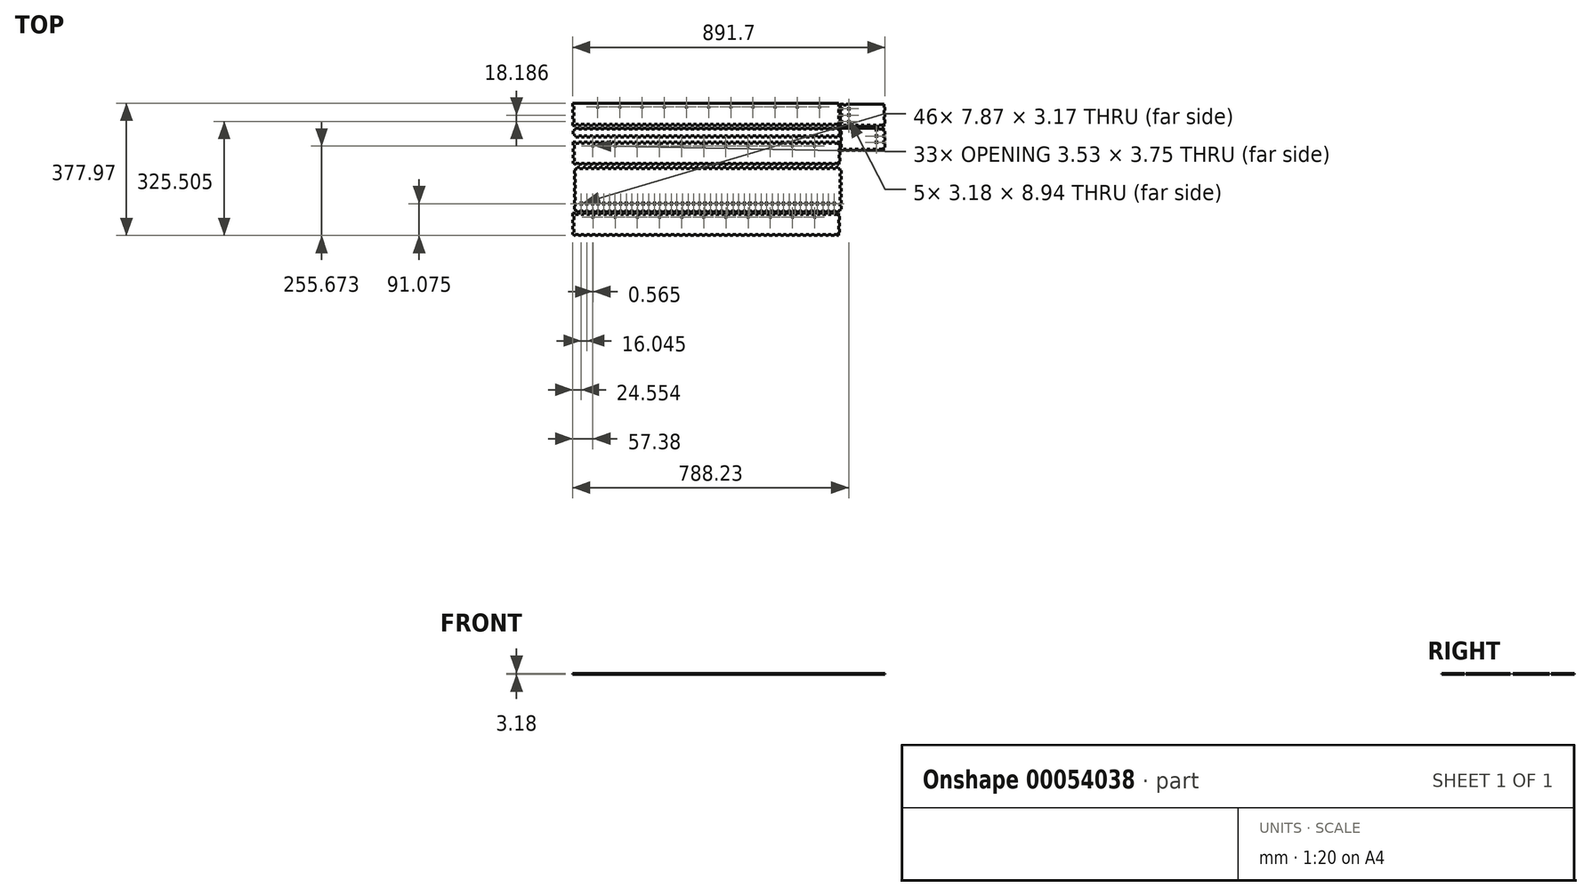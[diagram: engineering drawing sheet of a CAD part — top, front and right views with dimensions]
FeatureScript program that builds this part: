
annotation { "Feature Type Name" : "Feature", "Feature Type Description" : "" }
export const myFeature = defineFeature(function(context is Context, id is Id, definition is map)
    precondition{}
    {
        {
            var Q0;
            Q0=qCreatedBy(makeId("Top.planeOp"),FACE);
            var sketch = newSketch(context, id + "F0", { "sketchPlane" : qUnion([Q0])});
            skLineSegment(sketch, "E0", {"start": v(314.26, 109.75) * mm, "end": v(314.26, 115.01) * mm});
            skLineSegment(sketch, "E1", {"start": v(317.43, 109.75) * mm, "end": v(314.26, 109.75) * mm});
            skLineSegment(sketch, "E2", {"start": v(317.43, 101.12) * mm, "end": v(317.43, 109.75) * mm});
            skLineSegment(sketch, "E3", {"start": v(317.43, 101.12) * mm, "end": v(314.26, 101.12) * mm});
            skLineSegment(sketch, "E4", {"start": v(314.26, 95.9) * mm, "end": v(314.26, 101.12) * mm});
            skLineSegment(sketch, "E5", {"start": v(-441.55, 109.75) * mm, "end": v(-441.55, 115.16) * mm});
            skLineSegment(sketch, "E6", {"start": v(-441.55, 109.75) * mm, "end": v(-444.72, 109.75) * mm});
            skLineSegment(sketch, "E7", {"start": v(-444.72, 101.12) * mm, "end": v(-444.72, 109.75) * mm});
            skLineSegment(sketch, "E8", {"start": v(-441.55, 101.12) * mm, "end": v(-444.72, 101.12) * mm});
            skLineSegment(sketch, "E9", {"start": v(-441.55, 95.9) * mm, "end": v(-441.55, 101.12) * mm});
            skLineSegment(sketch, "E10", {"start": v(309.49, 114.97) * mm, "end": v(314.26, 114.97) * mm});
            skLineSegment(sketch, "E11", {"start": v(309.49, 118.14) * mm, "end": v(309.49, 114.97) * mm});
            skLineSegment(sketch, "E12", {"start": v(301.3, 118.14) * mm, "end": v(309.49, 118.14) * mm});
            skLineSegment(sketch, "E13", {"start": v(301.3, 118.14) * mm, "end": v(301.3, 114.97) * mm});
            skLineSegment(sketch, "E14", {"start": v(293.44, 114.97) * mm, "end": v(301.3, 114.97) * mm});
            skLineSegment(sketch, "E15", {"start": v(293.44, 118.14) * mm, "end": v(293.44, 114.97) * mm});
            skLineSegment(sketch, "E16", {"start": v(285.26, 118.14) * mm, "end": v(293.44, 118.14) * mm});
            skLineSegment(sketch, "E17", {"start": v(285.26, 118.14) * mm, "end": v(285.26, 114.97) * mm});
            skLineSegment(sketch, "E18", {"start": v(277.4, 114.97) * mm, "end": v(285.26, 114.97) * mm});
            skLineSegment(sketch, "E19", {"start": v(277.4, 118.14) * mm, "end": v(277.4, 114.97) * mm});
            skLineSegment(sketch, "E20", {"start": v(269.22, 118.14) * mm, "end": v(277.4, 118.14) * mm});
            skLineSegment(sketch, "E21", {"start": v(269.22, 118.14) * mm, "end": v(269.22, 114.97) * mm});
            skLineSegment(sketch, "E22", {"start": v(261.35, 114.97) * mm, "end": v(269.22, 114.97) * mm});
            skLineSegment(sketch, "E23", {"start": v(261.35, 118.14) * mm, "end": v(261.35, 114.97) * mm});
            skLineSegment(sketch, "E24", {"start": v(253.17, 118.14) * mm, "end": v(261.35, 118.14) * mm});
            skLineSegment(sketch, "E25", {"start": v(253.17, 118.14) * mm, "end": v(253.17, 114.97) * mm});
            skLineSegment(sketch, "E26", {"start": v(245.3, 114.97) * mm, "end": v(253.17, 114.97) * mm});
            skLineSegment(sketch, "E27", {"start": v(245.3, 118.14) * mm, "end": v(245.3, 114.97) * mm});
            skLineSegment(sketch, "E28", {"start": v(237.13, 118.14) * mm, "end": v(245.3, 118.14) * mm});
            skLineSegment(sketch, "E29", {"start": v(237.13, 118.14) * mm, "end": v(237.13, 114.97) * mm});
            skLineSegment(sketch, "E30", {"start": v(229.26, 114.97) * mm, "end": v(237.13, 114.97) * mm});
            skLineSegment(sketch, "E31", {"start": v(229.26, 118.14) * mm, "end": v(229.26, 114.97) * mm});
            skLineSegment(sketch, "E32", {"start": v(221.08, 118.14) * mm, "end": v(229.26, 118.14) * mm});
            skLineSegment(sketch, "E33", {"start": v(221.08, 118.14) * mm, "end": v(221.08, 114.97) * mm});
            skLineSegment(sketch, "E34", {"start": v(213.21, 114.97) * mm, "end": v(221.08, 114.97) * mm});
            skLineSegment(sketch, "E35", {"start": v(213.21, 118.14) * mm, "end": v(213.21, 114.97) * mm});
            skLineSegment(sketch, "E36", {"start": v(205.04, 118.14) * mm, "end": v(213.21, 118.14) * mm});
            skLineSegment(sketch, "E37", {"start": v(205.04, 118.14) * mm, "end": v(205.04, 114.97) * mm});
            skLineSegment(sketch, "E38", {"start": v(197.17, 114.97) * mm, "end": v(205.04, 114.97) * mm});
            skLineSegment(sketch, "E39", {"start": v(197.17, 118.14) * mm, "end": v(197.17, 114.97) * mm});
            skLineSegment(sketch, "E40", {"start": v(189, 118.14) * mm, "end": v(197.17, 118.14) * mm});
            skLineSegment(sketch, "E41", {"start": v(189, 118.14) * mm, "end": v(189, 114.97) * mm});
            skLineSegment(sketch, "E42", {"start": v(181.12, 114.97) * mm, "end": v(189, 114.97) * mm});
            skLineSegment(sketch, "E43", {"start": v(181.12, 118.14) * mm, "end": v(181.12, 114.97) * mm});
            skLineSegment(sketch, "E44", {"start": v(172.95, 118.14) * mm, "end": v(181.12, 118.14) * mm});
            skLineSegment(sketch, "E45", {"start": v(172.95, 118.14) * mm, "end": v(172.95, 114.97) * mm});
            skLineSegment(sketch, "E46", {"start": v(165.08, 114.97) * mm, "end": v(172.95, 114.97) * mm});
            skLineSegment(sketch, "E47", {"start": v(165.08, 118.14) * mm, "end": v(165.08, 114.97) * mm});
            skLineSegment(sketch, "E48", {"start": v(156.9, 118.14) * mm, "end": v(165.08, 118.14) * mm});
            skLineSegment(sketch, "E49", {"start": v(156.9, 118.14) * mm, "end": v(156.9, 114.97) * mm});
            skLineSegment(sketch, "E50", {"start": v(149.03, 114.97) * mm, "end": v(156.9, 114.97) * mm});
            skLineSegment(sketch, "E51", {"start": v(149.03, 118.14) * mm, "end": v(149.03, 114.97) * mm});
            skLineSegment(sketch, "E52", {"start": v(140.86, 118.14) * mm, "end": v(149.03, 118.14) * mm});
            skLineSegment(sketch, "E53", {"start": v(140.86, 118.14) * mm, "end": v(140.86, 114.97) * mm});
            skLineSegment(sketch, "E54", {"start": v(132.99, 114.97) * mm, "end": v(140.86, 114.97) * mm});
            skLineSegment(sketch, "E55", {"start": v(132.99, 118.14) * mm, "end": v(132.99, 114.97) * mm});
            skLineSegment(sketch, "E56", {"start": v(124.81, 118.14) * mm, "end": v(132.99, 118.14) * mm});
            skLineSegment(sketch, "E57", {"start": v(124.81, 118.14) * mm, "end": v(124.81, 114.97) * mm});
            skLineSegment(sketch, "E58", {"start": v(116.94, 114.97) * mm, "end": v(124.81, 114.97) * mm});
            skLineSegment(sketch, "E59", {"start": v(116.94, 118.14) * mm, "end": v(116.94, 114.97) * mm});
            skLineSegment(sketch, "E60", {"start": v(108.77, 118.14) * mm, "end": v(116.94, 118.14) * mm});
            skLineSegment(sketch, "E61", {"start": v(108.77, 118.14) * mm, "end": v(108.77, 114.97) * mm});
            skLineSegment(sketch, "E62", {"start": v(100.9, 114.97) * mm, "end": v(108.77, 114.97) * mm});
            skLineSegment(sketch, "E63", {"start": v(100.9, 118.14) * mm, "end": v(100.9, 114.97) * mm});
            skLineSegment(sketch, "E64", {"start": v(92.72, 118.14) * mm, "end": v(100.9, 118.14) * mm});
            skLineSegment(sketch, "E65", {"start": v(92.72, 118.14) * mm, "end": v(92.72, 114.97) * mm});
            skLineSegment(sketch, "E66", {"start": v(84.85, 114.97) * mm, "end": v(92.72, 114.97) * mm});
            skLineSegment(sketch, "E67", {"start": v(84.85, 118.14) * mm, "end": v(84.85, 114.97) * mm});
            skLineSegment(sketch, "E68", {"start": v(76.68, 118.14) * mm, "end": v(84.85, 118.14) * mm});
            skLineSegment(sketch, "E69", {"start": v(76.68, 118.14) * mm, "end": v(76.68, 114.97) * mm});
            skLineSegment(sketch, "E70", {"start": v(68.8, 114.97) * mm, "end": v(76.68, 114.97) * mm});
            skLineSegment(sketch, "E71", {"start": v(68.8, 118.14) * mm, "end": v(68.8, 114.97) * mm});
            skLineSegment(sketch, "E72", {"start": v(60.63, 118.14) * mm, "end": v(68.8, 118.14) * mm});
            skLineSegment(sketch, "E73", {"start": v(60.63, 118.14) * mm, "end": v(60.63, 114.97) * mm});
            skLineSegment(sketch, "E74", {"start": v(52.76, 114.97) * mm, "end": v(60.63, 114.97) * mm});
            skLineSegment(sketch, "E75", {"start": v(52.76, 118.14) * mm, "end": v(52.76, 114.97) * mm});
            skLineSegment(sketch, "E76", {"start": v(44.58, 118.14) * mm, "end": v(52.76, 118.14) * mm});
            skLineSegment(sketch, "E77", {"start": v(44.58, 118.14) * mm, "end": v(44.58, 114.97) * mm});
            skLineSegment(sketch, "E78", {"start": v(36.71, 114.97) * mm, "end": v(44.58, 114.97) * mm});
            skLineSegment(sketch, "E79", {"start": v(36.71, 118.14) * mm, "end": v(36.71, 114.97) * mm});
            skLineSegment(sketch, "E80", {"start": v(28.54, 118.14) * mm, "end": v(36.71, 118.14) * mm});
            skLineSegment(sketch, "E81", {"start": v(28.54, 118.14) * mm, "end": v(28.54, 114.97) * mm});
            skLineSegment(sketch, "E82", {"start": v(20.67, 114.97) * mm, "end": v(28.54, 114.97) * mm});
            skLineSegment(sketch, "E83", {"start": v(20.67, 118.14) * mm, "end": v(20.67, 114.97) * mm});
            skLineSegment(sketch, "E84", {"start": v(12.5, 118.14) * mm, "end": v(20.67, 118.14) * mm});
            skLineSegment(sketch, "E85", {"start": v(12.5, 118.14) * mm, "end": v(12.5, 114.97) * mm});
            skLineSegment(sketch, "E86", {"start": v(4.62, 114.97) * mm, "end": v(12.5, 114.97) * mm});
            skLineSegment(sketch, "E87", {"start": v(4.62, 118.14) * mm, "end": v(4.62, 114.97) * mm});
            skLineSegment(sketch, "E88", {"start": v(-3.55, 118.14) * mm, "end": v(4.62, 118.14) * mm});
            skLineSegment(sketch, "E89", {"start": v(-3.55, 118.14) * mm, "end": v(-3.55, 114.97) * mm});
            skLineSegment(sketch, "E90", {"start": v(-11.42, 114.97) * mm, "end": v(-3.55, 114.97) * mm});
            skLineSegment(sketch, "E91", {"start": v(-11.42, 118.14) * mm, "end": v(-11.42, 114.97) * mm});
            skLineSegment(sketch, "E92", {"start": v(-19.6, 118.14) * mm, "end": v(-11.42, 118.14) * mm});
            skLineSegment(sketch, "E93", {"start": v(-19.6, 118.14) * mm, "end": v(-19.6, 114.97) * mm});
            skLineSegment(sketch, "E94", {"start": v(-27.47, 114.97) * mm, "end": v(-19.6, 114.97) * mm});
            skLineSegment(sketch, "E95", {"start": v(-27.47, 118.14) * mm, "end": v(-27.47, 114.97) * mm});
            skLineSegment(sketch, "E96", {"start": v(-35.64, 118.14) * mm, "end": v(-27.47, 118.14) * mm});
            skLineSegment(sketch, "E97", {"start": v(-35.64, 118.14) * mm, "end": v(-35.64, 114.97) * mm});
            skLineSegment(sketch, "E98", {"start": v(-43.51, 114.97) * mm, "end": v(-35.64, 114.97) * mm});
            skLineSegment(sketch, "E99", {"start": v(-43.51, 118.14) * mm, "end": v(-43.51, 114.97) * mm});
            skLineSegment(sketch, "E100", {"start": v(-51.69, 118.14) * mm, "end": v(-43.51, 118.14) * mm});
            skLineSegment(sketch, "E101", {"start": v(-51.69, 118.14) * mm, "end": v(-51.69, 114.97) * mm});
            skLineSegment(sketch, "E102", {"start": v(-59.56, 114.97) * mm, "end": v(-51.69, 114.97) * mm});
            skLineSegment(sketch, "E103", {"start": v(-59.56, 118.14) * mm, "end": v(-59.56, 114.97) * mm});
            skLineSegment(sketch, "E104", {"start": v(-67.73, 118.14) * mm, "end": v(-59.56, 118.14) * mm});
            skLineSegment(sketch, "E105", {"start": v(-67.73, 118.14) * mm, "end": v(-67.73, 114.97) * mm});
            skLineSegment(sketch, "E106", {"start": v(-75.6, 114.97) * mm, "end": v(-67.73, 114.97) * mm});
            skLineSegment(sketch, "E107", {"start": v(-75.6, 118.14) * mm, "end": v(-75.6, 114.97) * mm});
            skLineSegment(sketch, "E108", {"start": v(-83.78, 118.14) * mm, "end": v(-75.6, 118.14) * mm});
            skLineSegment(sketch, "E109", {"start": v(-83.78, 118.14) * mm, "end": v(-83.78, 114.97) * mm});
            skLineSegment(sketch, "E110", {"start": v(-91.65, 114.97) * mm, "end": v(-83.78, 114.97) * mm});
            skLineSegment(sketch, "E111", {"start": v(-91.65, 118.14) * mm, "end": v(-91.65, 114.97) * mm});
            skLineSegment(sketch, "E112", {"start": v(-99.82, 118.14) * mm, "end": v(-91.65, 118.14) * mm});
            skLineSegment(sketch, "E113", {"start": v(-99.82, 118.14) * mm, "end": v(-99.82, 114.97) * mm});
            skLineSegment(sketch, "E114", {"start": v(-107.7, 114.97) * mm, "end": v(-99.82, 114.97) * mm});
            skLineSegment(sketch, "E115", {"start": v(-107.7, 118.14) * mm, "end": v(-107.7, 114.97) * mm});
            skLineSegment(sketch, "E116", {"start": v(-115.87, 118.14) * mm, "end": v(-107.7, 118.14) * mm});
            skLineSegment(sketch, "E117", {"start": v(-115.87, 118.14) * mm, "end": v(-115.87, 114.97) * mm});
            skLineSegment(sketch, "E118", {"start": v(-123.74, 114.97) * mm, "end": v(-115.87, 114.97) * mm});
            skLineSegment(sketch, "E119", {"start": v(-123.74, 118.14) * mm, "end": v(-123.74, 114.97) * mm});
            skLineSegment(sketch, "E120", {"start": v(-131.91, 118.14) * mm, "end": v(-123.74, 118.14) * mm});
            skLineSegment(sketch, "E121", {"start": v(-131.91, 118.14) * mm, "end": v(-131.91, 114.97) * mm});
            skLineSegment(sketch, "E122", {"start": v(-139.78, 114.97) * mm, "end": v(-131.91, 114.97) * mm});
            skLineSegment(sketch, "E123", {"start": v(-139.78, 118.14) * mm, "end": v(-139.78, 114.97) * mm});
            skLineSegment(sketch, "E124", {"start": v(-147.96, 118.14) * mm, "end": v(-139.78, 118.14) * mm});
            skLineSegment(sketch, "E125", {"start": v(-147.96, 118.14) * mm, "end": v(-147.96, 114.97) * mm});
            skLineSegment(sketch, "E126", {"start": v(-155.83, 114.97) * mm, "end": v(-147.96, 114.97) * mm});
            skLineSegment(sketch, "E127", {"start": v(-155.83, 118.14) * mm, "end": v(-155.83, 114.97) * mm});
            skLineSegment(sketch, "E128", {"start": v(-164, 118.14) * mm, "end": v(-155.83, 118.14) * mm});
            skLineSegment(sketch, "E129", {"start": v(-164, 118.14) * mm, "end": v(-164, 114.97) * mm});
            skLineSegment(sketch, "E130", {"start": v(-171.87, 114.97) * mm, "end": v(-164, 114.97) * mm});
            skLineSegment(sketch, "E131", {"start": v(-171.87, 118.14) * mm, "end": v(-171.87, 114.97) * mm});
            skLineSegment(sketch, "E132", {"start": v(-180.05, 118.14) * mm, "end": v(-171.87, 118.14) * mm});
            skLineSegment(sketch, "E133", {"start": v(-180.05, 118.14) * mm, "end": v(-180.05, 114.97) * mm});
            skLineSegment(sketch, "E134", {"start": v(-187.92, 114.97) * mm, "end": v(-180.05, 114.97) * mm});
            skLineSegment(sketch, "E135", {"start": v(-187.92, 118.14) * mm, "end": v(-187.92, 114.97) * mm});
            skLineSegment(sketch, "E136", {"start": v(-196.1, 118.14) * mm, "end": v(-187.92, 118.14) * mm});
            skLineSegment(sketch, "E137", {"start": v(-196.1, 118.14) * mm, "end": v(-196.1, 114.97) * mm});
            skLineSegment(sketch, "E138", {"start": v(-203.96, 114.97) * mm, "end": v(-196.1, 114.97) * mm});
            skLineSegment(sketch, "E139", {"start": v(-203.96, 118.14) * mm, "end": v(-203.96, 114.97) * mm});
            skLineSegment(sketch, "E140", {"start": v(-212.14, 118.14) * mm, "end": v(-203.96, 118.14) * mm});
            skLineSegment(sketch, "E141", {"start": v(-212.14, 118.14) * mm, "end": v(-212.14, 114.97) * mm});
            skLineSegment(sketch, "E142", {"start": v(-220.01, 114.97) * mm, "end": v(-212.14, 114.97) * mm});
            skLineSegment(sketch, "E143", {"start": v(-220.01, 118.14) * mm, "end": v(-220.01, 114.97) * mm});
            skLineSegment(sketch, "E144", {"start": v(-228.19, 118.14) * mm, "end": v(-220.01, 118.14) * mm});
            skLineSegment(sketch, "E145", {"start": v(-228.19, 118.14) * mm, "end": v(-228.19, 114.97) * mm});
            skLineSegment(sketch, "E146", {"start": v(-236.06, 114.97) * mm, "end": v(-228.19, 114.97) * mm});
            skLineSegment(sketch, "E147", {"start": v(-236.06, 118.14) * mm, "end": v(-236.06, 114.97) * mm});
            skLineSegment(sketch, "E148", {"start": v(-244.23, 118.14) * mm, "end": v(-236.06, 118.14) * mm});
            skLineSegment(sketch, "E149", {"start": v(-244.23, 118.14) * mm, "end": v(-244.23, 114.97) * mm});
            skLineSegment(sketch, "E150", {"start": v(-252.1, 114.97) * mm, "end": v(-244.23, 114.97) * mm});
            skLineSegment(sketch, "E151", {"start": v(-252.1, 118.14) * mm, "end": v(-252.1, 114.97) * mm});
            skLineSegment(sketch, "E152", {"start": v(-260.28, 118.14) * mm, "end": v(-252.1, 118.14) * mm});
            skLineSegment(sketch, "E153", {"start": v(-260.28, 118.14) * mm, "end": v(-260.28, 114.97) * mm});
            skLineSegment(sketch, "E154", {"start": v(-268.15, 114.97) * mm, "end": v(-260.28, 114.97) * mm});
            skLineSegment(sketch, "E155", {"start": v(-268.15, 118.14) * mm, "end": v(-268.15, 114.97) * mm});
            skLineSegment(sketch, "E156", {"start": v(-276.32, 118.14) * mm, "end": v(-268.15, 118.14) * mm});
            skLineSegment(sketch, "E157", {"start": v(-276.32, 118.14) * mm, "end": v(-276.32, 114.97) * mm});
            skLineSegment(sketch, "E158", {"start": v(-284.2, 114.97) * mm, "end": v(-276.32, 114.97) * mm});
            skLineSegment(sketch, "E159", {"start": v(-284.2, 118.14) * mm, "end": v(-284.2, 114.97) * mm});
            skLineSegment(sketch, "E160", {"start": v(-292.37, 118.14) * mm, "end": v(-284.2, 118.14) * mm});
            skLineSegment(sketch, "E161", {"start": v(-292.37, 118.14) * mm, "end": v(-292.37, 114.97) * mm});
            skLineSegment(sketch, "E162", {"start": v(-300.24, 114.97) * mm, "end": v(-292.37, 114.97) * mm});
            skLineSegment(sketch, "E163", {"start": v(-300.24, 118.14) * mm, "end": v(-300.24, 114.97) * mm});
            skLineSegment(sketch, "E164", {"start": v(-308.41, 118.14) * mm, "end": v(-300.24, 118.14) * mm});
            skLineSegment(sketch, "E165", {"start": v(-308.41, 118.14) * mm, "end": v(-308.41, 114.97) * mm});
            skLineSegment(sketch, "E166", {"start": v(-316.28, 114.97) * mm, "end": v(-308.41, 114.97) * mm});
            skLineSegment(sketch, "E167", {"start": v(-316.28, 118.14) * mm, "end": v(-316.28, 114.97) * mm});
            skLineSegment(sketch, "E168", {"start": v(-324.46, 118.14) * mm, "end": v(-316.28, 118.14) * mm});
            skLineSegment(sketch, "E169", {"start": v(-324.46, 118.14) * mm, "end": v(-324.46, 114.97) * mm});
            skLineSegment(sketch, "E170", {"start": v(-332.33, 114.97) * mm, "end": v(-324.46, 114.97) * mm});
            skLineSegment(sketch, "E171", {"start": v(-332.33, 118.14) * mm, "end": v(-332.33, 114.97) * mm});
            skLineSegment(sketch, "E172", {"start": v(-340.5, 118.14) * mm, "end": v(-332.33, 118.14) * mm});
            skLineSegment(sketch, "E173", {"start": v(-340.5, 118.14) * mm, "end": v(-340.5, 114.97) * mm});
            skLineSegment(sketch, "E174", {"start": v(-348.37, 114.97) * mm, "end": v(-340.5, 114.97) * mm});
            skLineSegment(sketch, "E175", {"start": v(-348.37, 118.14) * mm, "end": v(-348.37, 114.97) * mm});
            skLineSegment(sketch, "E176", {"start": v(-356.55, 118.14) * mm, "end": v(-348.37, 118.14) * mm});
            skLineSegment(sketch, "E177", {"start": v(-356.55, 118.14) * mm, "end": v(-356.55, 114.97) * mm});
            skLineSegment(sketch, "E178", {"start": v(-364.42, 114.97) * mm, "end": v(-356.55, 114.97) * mm});
            skLineSegment(sketch, "E179", {"start": v(-364.42, 118.14) * mm, "end": v(-364.42, 114.97) * mm});
            skLineSegment(sketch, "E180", {"start": v(-372.6, 118.14) * mm, "end": v(-364.42, 118.14) * mm});
            skLineSegment(sketch, "E181", {"start": v(-372.6, 118.14) * mm, "end": v(-372.6, 114.97) * mm});
            skLineSegment(sketch, "E182", {"start": v(-380.46, 114.97) * mm, "end": v(-372.6, 114.97) * mm});
            skLineSegment(sketch, "E183", {"start": v(-380.46, 118.14) * mm, "end": v(-380.46, 114.97) * mm});
            skLineSegment(sketch, "E184", {"start": v(-388.64, 118.14) * mm, "end": v(-380.46, 118.14) * mm});
            skLineSegment(sketch, "E185", {"start": v(-388.64, 118.14) * mm, "end": v(-388.64, 114.97) * mm});
            skLineSegment(sketch, "E186", {"start": v(-396.5, 114.97) * mm, "end": v(-388.64, 114.97) * mm});
            skLineSegment(sketch, "E187", {"start": v(-396.5, 118.14) * mm, "end": v(-396.5, 114.97) * mm});
            skLineSegment(sketch, "E188", {"start": v(-404.68, 118.14) * mm, "end": v(-396.5, 118.14) * mm});
            skLineSegment(sketch, "E189", {"start": v(-404.68, 118.14) * mm, "end": v(-404.68, 114.97) * mm});
            skLineSegment(sketch, "E190", {"start": v(-412.55, 114.97) * mm, "end": v(-404.68, 114.97) * mm});
            skLineSegment(sketch, "E191", {"start": v(-412.55, 118.14) * mm, "end": v(-412.55, 114.97) * mm});
            skLineSegment(sketch, "E192", {"start": v(-420.73, 118.14) * mm, "end": v(-412.55, 118.14) * mm});
            skLineSegment(sketch, "E193", {"start": v(-420.73, 118.14) * mm, "end": v(-420.73, 114.97) * mm});
            skLineSegment(sketch, "E194", {"start": v(-428.6, 114.97) * mm, "end": v(-420.73, 114.97) * mm});
            skLineSegment(sketch, "E195", {"start": v(-428.6, 118.14) * mm, "end": v(-428.6, 114.97) * mm});
            skLineSegment(sketch, "E196", {"start": v(-436.77, 118.14) * mm, "end": v(-428.6, 118.14) * mm});
            skLineSegment(sketch, "E197", {"start": v(-436.77, 118.14) * mm, "end": v(-436.77, 114.97) * mm});
            skLineSegment(sketch, "E198", {"start": v(-441.55, 114.97) * mm, "end": v(-436.77, 114.97) * mm});
            skLineSegment(sketch, "E199", {"start": v(309.49, 95.9) * mm, "end": v(314.26, 95.9) * mm});
            skLineSegment(sketch, "E200", {"start": v(309.49, 95.9) * mm, "end": v(309.49, 92.72) * mm});
            skLineSegment(sketch, "E201", {"start": v(301.3, 92.72) * mm, "end": v(309.49, 92.72) * mm});
            skLineSegment(sketch, "E202", {"start": v(301.3, 95.9) * mm, "end": v(301.3, 92.72) * mm});
            skLineSegment(sketch, "E203", {"start": v(293.44, 95.9) * mm, "end": v(301.3, 95.9) * mm});
            skLineSegment(sketch, "E204", {"start": v(293.44, 95.9) * mm, "end": v(293.44, 92.72) * mm});
            skLineSegment(sketch, "E205", {"start": v(285.26, 92.72) * mm, "end": v(293.44, 92.72) * mm});
            skLineSegment(sketch, "E206", {"start": v(285.26, 95.9) * mm, "end": v(285.26, 92.72) * mm});
            skLineSegment(sketch, "E207", {"start": v(277.4, 95.9) * mm, "end": v(285.26, 95.9) * mm});
            skLineSegment(sketch, "E208", {"start": v(277.4, 95.9) * mm, "end": v(277.4, 92.72) * mm});
            skLineSegment(sketch, "E209", {"start": v(269.22, 92.72) * mm, "end": v(277.4, 92.72) * mm});
            skLineSegment(sketch, "E210", {"start": v(269.22, 95.9) * mm, "end": v(269.22, 92.72) * mm});
            skLineSegment(sketch, "E211", {"start": v(261.35, 95.9) * mm, "end": v(269.22, 95.9) * mm});
            skLineSegment(sketch, "E212", {"start": v(261.35, 95.9) * mm, "end": v(261.35, 92.72) * mm});
            skLineSegment(sketch, "E213", {"start": v(253.17, 92.72) * mm, "end": v(261.35, 92.72) * mm});
            skLineSegment(sketch, "E214", {"start": v(253.17, 95.9) * mm, "end": v(253.17, 92.72) * mm});
            skLineSegment(sketch, "E215", {"start": v(245.3, 95.9) * mm, "end": v(253.17, 95.9) * mm});
            skLineSegment(sketch, "E216", {"start": v(245.3, 95.9) * mm, "end": v(245.3, 92.72) * mm});
            skLineSegment(sketch, "E217", {"start": v(237.13, 92.72) * mm, "end": v(245.3, 92.72) * mm});
            skLineSegment(sketch, "E218", {"start": v(237.13, 95.9) * mm, "end": v(237.13, 92.72) * mm});
            skLineSegment(sketch, "E219", {"start": v(229.26, 95.9) * mm, "end": v(237.13, 95.9) * mm});
            skLineSegment(sketch, "E220", {"start": v(229.26, 95.9) * mm, "end": v(229.26, 92.72) * mm});
            skLineSegment(sketch, "E221", {"start": v(221.08, 92.72) * mm, "end": v(229.26, 92.72) * mm});
            skLineSegment(sketch, "E222", {"start": v(221.08, 95.9) * mm, "end": v(221.08, 92.72) * mm});
            skLineSegment(sketch, "E223", {"start": v(213.21, 95.9) * mm, "end": v(221.08, 95.9) * mm});
            skLineSegment(sketch, "E224", {"start": v(213.21, 95.9) * mm, "end": v(213.21, 92.72) * mm});
            skLineSegment(sketch, "E225", {"start": v(205.04, 92.72) * mm, "end": v(213.21, 92.72) * mm});
            skLineSegment(sketch, "E226", {"start": v(205.04, 95.9) * mm, "end": v(205.04, 92.72) * mm});
            skLineSegment(sketch, "E227", {"start": v(197.17, 95.9) * mm, "end": v(205.04, 95.9) * mm});
            skLineSegment(sketch, "E228", {"start": v(197.17, 95.9) * mm, "end": v(197.17, 92.72) * mm});
            skLineSegment(sketch, "E229", {"start": v(189, 92.72) * mm, "end": v(197.17, 92.72) * mm});
            skLineSegment(sketch, "E230", {"start": v(189, 95.9) * mm, "end": v(189, 92.72) * mm});
            skLineSegment(sketch, "E231", {"start": v(181.12, 95.9) * mm, "end": v(189, 95.9) * mm});
            skLineSegment(sketch, "E232", {"start": v(181.12, 95.9) * mm, "end": v(181.12, 92.72) * mm});
            skLineSegment(sketch, "E233", {"start": v(172.95, 92.72) * mm, "end": v(181.12, 92.72) * mm});
            skLineSegment(sketch, "E234", {"start": v(172.95, 95.9) * mm, "end": v(172.95, 92.72) * mm});
            skLineSegment(sketch, "E235", {"start": v(165.08, 95.9) * mm, "end": v(172.95, 95.9) * mm});
            skLineSegment(sketch, "E236", {"start": v(165.08, 95.9) * mm, "end": v(165.08, 92.72) * mm});
            skLineSegment(sketch, "E237", {"start": v(156.9, 92.72) * mm, "end": v(165.08, 92.72) * mm});
            skLineSegment(sketch, "E238", {"start": v(156.9, 95.9) * mm, "end": v(156.9, 92.72) * mm});
            skLineSegment(sketch, "E239", {"start": v(149.03, 95.9) * mm, "end": v(156.9, 95.9) * mm});
            skLineSegment(sketch, "E240", {"start": v(149.03, 95.9) * mm, "end": v(149.03, 92.72) * mm});
            skLineSegment(sketch, "E241", {"start": v(140.86, 92.72) * mm, "end": v(149.03, 92.72) * mm});
            skLineSegment(sketch, "E242", {"start": v(140.86, 95.9) * mm, "end": v(140.86, 92.72) * mm});
            skLineSegment(sketch, "E243", {"start": v(132.99, 95.9) * mm, "end": v(140.86, 95.9) * mm});
            skLineSegment(sketch, "E244", {"start": v(132.99, 95.9) * mm, "end": v(132.99, 92.72) * mm});
            skLineSegment(sketch, "E245", {"start": v(124.81, 92.72) * mm, "end": v(132.99, 92.72) * mm});
            skLineSegment(sketch, "E246", {"start": v(124.81, 95.9) * mm, "end": v(124.81, 92.72) * mm});
            skLineSegment(sketch, "E247", {"start": v(116.94, 95.9) * mm, "end": v(124.81, 95.9) * mm});
            skLineSegment(sketch, "E248", {"start": v(116.94, 95.9) * mm, "end": v(116.94, 92.72) * mm});
            skLineSegment(sketch, "E249", {"start": v(108.77, 92.72) * mm, "end": v(116.94, 92.72) * mm});
            skLineSegment(sketch, "E250", {"start": v(108.77, 95.9) * mm, "end": v(108.77, 92.72) * mm});
            skLineSegment(sketch, "E251", {"start": v(100.9, 95.9) * mm, "end": v(108.77, 95.9) * mm});
            skLineSegment(sketch, "E252", {"start": v(100.9, 95.9) * mm, "end": v(100.9, 92.72) * mm});
            skLineSegment(sketch, "E253", {"start": v(92.72, 92.72) * mm, "end": v(100.9, 92.72) * mm});
            skLineSegment(sketch, "E254", {"start": v(92.72, 95.9) * mm, "end": v(92.72, 92.72) * mm});
            skLineSegment(sketch, "E255", {"start": v(84.85, 95.9) * mm, "end": v(92.72, 95.9) * mm});
            skLineSegment(sketch, "E256", {"start": v(84.85, 95.9) * mm, "end": v(84.85, 92.72) * mm});
            skLineSegment(sketch, "E257", {"start": v(76.68, 92.72) * mm, "end": v(84.85, 92.72) * mm});
            skLineSegment(sketch, "E258", {"start": v(76.68, 95.9) * mm, "end": v(76.68, 92.72) * mm});
            skLineSegment(sketch, "E259", {"start": v(68.8, 95.9) * mm, "end": v(76.68, 95.9) * mm});
            skLineSegment(sketch, "E260", {"start": v(68.8, 95.9) * mm, "end": v(68.8, 92.72) * mm});
            skLineSegment(sketch, "E261", {"start": v(60.63, 92.72) * mm, "end": v(68.8, 92.72) * mm});
            skLineSegment(sketch, "E262", {"start": v(60.63, 95.9) * mm, "end": v(60.63, 92.72) * mm});
            skLineSegment(sketch, "E263", {"start": v(52.76, 95.9) * mm, "end": v(60.63, 95.9) * mm});
            skLineSegment(sketch, "E264", {"start": v(52.76, 95.9) * mm, "end": v(52.76, 92.72) * mm});
            skLineSegment(sketch, "E265", {"start": v(44.58, 92.72) * mm, "end": v(52.76, 92.72) * mm});
            skLineSegment(sketch, "E266", {"start": v(44.58, 95.9) * mm, "end": v(44.58, 92.72) * mm});
            skLineSegment(sketch, "E267", {"start": v(36.71, 95.9) * mm, "end": v(44.58, 95.9) * mm});
            skLineSegment(sketch, "E268", {"start": v(36.71, 95.9) * mm, "end": v(36.71, 92.72) * mm});
            skLineSegment(sketch, "E269", {"start": v(28.54, 92.72) * mm, "end": v(36.71, 92.72) * mm});
            skLineSegment(sketch, "E270", {"start": v(28.54, 95.9) * mm, "end": v(28.54, 92.72) * mm});
            skLineSegment(sketch, "E271", {"start": v(20.67, 95.9) * mm, "end": v(28.54, 95.9) * mm});
            skLineSegment(sketch, "E272", {"start": v(20.67, 95.9) * mm, "end": v(20.67, 92.72) * mm});
            skLineSegment(sketch, "E273", {"start": v(12.5, 92.72) * mm, "end": v(20.67, 92.72) * mm});
            skLineSegment(sketch, "E274", {"start": v(12.5, 95.9) * mm, "end": v(12.5, 92.72) * mm});
            skLineSegment(sketch, "E275", {"start": v(4.62, 95.9) * mm, "end": v(12.5, 95.9) * mm});
            skLineSegment(sketch, "E276", {"start": v(4.62, 95.9) * mm, "end": v(4.62, 92.72) * mm});
            skLineSegment(sketch, "E277", {"start": v(-3.55, 92.72) * mm, "end": v(4.62, 92.72) * mm});
            skLineSegment(sketch, "E278", {"start": v(-3.55, 95.9) * mm, "end": v(-3.55, 92.72) * mm});
            skLineSegment(sketch, "E279", {"start": v(-11.42, 95.9) * mm, "end": v(-3.55, 95.9) * mm});
            skLineSegment(sketch, "E280", {"start": v(-11.42, 95.9) * mm, "end": v(-11.42, 92.72) * mm});
            skLineSegment(sketch, "E281", {"start": v(-19.6, 92.72) * mm, "end": v(-11.42, 92.72) * mm});
            skLineSegment(sketch, "E282", {"start": v(-19.6, 95.9) * mm, "end": v(-19.6, 92.72) * mm});
            skLineSegment(sketch, "E283", {"start": v(-27.47, 95.9) * mm, "end": v(-19.6, 95.9) * mm});
            skLineSegment(sketch, "E284", {"start": v(-27.47, 95.9) * mm, "end": v(-27.47, 92.72) * mm});
            skLineSegment(sketch, "E285", {"start": v(-35.64, 92.72) * mm, "end": v(-27.47, 92.72) * mm});
            skLineSegment(sketch, "E286", {"start": v(-35.64, 95.9) * mm, "end": v(-35.64, 92.72) * mm});
            skLineSegment(sketch, "E287", {"start": v(-43.51, 95.9) * mm, "end": v(-35.64, 95.9) * mm});
            skLineSegment(sketch, "E288", {"start": v(-43.51, 95.9) * mm, "end": v(-43.51, 92.72) * mm});
            skLineSegment(sketch, "E289", {"start": v(-51.69, 92.72) * mm, "end": v(-43.51, 92.72) * mm});
            skLineSegment(sketch, "E290", {"start": v(-51.69, 95.9) * mm, "end": v(-51.69, 92.72) * mm});
            skLineSegment(sketch, "E291", {"start": v(-59.56, 95.9) * mm, "end": v(-51.69, 95.9) * mm});
            skLineSegment(sketch, "E292", {"start": v(-59.56, 95.9) * mm, "end": v(-59.56, 92.72) * mm});
            skLineSegment(sketch, "E293", {"start": v(-67.73, 92.72) * mm, "end": v(-59.56, 92.72) * mm});
            skLineSegment(sketch, "E294", {"start": v(-67.73, 95.9) * mm, "end": v(-67.73, 92.72) * mm});
            skLineSegment(sketch, "E295", {"start": v(-75.6, 95.9) * mm, "end": v(-67.73, 95.9) * mm});
            skLineSegment(sketch, "E296", {"start": v(-75.6, 95.9) * mm, "end": v(-75.6, 92.72) * mm});
            skLineSegment(sketch, "E297", {"start": v(-83.78, 92.72) * mm, "end": v(-75.6, 92.72) * mm});
            skLineSegment(sketch, "E298", {"start": v(-83.78, 95.9) * mm, "end": v(-83.78, 92.72) * mm});
            skLineSegment(sketch, "E299", {"start": v(-91.65, 95.9) * mm, "end": v(-83.78, 95.9) * mm});
            skLineSegment(sketch, "E300", {"start": v(-91.65, 95.9) * mm, "end": v(-91.65, 92.72) * mm});
            skLineSegment(sketch, "E301", {"start": v(-99.82, 92.72) * mm, "end": v(-91.65, 92.72) * mm});
            skLineSegment(sketch, "E302", {"start": v(-99.82, 95.9) * mm, "end": v(-99.82, 92.72) * mm});
            skLineSegment(sketch, "E303", {"start": v(-107.7, 95.9) * mm, "end": v(-99.82, 95.9) * mm});
            skLineSegment(sketch, "E304", {"start": v(-107.7, 95.9) * mm, "end": v(-107.7, 92.72) * mm});
            skLineSegment(sketch, "E305", {"start": v(-115.87, 92.72) * mm, "end": v(-107.7, 92.72) * mm});
            skLineSegment(sketch, "E306", {"start": v(-115.87, 95.9) * mm, "end": v(-115.87, 92.72) * mm});
            skLineSegment(sketch, "E307", {"start": v(-123.74, 95.9) * mm, "end": v(-115.87, 95.9) * mm});
            skLineSegment(sketch, "E308", {"start": v(-123.74, 95.9) * mm, "end": v(-123.74, 92.72) * mm});
            skLineSegment(sketch, "E309", {"start": v(-131.91, 92.72) * mm, "end": v(-123.74, 92.72) * mm});
            skLineSegment(sketch, "E310", {"start": v(-131.91, 95.9) * mm, "end": v(-131.91, 92.72) * mm});
            skLineSegment(sketch, "E311", {"start": v(-139.78, 95.9) * mm, "end": v(-131.91, 95.9) * mm});
            skLineSegment(sketch, "E312", {"start": v(-139.78, 95.9) * mm, "end": v(-139.78, 92.72) * mm});
            skLineSegment(sketch, "E313", {"start": v(-147.96, 92.72) * mm, "end": v(-139.78, 92.72) * mm});
            skLineSegment(sketch, "E314", {"start": v(-147.96, 95.9) * mm, "end": v(-147.96, 92.72) * mm});
            skLineSegment(sketch, "E315", {"start": v(-155.83, 95.9) * mm, "end": v(-147.96, 95.9) * mm});
            skLineSegment(sketch, "E316", {"start": v(-155.83, 95.9) * mm, "end": v(-155.83, 92.72) * mm});
            skLineSegment(sketch, "E317", {"start": v(-164, 92.72) * mm, "end": v(-155.83, 92.72) * mm});
            skLineSegment(sketch, "E318", {"start": v(-164, 95.9) * mm, "end": v(-164, 92.72) * mm});
            skLineSegment(sketch, "E319", {"start": v(-171.87, 95.9) * mm, "end": v(-164, 95.9) * mm});
            skLineSegment(sketch, "E320", {"start": v(-171.87, 95.9) * mm, "end": v(-171.87, 92.72) * mm});
            skLineSegment(sketch, "E321", {"start": v(-180.05, 92.72) * mm, "end": v(-171.87, 92.72) * mm});
            skLineSegment(sketch, "E322", {"start": v(-180.05, 95.9) * mm, "end": v(-180.05, 92.72) * mm});
            skLineSegment(sketch, "E323", {"start": v(-187.92, 95.9) * mm, "end": v(-180.05, 95.9) * mm});
            skLineSegment(sketch, "E324", {"start": v(-187.92, 95.9) * mm, "end": v(-187.92, 92.72) * mm});
            skLineSegment(sketch, "E325", {"start": v(-196.1, 92.72) * mm, "end": v(-187.92, 92.72) * mm});
            skLineSegment(sketch, "E326", {"start": v(-196.1, 95.9) * mm, "end": v(-196.1, 92.72) * mm});
            skLineSegment(sketch, "E327", {"start": v(-203.96, 95.9) * mm, "end": v(-196.1, 95.9) * mm});
            skLineSegment(sketch, "E328", {"start": v(-203.96, 95.9) * mm, "end": v(-203.96, 92.72) * mm});
            skLineSegment(sketch, "E329", {"start": v(-212.14, 92.72) * mm, "end": v(-203.96, 92.72) * mm});
            skLineSegment(sketch, "E330", {"start": v(-212.14, 95.9) * mm, "end": v(-212.14, 92.72) * mm});
            skLineSegment(sketch, "E331", {"start": v(-220.01, 95.9) * mm, "end": v(-212.14, 95.9) * mm});
            skLineSegment(sketch, "E332", {"start": v(-220.01, 95.9) * mm, "end": v(-220.01, 92.72) * mm});
            skLineSegment(sketch, "E333", {"start": v(-228.19, 92.72) * mm, "end": v(-220.01, 92.72) * mm});
            skLineSegment(sketch, "E334", {"start": v(-228.19, 95.9) * mm, "end": v(-228.19, 92.72) * mm});
            skLineSegment(sketch, "E335", {"start": v(-236.06, 95.9) * mm, "end": v(-228.19, 95.9) * mm});
            skLineSegment(sketch, "E336", {"start": v(-236.06, 95.9) * mm, "end": v(-236.06, 92.72) * mm});
            skLineSegment(sketch, "E337", {"start": v(-244.23, 92.72) * mm, "end": v(-236.06, 92.72) * mm});
            skLineSegment(sketch, "E338", {"start": v(-244.23, 95.9) * mm, "end": v(-244.23, 92.72) * mm});
            skLineSegment(sketch, "E339", {"start": v(-252.1, 95.9) * mm, "end": v(-244.23, 95.9) * mm});
            skLineSegment(sketch, "E340", {"start": v(-252.1, 95.9) * mm, "end": v(-252.1, 92.72) * mm});
            skLineSegment(sketch, "E341", {"start": v(-260.28, 92.72) * mm, "end": v(-252.1, 92.72) * mm});
            skLineSegment(sketch, "E342", {"start": v(-260.28, 95.9) * mm, "end": v(-260.28, 92.72) * mm});
            skLineSegment(sketch, "E343", {"start": v(-268.15, 95.9) * mm, "end": v(-260.28, 95.9) * mm});
            skLineSegment(sketch, "E344", {"start": v(-268.15, 95.9) * mm, "end": v(-268.15, 92.72) * mm});
            skLineSegment(sketch, "E345", {"start": v(-276.32, 92.72) * mm, "end": v(-268.15, 92.72) * mm});
            skLineSegment(sketch, "E346", {"start": v(-276.32, 95.9) * mm, "end": v(-276.32, 92.72) * mm});
            skLineSegment(sketch, "E347", {"start": v(-284.2, 95.9) * mm, "end": v(-276.32, 95.9) * mm});
            skLineSegment(sketch, "E348", {"start": v(-284.2, 95.9) * mm, "end": v(-284.2, 92.72) * mm});
            skLineSegment(sketch, "E349", {"start": v(-292.37, 92.72) * mm, "end": v(-284.2, 92.72) * mm});
            skLineSegment(sketch, "E350", {"start": v(-292.37, 95.9) * mm, "end": v(-292.37, 92.72) * mm});
            skLineSegment(sketch, "E351", {"start": v(-300.24, 95.9) * mm, "end": v(-292.37, 95.9) * mm});
            skLineSegment(sketch, "E352", {"start": v(-300.24, 95.9) * mm, "end": v(-300.24, 92.72) * mm});
            skLineSegment(sketch, "E353", {"start": v(-308.41, 92.72) * mm, "end": v(-300.24, 92.72) * mm});
            skLineSegment(sketch, "E354", {"start": v(-308.41, 95.9) * mm, "end": v(-308.41, 92.72) * mm});
            skLineSegment(sketch, "E355", {"start": v(-316.28, 95.9) * mm, "end": v(-308.41, 95.9) * mm});
            skLineSegment(sketch, "E356", {"start": v(-316.28, 95.9) * mm, "end": v(-316.28, 92.72) * mm});
            skLineSegment(sketch, "E357", {"start": v(-324.46, 92.72) * mm, "end": v(-316.28, 92.72) * mm});
            skLineSegment(sketch, "E358", {"start": v(-324.46, 95.9) * mm, "end": v(-324.46, 92.72) * mm});
            skLineSegment(sketch, "E359", {"start": v(-332.33, 95.9) * mm, "end": v(-324.46, 95.9) * mm});
            skLineSegment(sketch, "E360", {"start": v(-332.33, 95.9) * mm, "end": v(-332.33, 92.72) * mm});
            skLineSegment(sketch, "E361", {"start": v(-340.5, 92.72) * mm, "end": v(-332.33, 92.72) * mm});
            skLineSegment(sketch, "E362", {"start": v(-340.5, 95.9) * mm, "end": v(-340.5, 92.72) * mm});
            skLineSegment(sketch, "E363", {"start": v(-348.37, 95.9) * mm, "end": v(-340.5, 95.9) * mm});
            skLineSegment(sketch, "E364", {"start": v(-348.37, 95.9) * mm, "end": v(-348.37, 92.72) * mm});
            skLineSegment(sketch, "E365", {"start": v(-356.55, 92.72) * mm, "end": v(-348.37, 92.72) * mm});
            skLineSegment(sketch, "E366", {"start": v(-356.55, 95.9) * mm, "end": v(-356.55, 92.72) * mm});
            skLineSegment(sketch, "E367", {"start": v(-364.42, 95.9) * mm, "end": v(-356.55, 95.9) * mm});
            skLineSegment(sketch, "E368", {"start": v(-364.42, 95.9) * mm, "end": v(-364.42, 92.72) * mm});
            skLineSegment(sketch, "E369", {"start": v(-372.6, 92.72) * mm, "end": v(-364.42, 92.72) * mm});
            skLineSegment(sketch, "E370", {"start": v(-372.6, 95.9) * mm, "end": v(-372.6, 92.72) * mm});
            skLineSegment(sketch, "E371", {"start": v(-380.46, 95.9) * mm, "end": v(-372.6, 95.9) * mm});
            skLineSegment(sketch, "E372", {"start": v(-380.46, 95.9) * mm, "end": v(-380.46, 92.72) * mm});
            skLineSegment(sketch, "E373", {"start": v(-388.64, 92.72) * mm, "end": v(-380.46, 92.72) * mm});
            skLineSegment(sketch, "E374", {"start": v(-388.64, 95.9) * mm, "end": v(-388.64, 92.72) * mm});
            skLineSegment(sketch, "E375", {"start": v(-396.5, 95.9) * mm, "end": v(-388.64, 95.9) * mm});
            skLineSegment(sketch, "E376", {"start": v(-396.5, 95.9) * mm, "end": v(-396.5, 92.72) * mm});
            skLineSegment(sketch, "E377", {"start": v(-404.68, 92.72) * mm, "end": v(-396.5, 92.72) * mm});
            skLineSegment(sketch, "E378", {"start": v(-404.68, 95.9) * mm, "end": v(-404.68, 92.72) * mm});
            skLineSegment(sketch, "E379", {"start": v(-412.55, 95.9) * mm, "end": v(-404.68, 95.9) * mm});
            skLineSegment(sketch, "E380", {"start": v(-412.55, 95.9) * mm, "end": v(-412.55, 92.72) * mm});
            skLineSegment(sketch, "E381", {"start": v(-420.73, 92.72) * mm, "end": v(-412.55, 92.72) * mm});
            skLineSegment(sketch, "E382", {"start": v(-420.73, 95.9) * mm, "end": v(-420.73, 92.72) * mm});
            skLineSegment(sketch, "E383", {"start": v(-428.6, 95.9) * mm, "end": v(-420.73, 95.9) * mm});
            skLineSegment(sketch, "E384", {"start": v(-428.6, 95.9) * mm, "end": v(-428.6, 92.72) * mm});
            skLineSegment(sketch, "E385", {"start": v(-436.77, 92.72) * mm, "end": v(-428.6, 92.72) * mm});
            skLineSegment(sketch, "E386", {"start": v(-436.77, 95.9) * mm, "end": v(-436.77, 92.72) * mm});
            skLineSegment(sketch, "E387", {"start": v(-441.55, 95.9) * mm, "end": v(-436.77, 95.9) * mm});
            skLineSegment(sketch, "E388", {"start": v(317.63, -2.92) * mm, "end": v(317.63, 2.3) * mm});
            skLineSegment(sketch, "E389", {"start": v(320.8, -2.92) * mm, "end": v(317.63, -2.92) * mm});
            skLineSegment(sketch, "E390", {"start": v(320.8, -11.55) * mm, "end": v(320.8, -2.92) * mm});
            skLineSegment(sketch, "E391", {"start": v(320.8, -11.55) * mm, "end": v(317.63, -11.55) * mm});
            skLineSegment(sketch, "E392", {"start": v(317.63, -19.88) * mm, "end": v(317.63, -11.55) * mm});
            skLineSegment(sketch, "E393", {"start": v(320.8, -19.88) * mm, "end": v(317.63, -19.88) * mm});
            skLineSegment(sketch, "E394", {"start": v(320.8, -28.5) * mm, "end": v(320.8, -19.88) * mm});
            skLineSegment(sketch, "E395", {"start": v(320.8, -28.5) * mm, "end": v(317.63, -28.5) * mm});
            skLineSegment(sketch, "E396", {"start": v(317.63, -36.83) * mm, "end": v(317.63, -28.5) * mm});
            skLineSegment(sketch, "E397", {"start": v(320.8, -36.83) * mm, "end": v(317.63, -36.83) * mm});
            skLineSegment(sketch, "E398", {"start": v(320.8, -45.46) * mm, "end": v(320.8, -36.83) * mm});
            skLineSegment(sketch, "E399", {"start": v(320.8, -45.46) * mm, "end": v(317.63, -45.46) * mm});
            skLineSegment(sketch, "E400", {"start": v(317.63, -53.78) * mm, "end": v(317.63, -45.46) * mm});
            skLineSegment(sketch, "E401", {"start": v(320.8, -53.78) * mm, "end": v(317.63, -53.78) * mm});
            skLineSegment(sketch, "E402", {"start": v(320.8, -62.41) * mm, "end": v(320.8, -53.78) * mm});
            skLineSegment(sketch, "E403", {"start": v(320.8, -62.41) * mm, "end": v(317.63, -62.41) * mm});
            skLineSegment(sketch, "E404", {"start": v(317.63, -70.74) * mm, "end": v(317.63, -62.41) * mm});
            skLineSegment(sketch, "E405", {"start": v(320.8, -70.74) * mm, "end": v(317.63, -70.74) * mm});
            skLineSegment(sketch, "E406", {"start": v(320.8, -79.37) * mm, "end": v(320.8, -70.74) * mm});
            skLineSegment(sketch, "E407", {"start": v(320.8, -79.37) * mm, "end": v(317.63, -79.37) * mm});
            skLineSegment(sketch, "E408", {"start": v(317.63, -87.7) * mm, "end": v(317.63, -79.37) * mm});
            skLineSegment(sketch, "E409", {"start": v(320.8, -87.7) * mm, "end": v(317.63, -87.7) * mm});
            skLineSegment(sketch, "E410", {"start": v(320.8, -96.32) * mm, "end": v(320.8, -87.7) * mm});
            skLineSegment(sketch, "E411", {"start": v(320.8, -96.32) * mm, "end": v(317.63, -96.32) * mm});
            skLineSegment(sketch, "E412", {"start": v(317.63, -104.64) * mm, "end": v(317.63, -96.32) * mm});
            skLineSegment(sketch, "E413", {"start": v(320.8, -104.64) * mm, "end": v(317.63, -104.64) * mm});
            skLineSegment(sketch, "E414", {"start": v(320.8, -113.27) * mm, "end": v(320.8, -104.64) * mm});
            skLineSegment(sketch, "E415", {"start": v(320.8, -113.27) * mm, "end": v(317.63, -113.27) * mm});
            skLineSegment(sketch, "E416", {"start": v(317.63, -118.5) * mm, "end": v(317.63, -113.27) * mm});
            skLineSegment(sketch, "E417", {"start": v(-438.18, -2.92) * mm, "end": v(-438.18, 2.3) * mm});
            skLineSegment(sketch, "E418", {"start": v(-438.18, -2.92) * mm, "end": v(-441.35, -2.92) * mm});
            skLineSegment(sketch, "E419", {"start": v(-441.35, -11.55) * mm, "end": v(-441.35, -2.92) * mm});
            skLineSegment(sketch, "E420", {"start": v(-438.18, -11.55) * mm, "end": v(-441.35, -11.55) * mm});
            skLineSegment(sketch, "E421", {"start": v(-438.18, -19.88) * mm, "end": v(-438.18, -11.55) * mm});
            skLineSegment(sketch, "E422", {"start": v(-438.18, -19.88) * mm, "end": v(-441.35, -19.88) * mm});
            skLineSegment(sketch, "E423", {"start": v(-441.35, -28.5) * mm, "end": v(-441.35, -19.88) * mm});
            skLineSegment(sketch, "E424", {"start": v(-438.18, -28.5) * mm, "end": v(-441.35, -28.5) * mm});
            skLineSegment(sketch, "E425", {"start": v(-438.18, -36.83) * mm, "end": v(-438.18, -28.5) * mm});
            skLineSegment(sketch, "E426", {"start": v(-438.18, -36.83) * mm, "end": v(-441.35, -36.83) * mm});
            skLineSegment(sketch, "E427", {"start": v(-441.35, -45.46) * mm, "end": v(-441.35, -36.83) * mm});
            skLineSegment(sketch, "E428", {"start": v(-438.18, -45.46) * mm, "end": v(-441.35, -45.46) * mm});
            skLineSegment(sketch, "E429", {"start": v(-438.18, -53.78) * mm, "end": v(-438.18, -45.46) * mm});
            skLineSegment(sketch, "E430", {"start": v(-438.18, -53.78) * mm, "end": v(-441.35, -53.78) * mm});
            skLineSegment(sketch, "E431", {"start": v(-441.35, -62.41) * mm, "end": v(-441.35, -53.78) * mm});
            skLineSegment(sketch, "E432", {"start": v(-438.18, -62.41) * mm, "end": v(-441.35, -62.41) * mm});
            skLineSegment(sketch, "E433", {"start": v(-438.18, -70.74) * mm, "end": v(-438.18, -62.41) * mm});
            skLineSegment(sketch, "E434", {"start": v(-438.18, -70.74) * mm, "end": v(-441.35, -70.74) * mm});
            skLineSegment(sketch, "E435", {"start": v(-441.35, -79.37) * mm, "end": v(-441.35, -70.74) * mm});
            skLineSegment(sketch, "E436", {"start": v(-438.18, -79.37) * mm, "end": v(-441.35, -79.37) * mm});
            skLineSegment(sketch, "E437", {"start": v(-438.18, -87.7) * mm, "end": v(-438.18, -79.37) * mm});
            skLineSegment(sketch, "E438", {"start": v(-438.18, -87.7) * mm, "end": v(-441.35, -87.7) * mm});
            skLineSegment(sketch, "E439", {"start": v(-441.35, -96.32) * mm, "end": v(-441.35, -87.7) * mm});
            skLineSegment(sketch, "E440", {"start": v(-438.18, -104.64) * mm, "end": v(-438.18, -96.32) * mm});
            skLineSegment(sketch, "E441", {"start": v(-438.18, -104.64) * mm, "end": v(-441.35, -104.64) * mm});
            skLineSegment(sketch, "E442", {"start": v(-441.35, -113.27) * mm, "end": v(-441.35, -104.64) * mm});
            skLineSegment(sketch, "E443", {"start": v(-438.18, -113.27) * mm, "end": v(-441.35, -113.27) * mm});
            skLineSegment(sketch, "E444", {"start": v(-438.18, -118.5) * mm, "end": v(-438.18, -113.27) * mm});
            skLineSegment(sketch, "E445", {"start": v(312.85, 2.3) * mm, "end": v(317.63, 2.3) * mm});
            skLineSegment(sketch, "E446", {"start": v(312.85, 5.48) * mm, "end": v(312.85, 2.3) * mm});
            skLineSegment(sketch, "E447", {"start": v(304.68, 5.48) * mm, "end": v(312.85, 5.48) * mm});
            skLineSegment(sketch, "E448", {"start": v(304.68, 5.48) * mm, "end": v(304.68, 2.3) * mm});
            skLineSegment(sketch, "E449", {"start": v(296.8, 2.3) * mm, "end": v(304.68, 2.3) * mm});
            skLineSegment(sketch, "E450", {"start": v(296.8, 5.48) * mm, "end": v(296.8, 2.3) * mm});
            skLineSegment(sketch, "E451", {"start": v(288.63, 5.48) * mm, "end": v(296.8, 5.48) * mm});
            skLineSegment(sketch, "E452", {"start": v(288.63, 5.48) * mm, "end": v(288.63, 2.3) * mm});
            skLineSegment(sketch, "E453", {"start": v(280.76, 2.3) * mm, "end": v(288.63, 2.3) * mm});
            skLineSegment(sketch, "E454", {"start": v(280.76, 5.48) * mm, "end": v(280.76, 2.3) * mm});
            skLineSegment(sketch, "E455", {"start": v(272.59, 5.48) * mm, "end": v(280.76, 5.48) * mm});
            skLineSegment(sketch, "E456", {"start": v(272.59, 5.48) * mm, "end": v(272.59, 2.3) * mm});
            skLineSegment(sketch, "E457", {"start": v(264.72, 2.3) * mm, "end": v(272.59, 2.3) * mm});
            skLineSegment(sketch, "E458", {"start": v(264.72, 5.48) * mm, "end": v(264.72, 2.3) * mm});
            skLineSegment(sketch, "E459", {"start": v(256.54, 5.48) * mm, "end": v(264.72, 5.48) * mm});
            skLineSegment(sketch, "E460", {"start": v(256.54, 5.48) * mm, "end": v(256.54, 2.3) * mm});
            skLineSegment(sketch, "E461", {"start": v(248.67, 2.3) * mm, "end": v(256.54, 2.3) * mm});
            skLineSegment(sketch, "E462", {"start": v(248.67, 5.48) * mm, "end": v(248.67, 2.3) * mm});
            skLineSegment(sketch, "E463", {"start": v(240.5, 5.48) * mm, "end": v(248.67, 5.48) * mm});
            skLineSegment(sketch, "E464", {"start": v(240.5, 5.48) * mm, "end": v(240.5, 2.3) * mm});
            skLineSegment(sketch, "E465", {"start": v(232.63, 2.3) * mm, "end": v(240.5, 2.3) * mm});
            skLineSegment(sketch, "E466", {"start": v(232.63, 5.48) * mm, "end": v(232.63, 2.3) * mm});
            skLineSegment(sketch, "E467", {"start": v(224.45, 5.48) * mm, "end": v(232.63, 5.48) * mm});
            skLineSegment(sketch, "E468", {"start": v(224.45, 5.48) * mm, "end": v(224.45, 2.3) * mm});
            skLineSegment(sketch, "E469", {"start": v(216.58, 2.3) * mm, "end": v(224.45, 2.3) * mm});
            skLineSegment(sketch, "E470", {"start": v(216.58, 5.48) * mm, "end": v(216.58, 2.3) * mm});
            skLineSegment(sketch, "E471", {"start": v(208.4, 5.48) * mm, "end": v(216.58, 5.48) * mm});
            skLineSegment(sketch, "E472", {"start": v(208.4, 5.48) * mm, "end": v(208.4, 2.3) * mm});
            skLineSegment(sketch, "E473", {"start": v(200.54, 2.3) * mm, "end": v(208.4, 2.3) * mm});
            skLineSegment(sketch, "E474", {"start": v(200.54, 5.48) * mm, "end": v(200.54, 2.3) * mm});
            skLineSegment(sketch, "E475", {"start": v(192.36, 5.48) * mm, "end": v(200.54, 5.48) * mm});
            skLineSegment(sketch, "E476", {"start": v(192.36, 5.48) * mm, "end": v(192.36, 2.3) * mm});
            skLineSegment(sketch, "E477", {"start": v(184.5, 2.3) * mm, "end": v(192.36, 2.3) * mm});
            skLineSegment(sketch, "E478", {"start": v(184.5, 5.48) * mm, "end": v(184.5, 2.3) * mm});
            skLineSegment(sketch, "E479", {"start": v(176.32, 5.48) * mm, "end": v(184.5, 5.48) * mm});
            skLineSegment(sketch, "E480", {"start": v(176.32, 5.48) * mm, "end": v(176.32, 2.3) * mm});
            skLineSegment(sketch, "E481", {"start": v(168.45, 2.3) * mm, "end": v(176.32, 2.3) * mm});
            skLineSegment(sketch, "E482", {"start": v(168.45, 5.48) * mm, "end": v(168.45, 2.3) * mm});
            skLineSegment(sketch, "E483", {"start": v(160.27, 5.48) * mm, "end": v(168.45, 5.48) * mm});
            skLineSegment(sketch, "E484", {"start": v(160.27, 5.48) * mm, "end": v(160.27, 2.3) * mm});
            skLineSegment(sketch, "E485", {"start": v(152.4, 2.3) * mm, "end": v(160.27, 2.3) * mm});
            skLineSegment(sketch, "E486", {"start": v(152.4, 5.48) * mm, "end": v(152.4, 2.3) * mm});
            skLineSegment(sketch, "E487", {"start": v(144.23, 5.48) * mm, "end": v(152.4, 5.48) * mm});
            skLineSegment(sketch, "E488", {"start": v(144.23, 5.48) * mm, "end": v(144.23, 2.3) * mm});
            skLineSegment(sketch, "E489", {"start": v(136.36, 2.3) * mm, "end": v(144.23, 2.3) * mm});
            skLineSegment(sketch, "E490", {"start": v(136.36, 5.48) * mm, "end": v(136.36, 2.3) * mm});
            skLineSegment(sketch, "E491", {"start": v(128.18, 5.48) * mm, "end": v(136.36, 5.48) * mm});
            skLineSegment(sketch, "E492", {"start": v(128.18, 5.48) * mm, "end": v(128.18, 2.3) * mm});
            skLineSegment(sketch, "E493", {"start": v(120.3, 2.3) * mm, "end": v(128.18, 2.3) * mm});
            skLineSegment(sketch, "E494", {"start": v(120.3, 5.48) * mm, "end": v(120.3, 2.3) * mm});
            skLineSegment(sketch, "E495", {"start": v(112.13, 5.48) * mm, "end": v(120.3, 5.48) * mm});
            skLineSegment(sketch, "E496", {"start": v(112.13, 5.48) * mm, "end": v(112.13, 2.3) * mm});
            skLineSegment(sketch, "E497", {"start": v(104.26, 2.3) * mm, "end": v(112.13, 2.3) * mm});
            skLineSegment(sketch, "E498", {"start": v(104.26, 5.48) * mm, "end": v(104.26, 2.3) * mm});
            skLineSegment(sketch, "E499", {"start": v(96.09, 5.48) * mm, "end": v(104.26, 5.48) * mm});
            skLineSegment(sketch, "E500", {"start": v(96.09, 5.48) * mm, "end": v(96.09, 2.3) * mm});
            skLineSegment(sketch, "E501", {"start": v(88.22, 2.3) * mm, "end": v(96.09, 2.3) * mm});
            skLineSegment(sketch, "E502", {"start": v(88.22, 5.48) * mm, "end": v(88.22, 2.3) * mm});
            skLineSegment(sketch, "E503", {"start": v(80.04, 5.48) * mm, "end": v(88.22, 5.48) * mm});
            skLineSegment(sketch, "E504", {"start": v(80.04, 5.48) * mm, "end": v(80.04, 2.3) * mm});
            skLineSegment(sketch, "E505", {"start": v(72.17, 2.3) * mm, "end": v(80.04, 2.3) * mm});
            skLineSegment(sketch, "E506", {"start": v(72.17, 5.48) * mm, "end": v(72.17, 2.3) * mm});
            skLineSegment(sketch, "E507", {"start": v(64, 5.48) * mm, "end": v(72.17, 5.48) * mm});
            skLineSegment(sketch, "E508", {"start": v(64, 5.48) * mm, "end": v(64, 2.3) * mm});
            skLineSegment(sketch, "E509", {"start": v(56.13, 2.3) * mm, "end": v(64, 2.3) * mm});
            skLineSegment(sketch, "E510", {"start": v(56.13, 5.48) * mm, "end": v(56.13, 2.3) * mm});
            skLineSegment(sketch, "E511", {"start": v(47.95, 5.48) * mm, "end": v(56.13, 5.48) * mm});
            skLineSegment(sketch, "E512", {"start": v(47.95, 5.48) * mm, "end": v(47.95, 2.3) * mm});
            skLineSegment(sketch, "E513", {"start": v(40.08, 2.3) * mm, "end": v(47.95, 2.3) * mm});
            skLineSegment(sketch, "E514", {"start": v(40.08, 5.48) * mm, "end": v(40.08, 2.3) * mm});
            skLineSegment(sketch, "E515", {"start": v(31.9, 5.48) * mm, "end": v(40.08, 5.48) * mm});
            skLineSegment(sketch, "E516", {"start": v(31.9, 5.48) * mm, "end": v(31.9, 2.3) * mm});
            skLineSegment(sketch, "E517", {"start": v(24.04, 2.3) * mm, "end": v(31.9, 2.3) * mm});
            skLineSegment(sketch, "E518", {"start": v(24.04, 5.48) * mm, "end": v(24.04, 2.3) * mm});
            skLineSegment(sketch, "E519", {"start": v(15.86, 5.48) * mm, "end": v(24.04, 5.48) * mm});
            skLineSegment(sketch, "E520", {"start": v(15.86, 5.48) * mm, "end": v(15.86, 2.3) * mm});
            skLineSegment(sketch, "E521", {"start": v(8, 2.3) * mm, "end": v(15.86, 2.3) * mm});
            skLineSegment(sketch, "E522", {"start": v(8, 5.48) * mm, "end": v(8, 2.3) * mm});
            skLineSegment(sketch, "E523", {"start": v(-0.18, 5.48) * mm, "end": v(8, 5.48) * mm});
            skLineSegment(sketch, "E524", {"start": v(-0.18, 5.48) * mm, "end": v(-0.18, 2.3) * mm});
            skLineSegment(sketch, "E525", {"start": v(-8.05, 2.3) * mm, "end": v(-0.18, 2.3) * mm});
            skLineSegment(sketch, "E526", {"start": v(-8.05, 5.48) * mm, "end": v(-8.05, 2.3) * mm});
            skLineSegment(sketch, "E527", {"start": v(-16.23, 5.48) * mm, "end": v(-8.05, 5.48) * mm});
            skLineSegment(sketch, "E528", {"start": v(-16.23, 5.48) * mm, "end": v(-16.23, 2.3) * mm});
            skLineSegment(sketch, "E529", {"start": v(-24.1, 2.3) * mm, "end": v(-16.23, 2.3) * mm});
            skLineSegment(sketch, "E530", {"start": v(-24.1, 5.48) * mm, "end": v(-24.1, 2.3) * mm});
            skLineSegment(sketch, "E531", {"start": v(-32.27, 5.48) * mm, "end": v(-24.1, 5.48) * mm});
            skLineSegment(sketch, "E532", {"start": v(-32.27, 5.48) * mm, "end": v(-32.27, 2.3) * mm});
            skLineSegment(sketch, "E533", {"start": v(-40.14, 2.3) * mm, "end": v(-32.27, 2.3) * mm});
            skLineSegment(sketch, "E534", {"start": v(-40.14, 5.48) * mm, "end": v(-40.14, 2.3) * mm});
            skLineSegment(sketch, "E535", {"start": v(-48.32, 5.48) * mm, "end": v(-40.14, 5.48) * mm});
            skLineSegment(sketch, "E536", {"start": v(-48.32, 5.48) * mm, "end": v(-48.32, 2.3) * mm});
            skLineSegment(sketch, "E537", {"start": v(-56.19, 2.3) * mm, "end": v(-48.32, 2.3) * mm});
            skLineSegment(sketch, "E538", {"start": v(-56.19, 5.48) * mm, "end": v(-56.19, 2.3) * mm});
            skLineSegment(sketch, "E539", {"start": v(-64.36, 5.48) * mm, "end": v(-56.19, 5.48) * mm});
            skLineSegment(sketch, "E540", {"start": v(-64.36, 5.48) * mm, "end": v(-64.36, 2.3) * mm});
            skLineSegment(sketch, "E541", {"start": v(-72.23, 2.3) * mm, "end": v(-64.36, 2.3) * mm});
            skLineSegment(sketch, "E542", {"start": v(-72.23, 5.48) * mm, "end": v(-72.23, 2.3) * mm});
            skLineSegment(sketch, "E543", {"start": v(-80.4, 5.48) * mm, "end": v(-72.23, 5.48) * mm});
            skLineSegment(sketch, "E544", {"start": v(-80.4, 5.48) * mm, "end": v(-80.4, 2.3) * mm});
            skLineSegment(sketch, "E545", {"start": v(-88.28, 2.3) * mm, "end": v(-80.4, 2.3) * mm});
            skLineSegment(sketch, "E546", {"start": v(-88.28, 5.48) * mm, "end": v(-88.28, 2.3) * mm});
            skLineSegment(sketch, "E547", {"start": v(-96.45, 5.48) * mm, "end": v(-88.28, 5.48) * mm});
            skLineSegment(sketch, "E548", {"start": v(-96.45, 5.48) * mm, "end": v(-96.45, 2.3) * mm});
            skLineSegment(sketch, "E549", {"start": v(-104.32, 2.3) * mm, "end": v(-96.45, 2.3) * mm});
            skLineSegment(sketch, "E550", {"start": v(-104.32, 5.48) * mm, "end": v(-104.32, 2.3) * mm});
            skLineSegment(sketch, "E551", {"start": v(-112.5, 5.48) * mm, "end": v(-104.32, 5.48) * mm});
            skLineSegment(sketch, "E552", {"start": v(-112.5, 5.48) * mm, "end": v(-112.5, 2.3) * mm});
            skLineSegment(sketch, "E553", {"start": v(-120.37, 2.3) * mm, "end": v(-112.5, 2.3) * mm});
            skLineSegment(sketch, "E554", {"start": v(-120.37, 5.48) * mm, "end": v(-120.37, 2.3) * mm});
            skLineSegment(sketch, "E555", {"start": v(-128.54, 5.48) * mm, "end": v(-120.37, 5.48) * mm});
            skLineSegment(sketch, "E556", {"start": v(-128.54, 5.48) * mm, "end": v(-128.54, 2.3) * mm});
            skLineSegment(sketch, "E557", {"start": v(-136.42, 2.3) * mm, "end": v(-128.54, 2.3) * mm});
            skLineSegment(sketch, "E558", {"start": v(-136.42, 5.48) * mm, "end": v(-136.42, 2.3) * mm});
            skLineSegment(sketch, "E559", {"start": v(-144.6, 5.48) * mm, "end": v(-136.42, 5.48) * mm});
            skLineSegment(sketch, "E560", {"start": v(-144.6, 5.48) * mm, "end": v(-144.6, 2.3) * mm});
            skLineSegment(sketch, "E561", {"start": v(-152.46, 2.3) * mm, "end": v(-144.6, 2.3) * mm});
            skLineSegment(sketch, "E562", {"start": v(-152.46, 5.48) * mm, "end": v(-152.46, 2.3) * mm});
            skLineSegment(sketch, "E563", {"start": v(-160.64, 5.48) * mm, "end": v(-152.46, 5.48) * mm});
            skLineSegment(sketch, "E564", {"start": v(-160.64, 5.48) * mm, "end": v(-160.64, 2.3) * mm});
            skLineSegment(sketch, "E565", {"start": v(-168.5, 2.3) * mm, "end": v(-160.64, 2.3) * mm});
            skLineSegment(sketch, "E566", {"start": v(-168.5, 5.48) * mm, "end": v(-168.5, 2.3) * mm});
            skLineSegment(sketch, "E567", {"start": v(-176.68, 5.48) * mm, "end": v(-168.5, 5.48) * mm});
            skLineSegment(sketch, "E568", {"start": v(-176.68, 5.48) * mm, "end": v(-176.68, 2.3) * mm});
            skLineSegment(sketch, "E569", {"start": v(-184.55, 2.3) * mm, "end": v(-176.68, 2.3) * mm});
            skLineSegment(sketch, "E570", {"start": v(-184.55, 5.48) * mm, "end": v(-184.55, 2.3) * mm});
            skLineSegment(sketch, "E571", {"start": v(-192.73, 5.48) * mm, "end": v(-184.55, 5.48) * mm});
            skLineSegment(sketch, "E572", {"start": v(-192.73, 5.48) * mm, "end": v(-192.73, 2.3) * mm});
            skLineSegment(sketch, "E573", {"start": v(-200.6, 2.3) * mm, "end": v(-192.73, 2.3) * mm});
            skLineSegment(sketch, "E574", {"start": v(-200.6, 5.48) * mm, "end": v(-200.6, 2.3) * mm});
            skLineSegment(sketch, "E575", {"start": v(-208.77, 5.48) * mm, "end": v(-200.6, 5.48) * mm});
            skLineSegment(sketch, "E576", {"start": v(-208.77, 5.48) * mm, "end": v(-208.77, 2.3) * mm});
            skLineSegment(sketch, "E577", {"start": v(-216.64, 2.3) * mm, "end": v(-208.77, 2.3) * mm});
            skLineSegment(sketch, "E578", {"start": v(-216.64, 5.48) * mm, "end": v(-216.64, 2.3) * mm});
            skLineSegment(sketch, "E579", {"start": v(-224.82, 5.48) * mm, "end": v(-216.64, 5.48) * mm});
            skLineSegment(sketch, "E580", {"start": v(-224.82, 5.48) * mm, "end": v(-224.82, 2.3) * mm});
            skLineSegment(sketch, "E581", {"start": v(-232.69, 2.3) * mm, "end": v(-224.82, 2.3) * mm});
            skLineSegment(sketch, "E582", {"start": v(-232.69, 5.48) * mm, "end": v(-232.69, 2.3) * mm});
            skLineSegment(sketch, "E583", {"start": v(-240.86, 5.48) * mm, "end": v(-232.69, 5.48) * mm});
            skLineSegment(sketch, "E584", {"start": v(-240.86, 5.48) * mm, "end": v(-240.86, 2.3) * mm});
            skLineSegment(sketch, "E585", {"start": v(-248.73, 2.3) * mm, "end": v(-240.86, 2.3) * mm});
            skLineSegment(sketch, "E586", {"start": v(-248.73, 5.48) * mm, "end": v(-248.73, 2.3) * mm});
            skLineSegment(sketch, "E587", {"start": v(-256.9, 5.48) * mm, "end": v(-248.73, 5.48) * mm});
            skLineSegment(sketch, "E588", {"start": v(-256.9, 5.48) * mm, "end": v(-256.9, 2.3) * mm});
            skLineSegment(sketch, "E589", {"start": v(-264.78, 2.3) * mm, "end": v(-256.9, 2.3) * mm});
            skLineSegment(sketch, "E590", {"start": v(-264.78, 5.48) * mm, "end": v(-264.78, 2.3) * mm});
            skLineSegment(sketch, "E591", {"start": v(-272.95, 5.48) * mm, "end": v(-264.78, 5.48) * mm});
            skLineSegment(sketch, "E592", {"start": v(-272.95, 5.48) * mm, "end": v(-272.95, 2.3) * mm});
            skLineSegment(sketch, "E593", {"start": v(-280.82, 2.3) * mm, "end": v(-272.95, 2.3) * mm});
            skLineSegment(sketch, "E594", {"start": v(-280.82, 5.48) * mm, "end": v(-280.82, 2.3) * mm});
            skLineSegment(sketch, "E595", {"start": v(-289, 5.48) * mm, "end": v(-280.82, 5.48) * mm});
            skLineSegment(sketch, "E596", {"start": v(-289, 5.48) * mm, "end": v(-289, 2.3) * mm});
            skLineSegment(sketch, "E597", {"start": v(-296.87, 2.3) * mm, "end": v(-289, 2.3) * mm});
            skLineSegment(sketch, "E598", {"start": v(-296.87, 5.48) * mm, "end": v(-296.87, 2.3) * mm});
            skLineSegment(sketch, "E599", {"start": v(-305.04, 5.48) * mm, "end": v(-296.87, 5.48) * mm});
            skLineSegment(sketch, "E600", {"start": v(-305.04, 5.48) * mm, "end": v(-305.04, 2.3) * mm});
            skLineSegment(sketch, "E601", {"start": v(-312.91, 2.3) * mm, "end": v(-305.04, 2.3) * mm});
            skLineSegment(sketch, "E602", {"start": v(-312.91, 5.48) * mm, "end": v(-312.91, 2.3) * mm});
            skLineSegment(sketch, "E603", {"start": v(-321.09, 5.48) * mm, "end": v(-312.91, 5.48) * mm});
            skLineSegment(sketch, "E604", {"start": v(-321.09, 5.48) * mm, "end": v(-321.09, 2.3) * mm});
            skLineSegment(sketch, "E605", {"start": v(-328.96, 2.3) * mm, "end": v(-321.09, 2.3) * mm});
            skLineSegment(sketch, "E606", {"start": v(-328.96, 5.48) * mm, "end": v(-328.96, 2.3) * mm});
            skLineSegment(sketch, "E607", {"start": v(-337.13, 5.48) * mm, "end": v(-328.96, 5.48) * mm});
            skLineSegment(sketch, "E608", {"start": v(-337.13, 5.48) * mm, "end": v(-337.13, 2.3) * mm});
            skLineSegment(sketch, "E609", {"start": v(-345, 2.3) * mm, "end": v(-337.13, 2.3) * mm});
            skLineSegment(sketch, "E610", {"start": v(-345, 5.48) * mm, "end": v(-345, 2.3) * mm});
            skLineSegment(sketch, "E611", {"start": v(-353.18, 5.48) * mm, "end": v(-345, 5.48) * mm});
            skLineSegment(sketch, "E612", {"start": v(-353.18, 5.48) * mm, "end": v(-353.18, 2.3) * mm});
            skLineSegment(sketch, "E613", {"start": v(-361.05, 2.3) * mm, "end": v(-353.18, 2.3) * mm});
            skLineSegment(sketch, "E614", {"start": v(-361.05, 5.48) * mm, "end": v(-361.05, 2.3) * mm});
            skLineSegment(sketch, "E615", {"start": v(-369.22, 5.48) * mm, "end": v(-361.05, 5.48) * mm});
            skLineSegment(sketch, "E616", {"start": v(-369.22, 5.48) * mm, "end": v(-369.22, 2.3) * mm});
            skLineSegment(sketch, "E617", {"start": v(-377.1, 2.3) * mm, "end": v(-369.22, 2.3) * mm});
            skLineSegment(sketch, "E618", {"start": v(-377.1, 5.48) * mm, "end": v(-377.1, 2.3) * mm});
            skLineSegment(sketch, "E619", {"start": v(-385.27, 5.48) * mm, "end": v(-377.1, 5.48) * mm});
            skLineSegment(sketch, "E620", {"start": v(-385.27, 5.48) * mm, "end": v(-385.27, 2.3) * mm});
            skLineSegment(sketch, "E621", {"start": v(-393.14, 2.3) * mm, "end": v(-385.27, 2.3) * mm});
            skLineSegment(sketch, "E622", {"start": v(-393.14, 5.48) * mm, "end": v(-393.14, 2.3) * mm});
            skLineSegment(sketch, "E623", {"start": v(-401.32, 5.48) * mm, "end": v(-393.14, 5.48) * mm});
            skLineSegment(sketch, "E624", {"start": v(-401.32, 5.48) * mm, "end": v(-401.32, 2.3) * mm});
            skLineSegment(sketch, "E625", {"start": v(-409.19, 2.3) * mm, "end": v(-401.32, 2.3) * mm});
            skLineSegment(sketch, "E626", {"start": v(-409.19, 5.48) * mm, "end": v(-409.19, 2.3) * mm});
            skLineSegment(sketch, "E627", {"start": v(-417.36, 5.48) * mm, "end": v(-409.19, 5.48) * mm});
            skLineSegment(sketch, "E628", {"start": v(-417.36, 5.48) * mm, "end": v(-417.36, 2.3) * mm});
            skLineSegment(sketch, "E629", {"start": v(-425.23, 2.3) * mm, "end": v(-417.36, 2.3) * mm});
            skLineSegment(sketch, "E630", {"start": v(-425.23, 5.48) * mm, "end": v(-425.23, 2.3) * mm});
            skLineSegment(sketch, "E631", {"start": v(-433.4, 5.48) * mm, "end": v(-425.23, 5.48) * mm});
            skLineSegment(sketch, "E632", {"start": v(-433.4, 5.48) * mm, "end": v(-433.4, 2.3) * mm});
            skLineSegment(sketch, "E633", {"start": v(-438.18, 2.3) * mm, "end": v(-433.4, 2.3) * mm});
            skLineSegment(sketch, "E634", {"start": v(312.85, -118.5) * mm, "end": v(317.63, -118.5) * mm});
            skLineSegment(sketch, "E635", {"start": v(312.85, -118.5) * mm, "end": v(312.85, -121.67) * mm});
            skLineSegment(sketch, "E636", {"start": v(304.68, -121.67) * mm, "end": v(312.85, -121.67) * mm});
            skLineSegment(sketch, "E637", {"start": v(304.68, -118.5) * mm, "end": v(304.68, -121.67) * mm});
            skLineSegment(sketch, "E638", {"start": v(296.8, -118.5) * mm, "end": v(304.68, -118.5) * mm});
            skLineSegment(sketch, "E639", {"start": v(296.8, -118.5) * mm, "end": v(296.8, -121.67) * mm});
            skLineSegment(sketch, "E640", {"start": v(288.63, -121.67) * mm, "end": v(296.8, -121.67) * mm});
            skLineSegment(sketch, "E641", {"start": v(288.63, -118.5) * mm, "end": v(288.63, -121.67) * mm});
            skLineSegment(sketch, "E642", {"start": v(280.76, -118.5) * mm, "end": v(288.63, -118.5) * mm});
            skLineSegment(sketch, "E643", {"start": v(280.76, -118.5) * mm, "end": v(280.76, -121.67) * mm});
            skLineSegment(sketch, "E644", {"start": v(272.59, -121.67) * mm, "end": v(280.76, -121.67) * mm});
            skLineSegment(sketch, "E645", {"start": v(272.59, -118.5) * mm, "end": v(272.59, -121.67) * mm});
            skLineSegment(sketch, "E646", {"start": v(264.72, -118.5) * mm, "end": v(272.59, -118.5) * mm});
            skLineSegment(sketch, "E647", {"start": v(264.72, -118.5) * mm, "end": v(264.72, -121.67) * mm});
            skLineSegment(sketch, "E648", {"start": v(256.54, -121.67) * mm, "end": v(264.72, -121.67) * mm});
            skLineSegment(sketch, "E649", {"start": v(256.54, -118.5) * mm, "end": v(256.54, -121.67) * mm});
            skLineSegment(sketch, "E650", {"start": v(248.67, -118.5) * mm, "end": v(256.54, -118.5) * mm});
            skLineSegment(sketch, "E651", {"start": v(248.67, -118.5) * mm, "end": v(248.67, -121.67) * mm});
            skLineSegment(sketch, "E652", {"start": v(240.5, -121.67) * mm, "end": v(248.67, -121.67) * mm});
            skLineSegment(sketch, "E653", {"start": v(240.5, -118.5) * mm, "end": v(240.5, -121.67) * mm});
            skLineSegment(sketch, "E654", {"start": v(232.63, -118.5) * mm, "end": v(240.5, -118.5) * mm});
            skLineSegment(sketch, "E655", {"start": v(232.63, -118.5) * mm, "end": v(232.63, -121.67) * mm});
            skLineSegment(sketch, "E656", {"start": v(224.45, -121.67) * mm, "end": v(232.63, -121.67) * mm});
            skLineSegment(sketch, "E657", {"start": v(224.45, -118.5) * mm, "end": v(224.45, -121.67) * mm});
            skLineSegment(sketch, "E658", {"start": v(216.58, -118.5) * mm, "end": v(224.45, -118.5) * mm});
            skLineSegment(sketch, "E659", {"start": v(216.58, -118.5) * mm, "end": v(216.58, -121.67) * mm});
            skLineSegment(sketch, "E660", {"start": v(208.4, -121.67) * mm, "end": v(216.58, -121.67) * mm});
            skLineSegment(sketch, "E661", {"start": v(208.4, -118.5) * mm, "end": v(208.4, -121.67) * mm});
            skLineSegment(sketch, "E662", {"start": v(200.54, -118.5) * mm, "end": v(208.4, -118.5) * mm});
            skLineSegment(sketch, "E663", {"start": v(200.54, -118.5) * mm, "end": v(200.54, -121.67) * mm});
            skLineSegment(sketch, "E664", {"start": v(192.36, -121.67) * mm, "end": v(200.54, -121.67) * mm});
            skLineSegment(sketch, "E665", {"start": v(192.36, -118.5) * mm, "end": v(192.36, -121.67) * mm});
            skLineSegment(sketch, "E666", {"start": v(184.5, -118.5) * mm, "end": v(192.36, -118.5) * mm});
            skLineSegment(sketch, "E667", {"start": v(184.5, -118.5) * mm, "end": v(184.5, -121.67) * mm});
            skLineSegment(sketch, "E668", {"start": v(176.32, -121.67) * mm, "end": v(184.5, -121.67) * mm});
            skLineSegment(sketch, "E669", {"start": v(176.32, -118.5) * mm, "end": v(176.32, -121.67) * mm});
            skLineSegment(sketch, "E670", {"start": v(168.45, -118.5) * mm, "end": v(176.32, -118.5) * mm});
            skLineSegment(sketch, "E671", {"start": v(168.45, -118.5) * mm, "end": v(168.45, -121.67) * mm});
            skLineSegment(sketch, "E672", {"start": v(160.27, -121.67) * mm, "end": v(168.45, -121.67) * mm});
            skLineSegment(sketch, "E673", {"start": v(160.27, -118.5) * mm, "end": v(160.27, -121.67) * mm});
            skLineSegment(sketch, "E674", {"start": v(152.4, -118.5) * mm, "end": v(160.27, -118.5) * mm});
            skLineSegment(sketch, "E675", {"start": v(152.4, -118.5) * mm, "end": v(152.4, -121.67) * mm});
            skLineSegment(sketch, "E676", {"start": v(144.23, -121.67) * mm, "end": v(152.4, -121.67) * mm});
            skLineSegment(sketch, "E677", {"start": v(144.23, -118.5) * mm, "end": v(144.23, -121.67) * mm});
            skLineSegment(sketch, "E678", {"start": v(136.36, -118.5) * mm, "end": v(144.23, -118.5) * mm});
            skLineSegment(sketch, "E679", {"start": v(136.36, -118.5) * mm, "end": v(136.36, -121.67) * mm});
            skLineSegment(sketch, "E680", {"start": v(128.18, -121.67) * mm, "end": v(136.36, -121.67) * mm});
            skLineSegment(sketch, "E681", {"start": v(128.18, -118.5) * mm, "end": v(128.18, -121.67) * mm});
            skLineSegment(sketch, "E682", {"start": v(120.3, -118.5) * mm, "end": v(128.18, -118.5) * mm});
            skLineSegment(sketch, "E683", {"start": v(120.3, -118.5) * mm, "end": v(120.3, -121.67) * mm});
            skLineSegment(sketch, "E684", {"start": v(112.13, -121.67) * mm, "end": v(120.3, -121.67) * mm});
            skLineSegment(sketch, "E685", {"start": v(112.13, -118.5) * mm, "end": v(112.13, -121.67) * mm});
            skLineSegment(sketch, "E686", {"start": v(104.26, -118.5) * mm, "end": v(112.13, -118.5) * mm});
            skLineSegment(sketch, "E687", {"start": v(104.26, -118.5) * mm, "end": v(104.26, -121.67) * mm});
            skLineSegment(sketch, "E688", {"start": v(96.09, -121.67) * mm, "end": v(104.26, -121.67) * mm});
            skLineSegment(sketch, "E689", {"start": v(96.09, -118.5) * mm, "end": v(96.09, -121.67) * mm});
            skLineSegment(sketch, "E690", {"start": v(88.22, -118.5) * mm, "end": v(96.09, -118.5) * mm});
            skLineSegment(sketch, "E691", {"start": v(88.22, -118.5) * mm, "end": v(88.22, -121.67) * mm});
            skLineSegment(sketch, "E692", {"start": v(80.04, -121.67) * mm, "end": v(88.22, -121.67) * mm});
            skLineSegment(sketch, "E693", {"start": v(80.04, -118.5) * mm, "end": v(80.04, -121.67) * mm});
            skLineSegment(sketch, "E694", {"start": v(72.17, -118.5) * mm, "end": v(80.04, -118.5) * mm});
            skLineSegment(sketch, "E695", {"start": v(72.17, -118.5) * mm, "end": v(72.17, -121.67) * mm});
            skLineSegment(sketch, "E696", {"start": v(64, -121.67) * mm, "end": v(72.17, -121.67) * mm});
            skLineSegment(sketch, "E697", {"start": v(64, -118.5) * mm, "end": v(64, -121.67) * mm});
            skLineSegment(sketch, "E698", {"start": v(56.13, -118.5) * mm, "end": v(64, -118.5) * mm});
            skLineSegment(sketch, "E699", {"start": v(56.13, -118.5) * mm, "end": v(56.13, -121.67) * mm});
            skLineSegment(sketch, "E700", {"start": v(47.95, -121.67) * mm, "end": v(56.13, -121.67) * mm});
            skLineSegment(sketch, "E701", {"start": v(47.95, -118.5) * mm, "end": v(47.95, -121.67) * mm});
            skLineSegment(sketch, "E702", {"start": v(40.08, -118.5) * mm, "end": v(47.95, -118.5) * mm});
            skLineSegment(sketch, "E703", {"start": v(40.08, -118.5) * mm, "end": v(40.08, -121.67) * mm});
            skLineSegment(sketch, "E704", {"start": v(31.9, -121.67) * mm, "end": v(40.08, -121.67) * mm});
            skLineSegment(sketch, "E705", {"start": v(31.9, -118.5) * mm, "end": v(31.9, -121.67) * mm});
            skLineSegment(sketch, "E706", {"start": v(24.04, -118.5) * mm, "end": v(31.9, -118.5) * mm});
            skLineSegment(sketch, "E707", {"start": v(24.04, -118.5) * mm, "end": v(24.04, -121.67) * mm});
            skLineSegment(sketch, "E708", {"start": v(15.86, -121.67) * mm, "end": v(24.04, -121.67) * mm});
            skLineSegment(sketch, "E709", {"start": v(15.86, -118.5) * mm, "end": v(15.86, -121.67) * mm});
            skLineSegment(sketch, "E710", {"start": v(8, -118.5) * mm, "end": v(15.86, -118.5) * mm});
            skLineSegment(sketch, "E711", {"start": v(8, -118.5) * mm, "end": v(8, -121.67) * mm});
            skLineSegment(sketch, "E712", {"start": v(-0.18, -121.67) * mm, "end": v(8, -121.67) * mm});
            skLineSegment(sketch, "E713", {"start": v(-0.18, -118.5) * mm, "end": v(-0.18, -121.67) * mm});
            skLineSegment(sketch, "E714", {"start": v(-8.05, -118.5) * mm, "end": v(-0.18, -118.5) * mm});
            skLineSegment(sketch, "E715", {"start": v(-8.05, -118.5) * mm, "end": v(-8.05, -121.67) * mm});
            skLineSegment(sketch, "E716", {"start": v(-16.23, -121.67) * mm, "end": v(-8.05, -121.67) * mm});
            skLineSegment(sketch, "E717", {"start": v(-16.23, -118.5) * mm, "end": v(-16.23, -121.67) * mm});
            skLineSegment(sketch, "E718", {"start": v(-24.1, -118.5) * mm, "end": v(-16.23, -118.5) * mm});
            skLineSegment(sketch, "E719", {"start": v(-24.1, -118.5) * mm, "end": v(-24.1, -121.67) * mm});
            skLineSegment(sketch, "E720", {"start": v(-32.27, -121.67) * mm, "end": v(-24.1, -121.67) * mm});
            skLineSegment(sketch, "E721", {"start": v(-32.27, -118.5) * mm, "end": v(-32.27, -121.67) * mm});
            skLineSegment(sketch, "E722", {"start": v(-40.14, -118.5) * mm, "end": v(-32.27, -118.5) * mm});
            skLineSegment(sketch, "E723", {"start": v(-40.14, -118.5) * mm, "end": v(-40.14, -121.67) * mm});
            skLineSegment(sketch, "E724", {"start": v(-48.32, -121.67) * mm, "end": v(-40.14, -121.67) * mm});
            skLineSegment(sketch, "E725", {"start": v(-48.32, -118.5) * mm, "end": v(-48.32, -121.67) * mm});
            skLineSegment(sketch, "E726", {"start": v(-56.19, -118.5) * mm, "end": v(-48.32, -118.5) * mm});
            skLineSegment(sketch, "E727", {"start": v(-56.19, -118.5) * mm, "end": v(-56.19, -121.67) * mm});
            skLineSegment(sketch, "E728", {"start": v(-64.36, -121.67) * mm, "end": v(-56.19, -121.67) * mm});
            skLineSegment(sketch, "E729", {"start": v(-64.36, -118.5) * mm, "end": v(-64.36, -121.67) * mm});
            skLineSegment(sketch, "E730", {"start": v(-72.23, -118.5) * mm, "end": v(-64.36, -118.5) * mm});
            skLineSegment(sketch, "E731", {"start": v(-72.23, -118.5) * mm, "end": v(-72.23, -121.67) * mm});
            skLineSegment(sketch, "E732", {"start": v(-80.4, -121.67) * mm, "end": v(-72.23, -121.67) * mm});
            skLineSegment(sketch, "E733", {"start": v(-80.4, -118.5) * mm, "end": v(-80.4, -121.67) * mm});
            skLineSegment(sketch, "E734", {"start": v(-88.28, -118.5) * mm, "end": v(-80.4, -118.5) * mm});
            skLineSegment(sketch, "E735", {"start": v(-88.28, -118.5) * mm, "end": v(-88.28, -121.67) * mm});
            skLineSegment(sketch, "E736", {"start": v(-96.45, -121.67) * mm, "end": v(-88.28, -121.67) * mm});
            skLineSegment(sketch, "E737", {"start": v(-96.45, -118.5) * mm, "end": v(-96.45, -121.67) * mm});
            skLineSegment(sketch, "E738", {"start": v(-104.32, -118.5) * mm, "end": v(-96.45, -118.5) * mm});
            skLineSegment(sketch, "E739", {"start": v(-104.32, -118.5) * mm, "end": v(-104.32, -121.67) * mm});
            skLineSegment(sketch, "E740", {"start": v(-112.5, -121.67) * mm, "end": v(-104.32, -121.67) * mm});
            skLineSegment(sketch, "E741", {"start": v(-112.5, -118.5) * mm, "end": v(-112.5, -121.67) * mm});
            skLineSegment(sketch, "E742", {"start": v(-120.37, -118.5) * mm, "end": v(-112.5, -118.5) * mm});
            skLineSegment(sketch, "E743", {"start": v(-120.37, -118.5) * mm, "end": v(-120.37, -121.67) * mm});
            skLineSegment(sketch, "E744", {"start": v(-128.54, -121.67) * mm, "end": v(-120.37, -121.67) * mm});
            skLineSegment(sketch, "E745", {"start": v(-128.54, -118.5) * mm, "end": v(-128.54, -121.67) * mm});
            skLineSegment(sketch, "E746", {"start": v(-136.42, -118.5) * mm, "end": v(-128.54, -118.5) * mm});
            skLineSegment(sketch, "E747", {"start": v(-136.42, -118.5) * mm, "end": v(-136.42, -121.67) * mm});
            skLineSegment(sketch, "E748", {"start": v(-144.6, -121.67) * mm, "end": v(-136.42, -121.67) * mm});
            skLineSegment(sketch, "E749", {"start": v(-144.6, -118.5) * mm, "end": v(-144.6, -121.67) * mm});
            skLineSegment(sketch, "E750", {"start": v(-152.46, -118.5) * mm, "end": v(-144.6, -118.5) * mm});
            skLineSegment(sketch, "E751", {"start": v(-152.46, -118.5) * mm, "end": v(-152.46, -121.67) * mm});
            skLineSegment(sketch, "E752", {"start": v(-160.64, -121.67) * mm, "end": v(-152.46, -121.67) * mm});
            skLineSegment(sketch, "E753", {"start": v(-160.64, -118.5) * mm, "end": v(-160.64, -121.67) * mm});
            skLineSegment(sketch, "E754", {"start": v(-168.5, -118.5) * mm, "end": v(-160.64, -118.5) * mm});
            skLineSegment(sketch, "E755", {"start": v(-168.5, -118.5) * mm, "end": v(-168.5, -121.67) * mm});
            skLineSegment(sketch, "E756", {"start": v(-176.68, -121.67) * mm, "end": v(-168.5, -121.67) * mm});
            skLineSegment(sketch, "E757", {"start": v(-176.68, -118.5) * mm, "end": v(-176.68, -121.67) * mm});
            skLineSegment(sketch, "E758", {"start": v(-184.55, -118.5) * mm, "end": v(-176.68, -118.5) * mm});
            skLineSegment(sketch, "E759", {"start": v(-184.55, -118.5) * mm, "end": v(-184.55, -121.67) * mm});
            skLineSegment(sketch, "E760", {"start": v(-192.73, -121.67) * mm, "end": v(-184.55, -121.67) * mm});
            skLineSegment(sketch, "E761", {"start": v(-192.73, -118.5) * mm, "end": v(-192.73, -121.67) * mm});
            skLineSegment(sketch, "E762", {"start": v(-200.6, -118.5) * mm, "end": v(-192.73, -118.5) * mm});
            skLineSegment(sketch, "E763", {"start": v(-200.6, -118.5) * mm, "end": v(-200.6, -121.67) * mm});
            skLineSegment(sketch, "E764", {"start": v(-208.77, -121.67) * mm, "end": v(-200.6, -121.67) * mm});
            skLineSegment(sketch, "E765", {"start": v(-208.77, -118.5) * mm, "end": v(-208.77, -121.67) * mm});
            skLineSegment(sketch, "E766", {"start": v(-216.64, -118.5) * mm, "end": v(-208.77, -118.5) * mm});
            skLineSegment(sketch, "E767", {"start": v(-216.64, -118.5) * mm, "end": v(-216.64, -121.67) * mm});
            skLineSegment(sketch, "E768", {"start": v(-224.82, -121.67) * mm, "end": v(-216.64, -121.67) * mm});
            skLineSegment(sketch, "E769", {"start": v(-224.82, -118.5) * mm, "end": v(-224.82, -121.67) * mm});
            skLineSegment(sketch, "E770", {"start": v(-232.69, -118.5) * mm, "end": v(-224.82, -118.5) * mm});
            skLineSegment(sketch, "E771", {"start": v(-232.69, -118.5) * mm, "end": v(-232.69, -121.67) * mm});
            skLineSegment(sketch, "E772", {"start": v(-240.86, -121.67) * mm, "end": v(-232.69, -121.67) * mm});
            skLineSegment(sketch, "E773", {"start": v(-240.86, -118.5) * mm, "end": v(-240.86, -121.67) * mm});
            skLineSegment(sketch, "E774", {"start": v(-248.73, -118.5) * mm, "end": v(-240.86, -118.5) * mm});
            skLineSegment(sketch, "E775", {"start": v(-248.73, -118.5) * mm, "end": v(-248.73, -121.67) * mm});
            skLineSegment(sketch, "E776", {"start": v(-256.9, -121.67) * mm, "end": v(-248.73, -121.67) * mm});
            skLineSegment(sketch, "E777", {"start": v(-256.9, -118.5) * mm, "end": v(-256.9, -121.67) * mm});
            skLineSegment(sketch, "E778", {"start": v(-264.78, -118.5) * mm, "end": v(-256.9, -118.5) * mm});
            skLineSegment(sketch, "E779", {"start": v(-264.78, -118.5) * mm, "end": v(-264.78, -121.67) * mm});
            skLineSegment(sketch, "E780", {"start": v(-272.95, -121.67) * mm, "end": v(-264.78, -121.67) * mm});
            skLineSegment(sketch, "E781", {"start": v(-272.95, -118.5) * mm, "end": v(-272.95, -121.67) * mm});
            skLineSegment(sketch, "E782", {"start": v(-280.82, -118.5) * mm, "end": v(-272.95, -118.5) * mm});
            skLineSegment(sketch, "E783", {"start": v(-280.82, -118.5) * mm, "end": v(-280.82, -121.67) * mm});
            skLineSegment(sketch, "E784", {"start": v(-289, -121.67) * mm, "end": v(-280.82, -121.67) * mm});
            skLineSegment(sketch, "E785", {"start": v(-289, -118.5) * mm, "end": v(-289, -121.67) * mm});
            skLineSegment(sketch, "E786", {"start": v(-296.87, -118.5) * mm, "end": v(-289, -118.5) * mm});
            skLineSegment(sketch, "E787", {"start": v(-296.87, -118.5) * mm, "end": v(-296.87, -121.67) * mm});
            skLineSegment(sketch, "E788", {"start": v(-305.04, -121.67) * mm, "end": v(-296.87, -121.67) * mm});
            skLineSegment(sketch, "E789", {"start": v(-305.04, -118.5) * mm, "end": v(-305.04, -121.67) * mm});
            skLineSegment(sketch, "E790", {"start": v(-312.91, -118.5) * mm, "end": v(-305.04, -118.5) * mm});
            skLineSegment(sketch, "E791", {"start": v(-312.91, -118.5) * mm, "end": v(-312.91, -121.67) * mm});
            skLineSegment(sketch, "E792", {"start": v(-321.09, -121.67) * mm, "end": v(-312.91, -121.67) * mm});
            skLineSegment(sketch, "E793", {"start": v(-321.09, -118.5) * mm, "end": v(-321.09, -121.67) * mm});
            skLineSegment(sketch, "E794", {"start": v(-328.96, -118.5) * mm, "end": v(-321.09, -118.5) * mm});
            skLineSegment(sketch, "E795", {"start": v(-328.96, -118.5) * mm, "end": v(-328.96, -121.67) * mm});
            skLineSegment(sketch, "E796", {"start": v(-337.13, -121.67) * mm, "end": v(-328.96, -121.67) * mm});
            skLineSegment(sketch, "E797", {"start": v(-337.13, -118.5) * mm, "end": v(-337.13, -121.67) * mm});
            skLineSegment(sketch, "E798", {"start": v(-345, -118.5) * mm, "end": v(-337.13, -118.5) * mm});
            skLineSegment(sketch, "E799", {"start": v(-345, -118.5) * mm, "end": v(-345, -121.67) * mm});
            skLineSegment(sketch, "E800", {"start": v(-353.18, -121.67) * mm, "end": v(-345, -121.67) * mm});
            skLineSegment(sketch, "E801", {"start": v(-353.18, -118.5) * mm, "end": v(-353.18, -121.67) * mm});
            skLineSegment(sketch, "E802", {"start": v(-361.05, -118.5) * mm, "end": v(-353.18, -118.5) * mm});
            skLineSegment(sketch, "E803", {"start": v(-361.05, -118.5) * mm, "end": v(-361.05, -121.67) * mm});
            skLineSegment(sketch, "E804", {"start": v(-369.22, -121.67) * mm, "end": v(-361.05, -121.67) * mm});
            skLineSegment(sketch, "E805", {"start": v(-369.22, -118.5) * mm, "end": v(-369.22, -121.67) * mm});
            skLineSegment(sketch, "E806", {"start": v(-377.1, -118.5) * mm, "end": v(-369.22, -118.5) * mm});
            skLineSegment(sketch, "E807", {"start": v(-377.1, -118.5) * mm, "end": v(-377.1, -121.67) * mm});
            skLineSegment(sketch, "E808", {"start": v(-385.27, -121.67) * mm, "end": v(-377.1, -121.67) * mm});
            skLineSegment(sketch, "E809", {"start": v(-385.27, -118.5) * mm, "end": v(-385.27, -121.67) * mm});
            skLineSegment(sketch, "E810", {"start": v(-393.14, -118.5) * mm, "end": v(-385.27, -118.5) * mm});
            skLineSegment(sketch, "E811", {"start": v(-393.14, -118.5) * mm, "end": v(-393.14, -121.67) * mm});
            skLineSegment(sketch, "E812", {"start": v(-401.32, -121.67) * mm, "end": v(-393.14, -121.67) * mm});
            skLineSegment(sketch, "E813", {"start": v(-401.32, -118.5) * mm, "end": v(-401.32, -121.67) * mm});
            skLineSegment(sketch, "E814", {"start": v(-409.19, -118.5) * mm, "end": v(-401.32, -118.5) * mm});
            skLineSegment(sketch, "E815", {"start": v(-409.19, -118.5) * mm, "end": v(-409.19, -121.67) * mm});
            skLineSegment(sketch, "E816", {"start": v(-417.36, -121.67) * mm, "end": v(-409.19, -121.67) * mm});
            skLineSegment(sketch, "E817", {"start": v(-417.36, -118.5) * mm, "end": v(-417.36, -121.67) * mm});
            skLineSegment(sketch, "E818", {"start": v(-425.23, -118.5) * mm, "end": v(-417.36, -118.5) * mm});
            skLineSegment(sketch, "E819", {"start": v(-425.23, -118.5) * mm, "end": v(-425.23, -121.67) * mm});
            skLineSegment(sketch, "E820", {"start": v(-433.4, -121.67) * mm, "end": v(-425.23, -121.67) * mm});
            skLineSegment(sketch, "E821", {"start": v(-433.4, -118.5) * mm, "end": v(-433.4, -121.67) * mm});
            skLineSegment(sketch, "E822", {"start": v(-438.18, -118.5) * mm, "end": v(-433.4, -118.5) * mm});
            skLineSegment(sketch, "E823", {"start": v(-438.18, -96.32) * mm, "end": v(-441.35, -96.32) * mm});
            skLineSegment(sketch, "E824", {"start": v(-438.18, -96.29) * mm, "end": v(-433.4, -96.29) * mm});
            skLineSegment(sketch, "E825", {"start": v(-433.4, -96.29) * mm, "end": v(-433.4, -99.46) * mm});
            skLineSegment(sketch, "E826", {"start": v(-425.5, -99.46) * mm, "end": v(-417.33, -99.46) * mm});
            skLineSegment(sketch, "E827", {"start": v(-425.23, -96.29) * mm, "end": v(-425.23, -99.46) * mm});
            skLineSegment(sketch, "E828", {"start": v(-425.23, -96.29) * mm, "end": v(-417.36, -96.29) * mm});
            skLineSegment(sketch, "E829", {"start": v(-417.36, -96.29) * mm, "end": v(-417.36, -99.46) * mm});
            skLineSegment(sketch, "E830", {"start": v(-409.46, -99.46) * mm, "end": v(-401.28, -99.46) * mm});
            skLineSegment(sketch, "E831", {"start": v(-409.19, -96.29) * mm, "end": v(-409.19, -99.46) * mm});
            skLineSegment(sketch, "E832", {"start": v(-409.19, -96.29) * mm, "end": v(-401.32, -96.29) * mm});
            skLineSegment(sketch, "E833", {"start": v(-401.32, -96.29) * mm, "end": v(-401.32, -99.46) * mm});
            skLineSegment(sketch, "E834", {"start": v(-393.41, -99.46) * mm, "end": v(-385.24, -99.46) * mm});
            skLineSegment(sketch, "E835", {"start": v(-393.14, -96.29) * mm, "end": v(-393.14, -99.46) * mm});
            skLineSegment(sketch, "E836", {"start": v(-393.14, -96.29) * mm, "end": v(-385.27, -96.29) * mm});
            skLineSegment(sketch, "E837", {"start": v(-385.27, -96.29) * mm, "end": v(-385.27, -99.46) * mm});
            skLineSegment(sketch, "E838", {"start": v(-377.37, -99.46) * mm, "end": v(-369.2, -99.46) * mm});
            skLineSegment(sketch, "E839", {"start": v(-377.1, -96.29) * mm, "end": v(-377.1, -99.46) * mm});
            skLineSegment(sketch, "E840", {"start": v(-377.1, -96.29) * mm, "end": v(-369.22, -96.29) * mm});
            skLineSegment(sketch, "E841", {"start": v(-369.22, -96.29) * mm, "end": v(-369.22, -99.46) * mm});
            skLineSegment(sketch, "E842", {"start": v(-361.32, -99.46) * mm, "end": v(-353.15, -99.46) * mm});
            skLineSegment(sketch, "E843", {"start": v(-361.05, -96.29) * mm, "end": v(-361.05, -99.46) * mm});
            skLineSegment(sketch, "E844", {"start": v(-361.05, -96.29) * mm, "end": v(-353.18, -96.29) * mm});
            skLineSegment(sketch, "E845", {"start": v(-353.18, -96.29) * mm, "end": v(-353.18, -99.46) * mm});
            skLineSegment(sketch, "E846", {"start": v(-345.28, -99.46) * mm, "end": v(-337.1, -99.46) * mm});
            skLineSegment(sketch, "E847", {"start": v(-345, -96.29) * mm, "end": v(-345, -99.46) * mm});
            skLineSegment(sketch, "E848", {"start": v(-345, -96.29) * mm, "end": v(-337.13, -96.29) * mm});
            skLineSegment(sketch, "E849", {"start": v(-337.13, -96.29) * mm, "end": v(-337.13, -99.46) * mm});
            skLineSegment(sketch, "E850", {"start": v(-329.23, -99.46) * mm, "end": v(-321.06, -99.46) * mm});
            skLineSegment(sketch, "E851", {"start": v(-328.96, -96.29) * mm, "end": v(-328.96, -99.46) * mm});
            skLineSegment(sketch, "E852", {"start": v(-328.96, -96.29) * mm, "end": v(-321.09, -96.29) * mm});
            skLineSegment(sketch, "E853", {"start": v(-321.09, -96.29) * mm, "end": v(-321.09, -99.46) * mm});
            skLineSegment(sketch, "E854", {"start": v(-313.19, -99.46) * mm, "end": v(-305.01, -99.46) * mm});
            skLineSegment(sketch, "E855", {"start": v(-312.91, -96.29) * mm, "end": v(-312.91, -99.46) * mm});
            skLineSegment(sketch, "E856", {"start": v(-312.91, -96.29) * mm, "end": v(-305.04, -96.29) * mm});
            skLineSegment(sketch, "E857", {"start": v(-305.04, -96.29) * mm, "end": v(-305.04, -99.46) * mm});
            skLineSegment(sketch, "E858", {"start": v(-297.14, -99.46) * mm, "end": v(-288.97, -99.46) * mm});
            skLineSegment(sketch, "E859", {"start": v(-296.87, -96.29) * mm, "end": v(-296.87, -99.46) * mm});
            skLineSegment(sketch, "E860", {"start": v(-296.87, -96.29) * mm, "end": v(-289, -96.29) * mm});
            skLineSegment(sketch, "E861", {"start": v(-289, -96.29) * mm, "end": v(-289, -99.46) * mm});
            skLineSegment(sketch, "E862", {"start": v(-281.1, -99.46) * mm, "end": v(-272.92, -99.46) * mm});
            skLineSegment(sketch, "E863", {"start": v(-280.82, -96.29) * mm, "end": v(-280.82, -99.46) * mm});
            skLineSegment(sketch, "E864", {"start": v(-280.82, -96.29) * mm, "end": v(-272.95, -96.29) * mm});
            skLineSegment(sketch, "E865", {"start": v(-272.95, -96.29) * mm, "end": v(-272.95, -99.46) * mm});
            skLineSegment(sketch, "E866", {"start": v(-265.05, -99.46) * mm, "end": v(-256.88, -99.46) * mm});
            skLineSegment(sketch, "E867", {"start": v(-264.78, -96.29) * mm, "end": v(-264.78, -99.46) * mm});
            skLineSegment(sketch, "E868", {"start": v(-264.78, -96.29) * mm, "end": v(-256.9, -96.29) * mm});
            skLineSegment(sketch, "E869", {"start": v(-256.9, -96.29) * mm, "end": v(-256.9, -99.46) * mm});
            skLineSegment(sketch, "E870", {"start": v(-249, -99.46) * mm, "end": v(-240.83, -99.46) * mm});
            skLineSegment(sketch, "E871", {"start": v(-248.73, -96.29) * mm, "end": v(-248.73, -99.46) * mm});
            skLineSegment(sketch, "E872", {"start": v(-248.73, -96.29) * mm, "end": v(-240.86, -96.29) * mm});
            skLineSegment(sketch, "E873", {"start": v(-240.86, -96.29) * mm, "end": v(-240.86, -99.46) * mm});
            skLineSegment(sketch, "E874", {"start": v(-232.96, -99.46) * mm, "end": v(-224.78, -99.46) * mm});
            skLineSegment(sketch, "E875", {"start": v(-232.69, -96.29) * mm, "end": v(-232.69, -99.46) * mm});
            skLineSegment(sketch, "E876", {"start": v(-232.69, -96.29) * mm, "end": v(-224.82, -96.29) * mm});
            skLineSegment(sketch, "E877", {"start": v(-224.82, -96.29) * mm, "end": v(-224.82, -99.46) * mm});
            skLineSegment(sketch, "E878", {"start": v(-216.91, -99.46) * mm, "end": v(-208.74, -99.46) * mm});
            skLineSegment(sketch, "E879", {"start": v(-216.64, -96.29) * mm, "end": v(-216.64, -99.46) * mm});
            skLineSegment(sketch, "E880", {"start": v(-216.64, -96.29) * mm, "end": v(-208.77, -96.29) * mm});
            skLineSegment(sketch, "E881", {"start": v(-208.77, -96.29) * mm, "end": v(-208.77, -99.46) * mm});
            skLineSegment(sketch, "E882", {"start": v(-200.87, -99.46) * mm, "end": v(-192.7, -99.46) * mm});
            skLineSegment(sketch, "E883", {"start": v(-200.6, -96.29) * mm, "end": v(-200.6, -99.46) * mm});
            skLineSegment(sketch, "E884", {"start": v(-200.6, -96.29) * mm, "end": v(-192.73, -96.29) * mm});
            skLineSegment(sketch, "E885", {"start": v(-192.73, -96.29) * mm, "end": v(-192.73, -99.46) * mm});
            skLineSegment(sketch, "E886", {"start": v(-184.82, -99.46) * mm, "end": v(-176.65, -99.46) * mm});
            skLineSegment(sketch, "E887", {"start": v(-184.55, -96.29) * mm, "end": v(-184.55, -99.46) * mm});
            skLineSegment(sketch, "E888", {"start": v(-184.55, -96.29) * mm, "end": v(-176.68, -96.29) * mm});
            skLineSegment(sketch, "E889", {"start": v(-176.68, -96.29) * mm, "end": v(-176.68, -99.46) * mm});
            skLineSegment(sketch, "E890", {"start": v(-168.78, -99.46) * mm, "end": v(-160.6, -99.46) * mm});
            skLineSegment(sketch, "E891", {"start": v(-168.5, -96.29) * mm, "end": v(-168.5, -99.46) * mm});
            skLineSegment(sketch, "E892", {"start": v(-168.5, -96.29) * mm, "end": v(-160.64, -96.29) * mm});
            skLineSegment(sketch, "E893", {"start": v(-160.64, -96.29) * mm, "end": v(-160.64, -99.46) * mm});
            skLineSegment(sketch, "E894", {"start": v(-152.73, -99.46) * mm, "end": v(-144.56, -99.46) * mm});
            skLineSegment(sketch, "E895", {"start": v(-152.46, -96.29) * mm, "end": v(-152.46, -99.46) * mm});
            skLineSegment(sketch, "E896", {"start": v(-152.46, -96.29) * mm, "end": v(-144.6, -96.29) * mm});
            skLineSegment(sketch, "E897", {"start": v(-144.6, -96.29) * mm, "end": v(-144.6, -99.46) * mm});
            skLineSegment(sketch, "E898", {"start": v(-136.69, -99.46) * mm, "end": v(-128.51, -99.46) * mm});
            skLineSegment(sketch, "E899", {"start": v(-136.42, -96.29) * mm, "end": v(-136.42, -99.46) * mm});
            skLineSegment(sketch, "E900", {"start": v(-136.42, -96.29) * mm, "end": v(-128.54, -96.29) * mm});
            skLineSegment(sketch, "E901", {"start": v(-128.54, -96.29) * mm, "end": v(-128.54, -99.46) * mm});
            skLineSegment(sketch, "E902", {"start": v(-120.64, -99.46) * mm, "end": v(-112.47, -99.46) * mm});
            skLineSegment(sketch, "E903", {"start": v(-120.37, -96.29) * mm, "end": v(-120.37, -99.46) * mm});
            skLineSegment(sketch, "E904", {"start": v(-120.37, -96.29) * mm, "end": v(-112.5, -96.29) * mm});
            skLineSegment(sketch, "E905", {"start": v(-112.5, -96.29) * mm, "end": v(-112.5, -99.46) * mm});
            skLineSegment(sketch, "E906", {"start": v(-104.6, -99.46) * mm, "end": v(-96.42, -99.46) * mm});
            skLineSegment(sketch, "E907", {"start": v(-104.32, -96.29) * mm, "end": v(-104.32, -99.46) * mm});
            skLineSegment(sketch, "E908", {"start": v(-104.32, -96.29) * mm, "end": v(-96.45, -96.29) * mm});
            skLineSegment(sketch, "E909", {"start": v(-96.45, -96.29) * mm, "end": v(-96.45, -99.46) * mm});
            skLineSegment(sketch, "E910", {"start": v(-88.55, -99.46) * mm, "end": v(-80.38, -99.46) * mm});
            skLineSegment(sketch, "E911", {"start": v(-88.28, -96.29) * mm, "end": v(-88.28, -99.46) * mm});
            skLineSegment(sketch, "E912", {"start": v(-88.28, -96.29) * mm, "end": v(-80.4, -96.29) * mm});
            skLineSegment(sketch, "E913", {"start": v(-80.4, -96.29) * mm, "end": v(-80.4, -99.46) * mm});
            skLineSegment(sketch, "E914", {"start": v(-72.5, -99.46) * mm, "end": v(-64.33, -99.46) * mm});
            skLineSegment(sketch, "E915", {"start": v(-72.23, -96.29) * mm, "end": v(-72.23, -99.46) * mm});
            skLineSegment(sketch, "E916", {"start": v(-72.23, -96.29) * mm, "end": v(-64.36, -96.29) * mm});
            skLineSegment(sketch, "E917", {"start": v(-64.36, -96.29) * mm, "end": v(-64.36, -99.46) * mm});
            skLineSegment(sketch, "E918", {"start": v(-56.46, -99.46) * mm, "end": v(-48.29, -99.46) * mm});
            skLineSegment(sketch, "E919", {"start": v(-56.19, -96.29) * mm, "end": v(-56.19, -99.46) * mm});
            skLineSegment(sketch, "E920", {"start": v(-56.19, -96.29) * mm, "end": v(-48.32, -96.29) * mm});
            skLineSegment(sketch, "E921", {"start": v(-48.32, -96.29) * mm, "end": v(-48.32, -99.46) * mm});
            skLineSegment(sketch, "E922", {"start": v(-40.42, -99.46) * mm, "end": v(-32.24, -99.46) * mm});
            skLineSegment(sketch, "E923", {"start": v(-40.14, -96.29) * mm, "end": v(-40.14, -99.46) * mm});
            skLineSegment(sketch, "E924", {"start": v(-40.14, -96.29) * mm, "end": v(-32.27, -96.29) * mm});
            skLineSegment(sketch, "E925", {"start": v(-32.27, -96.29) * mm, "end": v(-32.27, -99.46) * mm});
            skLineSegment(sketch, "E926", {"start": v(-24.37, -99.46) * mm, "end": v(-16.2, -99.46) * mm});
            skLineSegment(sketch, "E927", {"start": v(-24.1, -96.29) * mm, "end": v(-24.1, -99.46) * mm});
            skLineSegment(sketch, "E928", {"start": v(-24.1, -96.29) * mm, "end": v(-16.23, -96.29) * mm});
            skLineSegment(sketch, "E929", {"start": v(-16.23, -96.29) * mm, "end": v(-16.23, -99.46) * mm});
            skLineSegment(sketch, "E930", {"start": v(-8.33, -99.46) * mm, "end": v(-0.15, -99.46) * mm});
            skLineSegment(sketch, "E931", {"start": v(-8.05, -96.29) * mm, "end": v(-8.05, -99.46) * mm});
            skLineSegment(sketch, "E932", {"start": v(-8.05, -96.29) * mm, "end": v(-0.18, -96.29) * mm});
            skLineSegment(sketch, "E933", {"start": v(-0.18, -96.29) * mm, "end": v(-0.18, -99.46) * mm});
            skLineSegment(sketch, "E934", {"start": v(7.72, -99.46) * mm, "end": v(15.9, -99.46) * mm});
            skLineSegment(sketch, "E935", {"start": v(8, -96.29) * mm, "end": v(8, -99.46) * mm});
            skLineSegment(sketch, "E936", {"start": v(8, -96.29) * mm, "end": v(15.86, -96.29) * mm});
            skLineSegment(sketch, "E937", {"start": v(15.86, -96.29) * mm, "end": v(15.86, -99.46) * mm});
            skLineSegment(sketch, "E938", {"start": v(23.77, -99.46) * mm, "end": v(31.94, -99.46) * mm});
            skLineSegment(sketch, "E939", {"start": v(24.04, -96.29) * mm, "end": v(24.04, -99.46) * mm});
            skLineSegment(sketch, "E940", {"start": v(24.04, -96.29) * mm, "end": v(31.9, -96.29) * mm});
            skLineSegment(sketch, "E941", {"start": v(31.9, -96.29) * mm, "end": v(31.9, -99.46) * mm});
            skLineSegment(sketch, "E942", {"start": v(39.81, -99.46) * mm, "end": v(47.99, -99.46) * mm});
            skLineSegment(sketch, "E943", {"start": v(40.08, -96.29) * mm, "end": v(40.08, -99.46) * mm});
            skLineSegment(sketch, "E944", {"start": v(40.08, -96.29) * mm, "end": v(47.95, -96.29) * mm});
            skLineSegment(sketch, "E945", {"start": v(47.95, -96.29) * mm, "end": v(47.95, -99.46) * mm});
            skLineSegment(sketch, "E946", {"start": v(55.86, -99.46) * mm, "end": v(64.03, -99.46) * mm});
            skLineSegment(sketch, "E947", {"start": v(56.13, -96.29) * mm, "end": v(56.13, -99.46) * mm});
            skLineSegment(sketch, "E948", {"start": v(56.13, -96.29) * mm, "end": v(64, -96.29) * mm});
            skLineSegment(sketch, "E949", {"start": v(64, -96.29) * mm, "end": v(64, -99.46) * mm});
            skLineSegment(sketch, "E950", {"start": v(71.9, -99.46) * mm, "end": v(80.08, -99.46) * mm});
            skLineSegment(sketch, "E951", {"start": v(72.17, -96.29) * mm, "end": v(72.17, -99.46) * mm});
            skLineSegment(sketch, "E952", {"start": v(72.17, -96.29) * mm, "end": v(80.04, -96.29) * mm});
            skLineSegment(sketch, "E953", {"start": v(80.04, -96.29) * mm, "end": v(80.04, -99.46) * mm});
            skLineSegment(sketch, "E954", {"start": v(87.95, -99.46) * mm, "end": v(96.12, -99.46) * mm});
            skLineSegment(sketch, "E955", {"start": v(88.22, -96.29) * mm, "end": v(88.22, -99.46) * mm});
            skLineSegment(sketch, "E956", {"start": v(88.22, -96.29) * mm, "end": v(96.09, -96.29) * mm});
            skLineSegment(sketch, "E957", {"start": v(96.09, -96.29) * mm, "end": v(96.09, -99.46) * mm});
            skLineSegment(sketch, "E958", {"start": v(104, -99.46) * mm, "end": v(112.17, -99.46) * mm});
            skLineSegment(sketch, "E959", {"start": v(104.26, -96.29) * mm, "end": v(104.26, -99.46) * mm});
            skLineSegment(sketch, "E960", {"start": v(104.26, -96.29) * mm, "end": v(112.13, -96.29) * mm});
            skLineSegment(sketch, "E961", {"start": v(112.13, -96.29) * mm, "end": v(112.13, -99.46) * mm});
            skLineSegment(sketch, "E962", {"start": v(120.04, -99.46) * mm, "end": v(128.21, -99.46) * mm});
            skLineSegment(sketch, "E963", {"start": v(120.3, -96.29) * mm, "end": v(120.3, -99.46) * mm});
            skLineSegment(sketch, "E964", {"start": v(120.3, -96.29) * mm, "end": v(128.18, -96.29) * mm});
            skLineSegment(sketch, "E965", {"start": v(128.18, -96.29) * mm, "end": v(128.18, -99.46) * mm});
            skLineSegment(sketch, "E966", {"start": v(136.08, -99.46) * mm, "end": v(144.26, -99.46) * mm});
            skLineSegment(sketch, "E967", {"start": v(136.36, -96.29) * mm, "end": v(136.36, -99.46) * mm});
            skLineSegment(sketch, "E968", {"start": v(136.36, -96.29) * mm, "end": v(144.23, -96.29) * mm});
            skLineSegment(sketch, "E969", {"start": v(144.23, -96.29) * mm, "end": v(144.23, -99.46) * mm});
            skLineSegment(sketch, "E970", {"start": v(152.13, -99.46) * mm, "end": v(160.3, -99.46) * mm});
            skLineSegment(sketch, "E971", {"start": v(152.4, -96.29) * mm, "end": v(152.4, -99.46) * mm});
            skLineSegment(sketch, "E972", {"start": v(152.4, -96.29) * mm, "end": v(160.27, -96.29) * mm});
            skLineSegment(sketch, "E973", {"start": v(160.27, -96.29) * mm, "end": v(160.27, -99.46) * mm});
            skLineSegment(sketch, "E974", {"start": v(168.17, -99.46) * mm, "end": v(176.35, -99.46) * mm});
            skLineSegment(sketch, "E975", {"start": v(168.45, -96.29) * mm, "end": v(168.45, -99.46) * mm});
            skLineSegment(sketch, "E976", {"start": v(168.45, -96.29) * mm, "end": v(176.32, -96.29) * mm});
            skLineSegment(sketch, "E977", {"start": v(176.32, -96.29) * mm, "end": v(176.32, -99.46) * mm});
            skLineSegment(sketch, "E978", {"start": v(184.22, -99.46) * mm, "end": v(192.4, -99.46) * mm});
            skLineSegment(sketch, "E979", {"start": v(184.5, -96.29) * mm, "end": v(184.5, -99.46) * mm});
            skLineSegment(sketch, "E980", {"start": v(184.5, -96.29) * mm, "end": v(192.36, -96.29) * mm});
            skLineSegment(sketch, "E981", {"start": v(192.36, -96.29) * mm, "end": v(192.36, -99.46) * mm});
            skLineSegment(sketch, "E982", {"start": v(200.26, -99.46) * mm, "end": v(208.44, -99.46) * mm});
            skLineSegment(sketch, "E983", {"start": v(200.54, -96.29) * mm, "end": v(200.54, -99.46) * mm});
            skLineSegment(sketch, "E984", {"start": v(200.54, -96.29) * mm, "end": v(208.4, -96.29) * mm});
            skLineSegment(sketch, "E985", {"start": v(208.4, -96.29) * mm, "end": v(208.4, -99.46) * mm});
            skLineSegment(sketch, "E986", {"start": v(216.3, -99.46) * mm, "end": v(224.48, -99.46) * mm});
            skLineSegment(sketch, "E987", {"start": v(216.58, -96.29) * mm, "end": v(216.58, -99.46) * mm});
            skLineSegment(sketch, "E988", {"start": v(216.58, -96.29) * mm, "end": v(224.45, -96.29) * mm});
            skLineSegment(sketch, "E989", {"start": v(224.45, -96.29) * mm, "end": v(224.45, -99.46) * mm});
            skLineSegment(sketch, "E990", {"start": v(232.35, -99.46) * mm, "end": v(240.53, -99.46) * mm});
            skLineSegment(sketch, "E991", {"start": v(232.63, -96.29) * mm, "end": v(232.63, -99.46) * mm});
            skLineSegment(sketch, "E992", {"start": v(232.63, -96.29) * mm, "end": v(240.5, -96.29) * mm});
            skLineSegment(sketch, "E993", {"start": v(240.5, -96.29) * mm, "end": v(240.5, -99.46) * mm});
            skLineSegment(sketch, "E994", {"start": v(248.4, -99.46) * mm, "end": v(256.57, -99.46) * mm});
            skLineSegment(sketch, "E995", {"start": v(248.67, -96.29) * mm, "end": v(248.67, -99.46) * mm});
            skLineSegment(sketch, "E996", {"start": v(248.67, -96.29) * mm, "end": v(256.54, -96.29) * mm});
            skLineSegment(sketch, "E997", {"start": v(256.54, -96.29) * mm, "end": v(256.54, -99.46) * mm});
            skLineSegment(sketch, "E998", {"start": v(264.44, -99.46) * mm, "end": v(272.62, -99.46) * mm});
            skLineSegment(sketch, "E999", {"start": v(264.72, -96.29) * mm, "end": v(264.72, -99.46) * mm});
            skLineSegment(sketch, "E1000", {"start": v(264.72, -96.29) * mm, "end": v(272.59, -96.29) * mm});
            skLineSegment(sketch, "E1001", {"start": v(272.59, -96.29) * mm, "end": v(272.59, -99.46) * mm});
            skLineSegment(sketch, "E1002", {"start": v(280.5, -99.46) * mm, "end": v(288.67, -99.46) * mm});
            skLineSegment(sketch, "E1003", {"start": v(280.76, -96.29) * mm, "end": v(280.76, -99.46) * mm});
            skLineSegment(sketch, "E1004", {"start": v(280.76, -96.29) * mm, "end": v(288.63, -96.29) * mm});
            skLineSegment(sketch, "E1005", {"start": v(288.63, -96.29) * mm, "end": v(288.63, -99.46) * mm});
            skLineSegment(sketch, "E1006", {"start": v(296.54, -99.46) * mm, "end": v(304.71, -99.46) * mm});
            skLineSegment(sketch, "E1007", {"start": v(296.8, -96.29) * mm, "end": v(296.8, -99.46) * mm});
            skLineSegment(sketch, "E1008", {"start": v(296.8, -96.29) * mm, "end": v(304.68, -96.29) * mm});
            skLineSegment(sketch, "E1009", {"start": v(304.68, -96.29) * mm, "end": v(304.68, -99.46) * mm});
            skLineSegment(sketch, "E1010", {"start": v(312.83, -99.46) * mm, "end": v(317.62, -99.46) * mm});
            skLineSegment(sketch, "E1011", {"start": v(312.85, -96.29) * mm, "end": v(312.85, -99.46) * mm});
            skLineSegment(sketch, "E1012", {"start": v(312.85, -96.29) * mm, "end": v(317.63, -96.29) * mm});
            skLineSegment(sketch, "E1013", {"start": v(-438.16, -99.46) * mm, "end": v(-433.42, -99.46) * mm});
            skLineSegment(sketch, "E1014", {"start": v(442.68, 177.55) * mm, "end": v(442.68, 186.57) * mm});
            skLineSegment(sketch, "E1015", {"start": v(445.85, 177.55) * mm, "end": v(442.68, 177.55) * mm});
            skLineSegment(sketch, "E1016", {"start": v(445.85, 168.3) * mm, "end": v(445.85, 177.55) * mm});
            skLineSegment(sketch, "E1017", {"start": v(445.85, 168.3) * mm, "end": v(442.68, 168.3) * mm});
            skLineSegment(sketch, "E1018", {"start": v(442.68, 159.36) * mm, "end": v(442.68, 168.3) * mm});
            skLineSegment(sketch, "E1019", {"start": v(445.85, 159.36) * mm, "end": v(442.68, 159.36) * mm});
            skLineSegment(sketch, "E1020", {"start": v(445.85, 150.12) * mm, "end": v(445.85, 159.36) * mm});
            skLineSegment(sketch, "E1021", {"start": v(445.85, 150.12) * mm, "end": v(442.68, 150.12) * mm});
            skLineSegment(sketch, "E1022", {"start": v(442.68, 141.18) * mm, "end": v(442.68, 150.12) * mm});
            skLineSegment(sketch, "E1023", {"start": v(445.85, 141.18) * mm, "end": v(442.68, 141.18) * mm});
            skLineSegment(sketch, "E1024", {"start": v(445.85, 131.93) * mm, "end": v(445.85, 141.18) * mm});
            skLineSegment(sketch, "E1025", {"start": v(445.85, 131.93) * mm, "end": v(442.68, 131.93) * mm});
            skLineSegment(sketch, "E1026", {"start": v(442.68, 122.92) * mm, "end": v(442.68, 131.93) * mm});
            skLineSegment(sketch, "E1027", {"start": v(318.7, 177.4) * mm, "end": v(318.7, 186.57) * mm});
            skLineSegment(sketch, "E1028", {"start": v(321.87, 177.4) * mm, "end": v(318.7, 177.4) * mm});
            skLineSegment(sketch, "E1029", {"start": v(321.87, 168.46) * mm, "end": v(321.87, 177.4) * mm});
            skLineSegment(sketch, "E1030", {"start": v(321.87, 168.46) * mm, "end": v(318.7, 168.46) * mm});
            skLineSegment(sketch, "E1031", {"start": v(318.7, 159.21) * mm, "end": v(318.7, 168.46) * mm});
            skLineSegment(sketch, "E1032", {"start": v(321.87, 159.21) * mm, "end": v(318.7, 159.21) * mm});
            skLineSegment(sketch, "E1033", {"start": v(321.87, 150.27) * mm, "end": v(321.87, 159.21) * mm});
            skLineSegment(sketch, "E1034", {"start": v(321.87, 150.27) * mm, "end": v(318.7, 150.27) * mm});
            skLineSegment(sketch, "E1035", {"start": v(318.7, 141.03) * mm, "end": v(318.7, 150.27) * mm});
            skLineSegment(sketch, "E1036", {"start": v(321.87, 141.03) * mm, "end": v(318.7, 141.03) * mm});
            skLineSegment(sketch, "E1037", {"start": v(321.87, 132.08) * mm, "end": v(321.87, 141.03) * mm});
            skLineSegment(sketch, "E1038", {"start": v(321.87, 132.08) * mm, "end": v(318.7, 132.08) * mm});
            skLineSegment(sketch, "E1039", {"start": v(318.7, 122.92) * mm, "end": v(318.7, 132.08) * mm});
            skLineSegment(sketch, "E1040", {"start": v(335.58, 186.57) * mm, "end": v(344.2, 186.57) * mm});
            skLineSegment(sketch, "E1041", {"start": v(344.2, 186.57) * mm, "end": v(437.3, 186.57) * mm});
            skLineSegment(sketch, "E1042", {"start": v(437.3, 186.57) * mm, "end": v(442.68, 186.57) * mm});
            skLineSegment(sketch, "E1043", {"start": v(335.58, 186.57) * mm, "end": v(335.58, 183.4) * mm});
            skLineSegment(sketch, "E1044", {"start": v(327.25, 183.4) * mm, "end": v(335.58, 183.4) * mm});
            skLineSegment(sketch, "E1045", {"start": v(327.25, 186.57) * mm, "end": v(327.25, 183.4) * mm});
            skLineSegment(sketch, "E1046", {"start": v(318.7, 186.57) * mm, "end": v(327.25, 186.57) * mm});
            skLineSegment(sketch, "E1047", {"start": v(437.3, 122.92) * mm, "end": v(442.68, 122.92) * mm});
            skLineSegment(sketch, "E1048", {"start": v(437.3, 126.1) * mm, "end": v(437.3, 122.92) * mm});
            skLineSegment(sketch, "E1049", {"start": v(428.97, 126.1) * mm, "end": v(437.3, 126.1) * mm});
            skLineSegment(sketch, "E1050", {"start": v(428.97, 126.1) * mm, "end": v(428.97, 122.92) * mm});
            skLineSegment(sketch, "E1051", {"start": v(420.34, 122.92) * mm, "end": v(428.97, 122.92) * mm});
            skLineSegment(sketch, "E1052", {"start": v(420.34, 126.1) * mm, "end": v(420.34, 122.92) * mm});
            skLineSegment(sketch, "E1053", {"start": v(412.02, 126.1) * mm, "end": v(420.34, 126.1) * mm});
            skLineSegment(sketch, "E1054", {"start": v(412.02, 126.1) * mm, "end": v(412.02, 122.92) * mm});
            skLineSegment(sketch, "E1055", {"start": v(403.4, 122.92) * mm, "end": v(412.02, 122.92) * mm});
            skLineSegment(sketch, "E1056", {"start": v(403.4, 126.1) * mm, "end": v(403.4, 122.92) * mm});
            skLineSegment(sketch, "E1057", {"start": v(395.07, 126.1) * mm, "end": v(403.4, 126.1) * mm});
            skLineSegment(sketch, "E1058", {"start": v(395.07, 126.1) * mm, "end": v(395.07, 122.92) * mm});
            skLineSegment(sketch, "E1059", {"start": v(386.44, 122.92) * mm, "end": v(395.07, 122.92) * mm});
            skLineSegment(sketch, "E1060", {"start": v(386.44, 126.1) * mm, "end": v(386.44, 122.92) * mm});
            skLineSegment(sketch, "E1061", {"start": v(378.11, 126.1) * mm, "end": v(386.44, 126.1) * mm});
            skLineSegment(sketch, "E1062", {"start": v(378.11, 126.1) * mm, "end": v(378.11, 122.92) * mm});
            skLineSegment(sketch, "E1063", {"start": v(369.48, 122.92) * mm, "end": v(378.11, 122.92) * mm});
            skLineSegment(sketch, "E1064", {"start": v(369.48, 126.1) * mm, "end": v(369.48, 122.92) * mm});
            skLineSegment(sketch, "E1065", {"start": v(361.16, 126.1) * mm, "end": v(369.48, 126.1) * mm});
            skLineSegment(sketch, "E1066", {"start": v(361.16, 126.1) * mm, "end": v(361.16, 122.92) * mm});
            skLineSegment(sketch, "E1067", {"start": v(352.53, 122.92) * mm, "end": v(361.16, 122.92) * mm});
            skLineSegment(sketch, "E1068", {"start": v(352.53, 126.1) * mm, "end": v(352.53, 122.92) * mm});
            skLineSegment(sketch, "E1069", {"start": v(344.2, 126.1) * mm, "end": v(352.53, 126.1) * mm});
            skLineSegment(sketch, "E1070", {"start": v(344.2, 126.1) * mm, "end": v(344.2, 122.92) * mm});
            skLineSegment(sketch, "E1071", {"start": v(335.58, 122.92) * mm, "end": v(344.2, 122.92) * mm});
            skLineSegment(sketch, "E1072", {"start": v(335.58, 126.1) * mm, "end": v(335.58, 122.92) * mm});
            skLineSegment(sketch, "E1073", {"start": v(327.25, 126.1) * mm, "end": v(335.58, 126.1) * mm});
            skLineSegment(sketch, "E1074", {"start": v(327.25, 126.1) * mm, "end": v(327.25, 122.92) * mm});
            skLineSegment(sketch, "E1075", {"start": v(318.7, 122.92) * mm, "end": v(327.25, 122.92) * mm});
            skLineSegment(sketch, "E1076", {"start": v(343.97, 132.08) * mm, "end": v(340.8, 132.08) * mm});
            skLineSegment(sketch, "E1077", {"start": v(340.8, 132.08) * mm, "end": v(340.8, 141.03) * mm});
            skLineSegment(sketch, "E1078", {"start": v(340.8, 141.03) * mm, "end": v(343.97, 141.03) * mm});
            skLineSegment(sketch, "E1079", {"start": v(343.97, 132.08) * mm, "end": v(343.97, 141.03) * mm});
            skLineSegment(sketch, "E1080", {"start": v(340.8, 150.06) * mm, "end": v(340.8, 159.3) * mm});
            skLineSegment(sketch, "E1081", {"start": v(343.97, 150.27) * mm, "end": v(340.8, 150.27) * mm});
            skLineSegment(sketch, "E1082", {"start": v(343.97, 150.27) * mm, "end": v(343.97, 159.21) * mm});
            skLineSegment(sketch, "E1083", {"start": v(343.97, 159.21) * mm, "end": v(340.8, 159.21) * mm});
            skLineSegment(sketch, "E1084", {"start": v(340.8, 168.25) * mm, "end": v(340.8, 177.5) * mm});
            skLineSegment(sketch, "E1085", {"start": v(343.97, 168.46) * mm, "end": v(340.8, 168.46) * mm});
            skLineSegment(sketch, "E1086", {"start": v(343.97, 168.46) * mm, "end": v(343.97, 177.4) * mm});
            skLineSegment(sketch, "E1087", {"start": v(343.97, 177.4) * mm, "end": v(340.8, 177.4) * mm});
            skLineSegment(sketch, "E1088", {"start": v(442.24, 108.94) * mm, "end": v(442.24, 117.96) * mm});
            skLineSegment(sketch, "E1089", {"start": v(445.41, 108.94) * mm, "end": v(442.24, 108.94) * mm});
            skLineSegment(sketch, "E1090", {"start": v(445.41, 99.7) * mm, "end": v(445.41, 108.94) * mm});
            skLineSegment(sketch, "E1091", {"start": v(445.41, 99.7) * mm, "end": v(442.24, 99.7) * mm});
            skLineSegment(sketch, "E1092", {"start": v(442.24, 90.76) * mm, "end": v(442.24, 99.7) * mm});
            skLineSegment(sketch, "E1093", {"start": v(445.41, 90.76) * mm, "end": v(442.24, 90.76) * mm});
            skLineSegment(sketch, "E1094", {"start": v(445.41, 81.51) * mm, "end": v(445.41, 90.76) * mm});
            skLineSegment(sketch, "E1095", {"start": v(445.41, 81.51) * mm, "end": v(442.24, 81.51) * mm});
            skLineSegment(sketch, "E1096", {"start": v(442.24, 72.57) * mm, "end": v(442.24, 81.51) * mm});
            skLineSegment(sketch, "E1097", {"start": v(445.41, 72.57) * mm, "end": v(442.24, 72.57) * mm});
            skLineSegment(sketch, "E1098", {"start": v(445.41, 63.33) * mm, "end": v(445.41, 72.57) * mm});
            skLineSegment(sketch, "E1099", {"start": v(445.41, 63.33) * mm, "end": v(442.24, 63.33) * mm});
            skLineSegment(sketch, "E1100", {"start": v(442.24, 54.3) * mm, "end": v(442.24, 63.33) * mm});
            skLineSegment(sketch, "E1101", {"start": v(318.26, 108.8) * mm, "end": v(318.26, 117.96) * mm});
            skLineSegment(sketch, "E1102", {"start": v(321.43, 108.8) * mm, "end": v(318.26, 108.8) * mm});
            skLineSegment(sketch, "E1103", {"start": v(321.43, 99.85) * mm, "end": v(321.43, 108.8) * mm});
            skLineSegment(sketch, "E1104", {"start": v(321.43, 99.85) * mm, "end": v(318.26, 99.85) * mm});
            skLineSegment(sketch, "E1105", {"start": v(318.26, 90.6) * mm, "end": v(318.26, 99.85) * mm});
            skLineSegment(sketch, "E1106", {"start": v(321.43, 90.6) * mm, "end": v(318.26, 90.6) * mm});
            skLineSegment(sketch, "E1107", {"start": v(321.43, 81.66) * mm, "end": v(321.43, 90.6) * mm});
            skLineSegment(sketch, "E1108", {"start": v(321.43, 81.66) * mm, "end": v(318.26, 81.66) * mm});
            skLineSegment(sketch, "E1109", {"start": v(318.26, 72.42) * mm, "end": v(318.26, 81.66) * mm});
            skLineSegment(sketch, "E1110", {"start": v(321.43, 72.42) * mm, "end": v(318.26, 72.42) * mm});
            skLineSegment(sketch, "E1111", {"start": v(321.43, 63.48) * mm, "end": v(321.43, 72.42) * mm});
            skLineSegment(sketch, "E1112", {"start": v(321.43, 63.48) * mm, "end": v(318.26, 63.48) * mm});
            skLineSegment(sketch, "E1113", {"start": v(318.26, 54.3) * mm, "end": v(318.26, 63.48) * mm});
            skLineSegment(sketch, "E1114", {"start": v(436.86, 117.96) * mm, "end": v(442.24, 117.96) * mm});
            skLineSegment(sketch, "E1115", {"start": v(436.86, 117.96) * mm, "end": v(436.86, 114.79) * mm});
            skLineSegment(sketch, "E1116", {"start": v(428.53, 114.79) * mm, "end": v(436.86, 114.79) * mm});
            skLineSegment(sketch, "E1117", {"start": v(428.53, 117.96) * mm, "end": v(428.53, 114.79) * mm});
            skLineSegment(sketch, "E1118", {"start": v(318.26, 117.96) * mm, "end": v(326.81, 117.96) * mm});
            skLineSegment(sketch, "E1119", {"start": v(326.81, 117.96) * mm, "end": v(419.9, 117.96) * mm});
            skLineSegment(sketch, "E1120", {"start": v(419.9, 117.96) * mm, "end": v(428.53, 117.96) * mm});
            skLineSegment(sketch, "E1121", {"start": v(436.86, 54.3) * mm, "end": v(442.24, 54.3) * mm});
            skLineSegment(sketch, "E1122", {"start": v(436.86, 57.48) * mm, "end": v(436.86, 54.3) * mm});
            skLineSegment(sketch, "E1123", {"start": v(428.53, 57.48) * mm, "end": v(436.86, 57.48) * mm});
            skLineSegment(sketch, "E1124", {"start": v(428.53, 57.48) * mm, "end": v(428.53, 54.3) * mm});
            skLineSegment(sketch, "E1125", {"start": v(419.9, 54.3) * mm, "end": v(428.53, 54.3) * mm});
            skLineSegment(sketch, "E1126", {"start": v(419.9, 57.5) * mm, "end": v(419.9, 54.3) * mm});
            skLineSegment(sketch, "E1127", {"start": v(411.58, 57.48) * mm, "end": v(419.9, 57.48) * mm});
            skLineSegment(sketch, "E1128", {"start": v(411.58, 57.48) * mm, "end": v(411.58, 54.3) * mm});
            skLineSegment(sketch, "E1129", {"start": v(402.95, 54.3) * mm, "end": v(411.58, 54.3) * mm});
            skLineSegment(sketch, "E1130", {"start": v(402.95, 57.48) * mm, "end": v(402.95, 54.3) * mm});
            skLineSegment(sketch, "E1131", {"start": v(394.63, 57.48) * mm, "end": v(402.95, 57.48) * mm});
            skLineSegment(sketch, "E1132", {"start": v(394.63, 57.48) * mm, "end": v(394.63, 54.3) * mm});
            skLineSegment(sketch, "E1133", {"start": v(386, 54.3) * mm, "end": v(394.63, 54.3) * mm});
            skLineSegment(sketch, "E1134", {"start": v(386, 57.48) * mm, "end": v(386, 54.3) * mm});
            skLineSegment(sketch, "E1135", {"start": v(377.67, 57.48) * mm, "end": v(386, 57.48) * mm});
            skLineSegment(sketch, "E1136", {"start": v(377.67, 57.48) * mm, "end": v(377.67, 54.3) * mm});
            skLineSegment(sketch, "E1137", {"start": v(369.04, 54.3) * mm, "end": v(377.67, 54.3) * mm});
            skLineSegment(sketch, "E1138", {"start": v(369.04, 57.48) * mm, "end": v(369.04, 54.3) * mm});
            skLineSegment(sketch, "E1139", {"start": v(360.72, 57.48) * mm, "end": v(369.04, 57.48) * mm});
            skLineSegment(sketch, "E1140", {"start": v(360.72, 57.48) * mm, "end": v(360.72, 54.3) * mm});
            skLineSegment(sketch, "E1141", {"start": v(352.1, 54.3) * mm, "end": v(360.72, 54.3) * mm});
            skLineSegment(sketch, "E1142", {"start": v(352.1, 57.48) * mm, "end": v(352.1, 54.3) * mm});
            skLineSegment(sketch, "E1143", {"start": v(343.77, 57.48) * mm, "end": v(352.1, 57.48) * mm});
            skLineSegment(sketch, "E1144", {"start": v(343.77, 57.48) * mm, "end": v(343.77, 54.3) * mm});
            skLineSegment(sketch, "E1145", {"start": v(335.14, 54.3) * mm, "end": v(343.77, 54.3) * mm});
            skLineSegment(sketch, "E1146", {"start": v(335.14, 57.48) * mm, "end": v(335.14, 54.3) * mm});
            skLineSegment(sketch, "E1147", {"start": v(326.81, 57.48) * mm, "end": v(335.14, 57.48) * mm});
            skLineSegment(sketch, "E1148", {"start": v(326.81, 57.48) * mm, "end": v(326.81, 54.3) * mm});
            skLineSegment(sketch, "E1149", {"start": v(318.26, 54.3) * mm, "end": v(326.81, 54.3) * mm});
            skLineSegment(sketch, "E1150", {"start": v(419.85, 57.46) * mm, "end": v(419.85, 63.33) * mm});
            skLineSegment(sketch, "E1151", {"start": v(423.02, 63.33) * mm, "end": v(419.85, 63.33) * mm});
            skLineSegment(sketch, "E1152", {"start": v(423.02, 72.36) * mm, "end": v(423.02, 81.6) * mm});
            skLineSegment(sketch, "E1153", {"start": v(423.02, 72.57) * mm, "end": v(419.85, 72.57) * mm});
            skLineSegment(sketch, "E1154", {"start": v(419.85, 72.57) * mm, "end": v(419.85, 81.51) * mm});
            skLineSegment(sketch, "E1155", {"start": v(423.02, 81.51) * mm, "end": v(419.85, 81.51) * mm});
            skLineSegment(sketch, "E1156", {"start": v(423.02, 90.54) * mm, "end": v(423.02, 99.79) * mm});
            skLineSegment(sketch, "E1157", {"start": v(423.02, 90.76) * mm, "end": v(419.85, 90.76) * mm});
            skLineSegment(sketch, "E1158", {"start": v(419.85, 90.76) * mm, "end": v(419.85, 99.7) * mm});
            skLineSegment(sketch, "E1159", {"start": v(423.02, 99.7) * mm, "end": v(419.85, 99.7) * mm});
            skLineSegment(sketch, "E1160", {"start": v(423.02, 108.73) * mm, "end": v(423.02, 117.98) * mm});
            skLineSegment(sketch, "E1161", {"start": v(423.02, 108.94) * mm, "end": v(419.84, 108.94) * mm});
            skLineSegment(sketch, "E1162", {"start": v(419.84, 108.94) * mm, "end": v(419.84, 117.96) * mm});
            skLineSegment(sketch, "E1163", {"start": v(422.99, 63.35) * mm, "end": v(422.99, 57.4) * mm});
            skLineSegment(sketch, "E1164", {"start": v(419.84, 57.47) * mm, "end": v(422.99, 57.47) * mm});
            skLineSegment(sketch, "E1165", {"start": v(314.26, 68.84) * mm, "end": v(314.26, 77.85) * mm});
            skLineSegment(sketch, "E1166", {"start": v(317.43, 68.84) * mm, "end": v(314.26, 68.84) * mm});
            skLineSegment(sketch, "E1167", {"start": v(317.43, 59.6) * mm, "end": v(317.43, 68.84) * mm});
            skLineSegment(sketch, "E1168", {"start": v(317.43, 59.6) * mm, "end": v(314.26, 59.6) * mm});
            skLineSegment(sketch, "E1169", {"start": v(314.26, 50.65) * mm, "end": v(314.26, 59.6) * mm});
            skLineSegment(sketch, "E1170", {"start": v(317.43, 50.65) * mm, "end": v(314.26, 50.65) * mm});
            skLineSegment(sketch, "E1171", {"start": v(317.43, 41.4) * mm, "end": v(317.43, 50.65) * mm});
            skLineSegment(sketch, "E1172", {"start": v(317.43, 41.4) * mm, "end": v(314.26, 41.4) * mm});
            skLineSegment(sketch, "E1173", {"start": v(314.26, 32.46) * mm, "end": v(314.26, 41.4) * mm});
            skLineSegment(sketch, "E1174", {"start": v(317.43, 32.46) * mm, "end": v(314.26, 32.46) * mm});
            skLineSegment(sketch, "E1175", {"start": v(317.43, 23.22) * mm, "end": v(317.43, 32.46) * mm});
            skLineSegment(sketch, "E1176", {"start": v(317.43, 23.22) * mm, "end": v(314.26, 23.22) * mm});
            skLineSegment(sketch, "E1177", {"start": v(314.26, 14.2) * mm, "end": v(314.26, 23.22) * mm});
            skLineSegment(sketch, "E1178", {"start": v(-444.72, 68.84) * mm, "end": v(-444.72, 77.85) * mm});
            skLineSegment(sketch, "E1179", {"start": v(-441.55, 68.84) * mm, "end": v(-444.72, 68.84) * mm});
            skLineSegment(sketch, "E1180", {"start": v(-441.55, 59.6) * mm, "end": v(-441.55, 68.84) * mm});
            skLineSegment(sketch, "E1181", {"start": v(-441.55, 59.6) * mm, "end": v(-444.72, 59.6) * mm});
            skLineSegment(sketch, "E1182", {"start": v(-444.72, 50.65) * mm, "end": v(-444.72, 59.6) * mm});
            skLineSegment(sketch, "E1183", {"start": v(-441.55, 50.65) * mm, "end": v(-444.72, 50.65) * mm});
            skLineSegment(sketch, "E1184", {"start": v(-441.55, 41.4) * mm, "end": v(-441.55, 50.65) * mm});
            skLineSegment(sketch, "E1185", {"start": v(-441.55, 41.4) * mm, "end": v(-444.72, 41.4) * mm});
            skLineSegment(sketch, "E1186", {"start": v(-444.72, 32.46) * mm, "end": v(-444.72, 41.4) * mm});
            skLineSegment(sketch, "E1187", {"start": v(-441.55, 32.46) * mm, "end": v(-444.72, 32.46) * mm});
            skLineSegment(sketch, "E1188", {"start": v(-441.55, 23.22) * mm, "end": v(-441.55, 32.46) * mm});
            skLineSegment(sketch, "E1189", {"start": v(-441.55, 23.22) * mm, "end": v(-444.72, 23.22) * mm});
            skLineSegment(sketch, "E1190", {"start": v(-444.72, 23.22) * mm, "end": v(-444.72, 17.6) * mm});
            skLineSegment(sketch, "E1191", {"start": v(-444.72, 17.6) * mm, "end": v(-441.47, 17.6) * mm});
            skLineSegment(sketch, "E1192", {"start": v(-441.47, 17.6) * mm, "end": v(-441.47, 14.18) * mm});
            skLineSegment(sketch, "E1193", {"start": v(309.33, 77.85) * mm, "end": v(314.26, 77.85) * mm});
            skLineSegment(sketch, "E1194", {"start": v(309.33, 77.85) * mm, "end": v(309.33, 74.68) * mm});
            skLineSegment(sketch, "E1195", {"start": v(301.46, 74.68) * mm, "end": v(309.33, 74.68) * mm});
            skLineSegment(sketch, "E1196", {"start": v(301.46, 77.85) * mm, "end": v(301.46, 74.68) * mm});
            skLineSegment(sketch, "E1197", {"start": v(293.29, 77.85) * mm, "end": v(301.46, 77.85) * mm});
            skLineSegment(sketch, "E1198", {"start": v(293.29, 77.85) * mm, "end": v(293.29, 74.68) * mm});
            skLineSegment(sketch, "E1199", {"start": v(285.42, 74.68) * mm, "end": v(293.29, 74.68) * mm});
            skLineSegment(sketch, "E1200", {"start": v(285.42, 77.85) * mm, "end": v(285.42, 74.68) * mm});
            skLineSegment(sketch, "E1201", {"start": v(277.24, 77.85) * mm, "end": v(285.42, 77.85) * mm});
            skLineSegment(sketch, "E1202", {"start": v(277.24, 77.85) * mm, "end": v(277.24, 74.68) * mm});
            skLineSegment(sketch, "E1203", {"start": v(269.37, 74.68) * mm, "end": v(277.24, 74.68) * mm});
            skLineSegment(sketch, "E1204", {"start": v(269.37, 77.85) * mm, "end": v(269.37, 74.68) * mm});
            skLineSegment(sketch, "E1205", {"start": v(261.2, 77.85) * mm, "end": v(269.37, 77.85) * mm});
            skLineSegment(sketch, "E1206", {"start": v(261.2, 77.85) * mm, "end": v(261.2, 74.68) * mm});
            skLineSegment(sketch, "E1207", {"start": v(253.33, 74.68) * mm, "end": v(261.2, 74.68) * mm});
            skLineSegment(sketch, "E1208", {"start": v(253.33, 77.85) * mm, "end": v(253.33, 74.68) * mm});
            skLineSegment(sketch, "E1209", {"start": v(245.15, 77.85) * mm, "end": v(253.33, 77.85) * mm});
            skLineSegment(sketch, "E1210", {"start": v(245.15, 77.85) * mm, "end": v(245.15, 74.68) * mm});
            skLineSegment(sketch, "E1211", {"start": v(237.28, 74.68) * mm, "end": v(245.15, 74.68) * mm});
            skLineSegment(sketch, "E1212", {"start": v(237.28, 77.85) * mm, "end": v(237.28, 74.68) * mm});
            skLineSegment(sketch, "E1213", {"start": v(229.1, 77.85) * mm, "end": v(237.28, 77.85) * mm});
            skLineSegment(sketch, "E1214", {"start": v(229.1, 77.85) * mm, "end": v(229.1, 74.68) * mm});
            skLineSegment(sketch, "E1215", {"start": v(221.23, 74.68) * mm, "end": v(229.1, 74.68) * mm});
            skLineSegment(sketch, "E1216", {"start": v(221.23, 77.85) * mm, "end": v(221.23, 74.68) * mm});
            skLineSegment(sketch, "E1217", {"start": v(213.06, 77.85) * mm, "end": v(221.23, 77.85) * mm});
            skLineSegment(sketch, "E1218", {"start": v(213.06, 77.85) * mm, "end": v(213.06, 74.68) * mm});
            skLineSegment(sketch, "E1219", {"start": v(205.19, 74.68) * mm, "end": v(213.06, 74.68) * mm});
            skLineSegment(sketch, "E1220", {"start": v(205.19, 77.85) * mm, "end": v(205.19, 74.68) * mm});
            skLineSegment(sketch, "E1221", {"start": v(197.01, 77.85) * mm, "end": v(205.19, 77.85) * mm});
            skLineSegment(sketch, "E1222", {"start": v(197.01, 77.85) * mm, "end": v(197.01, 74.68) * mm});
            skLineSegment(sketch, "E1223", {"start": v(189.14, 74.68) * mm, "end": v(197.01, 74.68) * mm});
            skLineSegment(sketch, "E1224", {"start": v(189.14, 77.85) * mm, "end": v(189.14, 74.68) * mm});
            skLineSegment(sketch, "E1225", {"start": v(180.97, 77.85) * mm, "end": v(189.14, 77.85) * mm});
            skLineSegment(sketch, "E1226", {"start": v(180.97, 77.85) * mm, "end": v(180.97, 74.68) * mm});
            skLineSegment(sketch, "E1227", {"start": v(173.1, 74.68) * mm, "end": v(180.97, 74.68) * mm});
            skLineSegment(sketch, "E1228", {"start": v(173.1, 77.85) * mm, "end": v(173.1, 74.68) * mm});
            skLineSegment(sketch, "E1229", {"start": v(164.92, 77.85) * mm, "end": v(173.1, 77.85) * mm});
            skLineSegment(sketch, "E1230", {"start": v(164.92, 77.85) * mm, "end": v(164.92, 74.68) * mm});
            skLineSegment(sketch, "E1231", {"start": v(157.05, 74.68) * mm, "end": v(164.92, 74.68) * mm});
            skLineSegment(sketch, "E1232", {"start": v(157.05, 77.85) * mm, "end": v(157.05, 74.68) * mm});
            skLineSegment(sketch, "E1233", {"start": v(148.88, 77.85) * mm, "end": v(157.05, 77.85) * mm});
            skLineSegment(sketch, "E1234", {"start": v(148.88, 77.85) * mm, "end": v(148.88, 74.68) * mm});
            skLineSegment(sketch, "E1235", {"start": v(141, 74.68) * mm, "end": v(148.88, 74.68) * mm});
            skLineSegment(sketch, "E1236", {"start": v(141, 77.85) * mm, "end": v(141, 74.68) * mm});
            skLineSegment(sketch, "E1237", {"start": v(132.83, 77.85) * mm, "end": v(141, 77.85) * mm});
            skLineSegment(sketch, "E1238", {"start": v(132.83, 77.85) * mm, "end": v(132.83, 74.68) * mm});
            skLineSegment(sketch, "E1239", {"start": v(124.96, 74.68) * mm, "end": v(132.83, 74.68) * mm});
            skLineSegment(sketch, "E1240", {"start": v(124.96, 77.85) * mm, "end": v(124.96, 74.68) * mm});
            skLineSegment(sketch, "E1241", {"start": v(116.79, 77.85) * mm, "end": v(124.96, 77.85) * mm});
            skLineSegment(sketch, "E1242", {"start": v(116.79, 77.85) * mm, "end": v(116.79, 74.68) * mm});
            skLineSegment(sketch, "E1243", {"start": v(108.92, 74.68) * mm, "end": v(116.79, 74.68) * mm});
            skLineSegment(sketch, "E1244", {"start": v(108.92, 77.85) * mm, "end": v(108.92, 74.68) * mm});
            skLineSegment(sketch, "E1245", {"start": v(100.74, 77.85) * mm, "end": v(108.92, 77.85) * mm});
            skLineSegment(sketch, "E1246", {"start": v(100.74, 77.85) * mm, "end": v(100.74, 74.68) * mm});
            skLineSegment(sketch, "E1247", {"start": v(92.87, 74.68) * mm, "end": v(100.74, 74.68) * mm});
            skLineSegment(sketch, "E1248", {"start": v(92.87, 77.85) * mm, "end": v(92.87, 74.68) * mm});
            skLineSegment(sketch, "E1249", {"start": v(84.7, 77.85) * mm, "end": v(92.87, 77.85) * mm});
            skLineSegment(sketch, "E1250", {"start": v(84.7, 77.85) * mm, "end": v(84.7, 74.68) * mm});
            skLineSegment(sketch, "E1251", {"start": v(76.83, 74.68) * mm, "end": v(84.7, 74.68) * mm});
            skLineSegment(sketch, "E1252", {"start": v(76.83, 77.85) * mm, "end": v(76.83, 74.68) * mm});
            skLineSegment(sketch, "E1253", {"start": v(68.65, 77.85) * mm, "end": v(76.83, 77.85) * mm});
            skLineSegment(sketch, "E1254", {"start": v(68.65, 77.85) * mm, "end": v(68.65, 74.68) * mm});
            skLineSegment(sketch, "E1255", {"start": v(60.78, 74.68) * mm, "end": v(68.65, 74.68) * mm});
            skLineSegment(sketch, "E1256", {"start": v(60.78, 77.85) * mm, "end": v(60.78, 74.68) * mm});
            skLineSegment(sketch, "E1257", {"start": v(52.6, 77.85) * mm, "end": v(60.78, 77.85) * mm});
            skLineSegment(sketch, "E1258", {"start": v(52.6, 77.85) * mm, "end": v(52.6, 74.68) * mm});
            skLineSegment(sketch, "E1259", {"start": v(44.74, 74.68) * mm, "end": v(52.6, 74.68) * mm});
            skLineSegment(sketch, "E1260", {"start": v(44.74, 77.85) * mm, "end": v(44.74, 74.68) * mm});
            skLineSegment(sketch, "E1261", {"start": v(36.56, 77.85) * mm, "end": v(44.74, 77.85) * mm});
            skLineSegment(sketch, "E1262", {"start": v(36.56, 77.85) * mm, "end": v(36.56, 74.68) * mm});
            skLineSegment(sketch, "E1263", {"start": v(28.7, 74.68) * mm, "end": v(36.56, 74.68) * mm});
            skLineSegment(sketch, "E1264", {"start": v(28.7, 77.85) * mm, "end": v(28.7, 74.68) * mm});
            skLineSegment(sketch, "E1265", {"start": v(20.52, 77.85) * mm, "end": v(28.7, 77.85) * mm});
            skLineSegment(sketch, "E1266", {"start": v(20.52, 77.85) * mm, "end": v(20.52, 74.68) * mm});
            skLineSegment(sketch, "E1267", {"start": v(12.65, 74.68) * mm, "end": v(20.52, 74.68) * mm});
            skLineSegment(sketch, "E1268", {"start": v(12.65, 77.85) * mm, "end": v(12.65, 74.68) * mm});
            skLineSegment(sketch, "E1269", {"start": v(4.47, 77.85) * mm, "end": v(12.65, 77.85) * mm});
            skLineSegment(sketch, "E1270", {"start": v(4.47, 77.85) * mm, "end": v(4.47, 74.68) * mm});
            skLineSegment(sketch, "E1271", {"start": v(-3.4, 74.68) * mm, "end": v(4.47, 74.68) * mm});
            skLineSegment(sketch, "E1272", {"start": v(-3.4, 77.85) * mm, "end": v(-3.4, 74.68) * mm});
            skLineSegment(sketch, "E1273", {"start": v(-11.57, 77.85) * mm, "end": v(-3.4, 77.85) * mm});
            skLineSegment(sketch, "E1274", {"start": v(-11.57, 77.85) * mm, "end": v(-11.57, 74.68) * mm});
            skLineSegment(sketch, "E1275", {"start": v(-19.44, 74.68) * mm, "end": v(-11.57, 74.68) * mm});
            skLineSegment(sketch, "E1276", {"start": v(-19.44, 77.85) * mm, "end": v(-19.44, 74.68) * mm});
            skLineSegment(sketch, "E1277", {"start": v(-27.62, 77.85) * mm, "end": v(-19.44, 77.85) * mm});
            skLineSegment(sketch, "E1278", {"start": v(-27.62, 77.85) * mm, "end": v(-27.62, 74.68) * mm});
            skLineSegment(sketch, "E1279", {"start": v(-35.5, 74.68) * mm, "end": v(-27.62, 74.68) * mm});
            skLineSegment(sketch, "E1280", {"start": v(-35.5, 77.85) * mm, "end": v(-35.5, 74.68) * mm});
            skLineSegment(sketch, "E1281", {"start": v(-43.67, 77.85) * mm, "end": v(-35.5, 77.85) * mm});
            skLineSegment(sketch, "E1282", {"start": v(-43.67, 77.85) * mm, "end": v(-43.67, 74.68) * mm});
            skLineSegment(sketch, "E1283", {"start": v(-51.54, 74.68) * mm, "end": v(-43.67, 74.68) * mm});
            skLineSegment(sketch, "E1284", {"start": v(-51.54, 77.85) * mm, "end": v(-51.54, 74.68) * mm});
            skLineSegment(sketch, "E1285", {"start": v(-59.71, 77.85) * mm, "end": v(-51.54, 77.85) * mm});
            skLineSegment(sketch, "E1286", {"start": v(-59.71, 77.85) * mm, "end": v(-59.71, 74.68) * mm});
            skLineSegment(sketch, "E1287", {"start": v(-67.58, 74.68) * mm, "end": v(-59.71, 74.68) * mm});
            skLineSegment(sketch, "E1288", {"start": v(-67.58, 77.85) * mm, "end": v(-67.58, 74.68) * mm});
            skLineSegment(sketch, "E1289", {"start": v(-75.76, 77.85) * mm, "end": v(-67.58, 77.85) * mm});
            skLineSegment(sketch, "E1290", {"start": v(-75.76, 77.85) * mm, "end": v(-75.76, 74.68) * mm});
            skLineSegment(sketch, "E1291", {"start": v(-83.63, 74.68) * mm, "end": v(-75.76, 74.68) * mm});
            skLineSegment(sketch, "E1292", {"start": v(-83.63, 77.85) * mm, "end": v(-83.63, 74.68) * mm});
            skLineSegment(sketch, "E1293", {"start": v(-91.8, 77.85) * mm, "end": v(-83.63, 77.85) * mm});
            skLineSegment(sketch, "E1294", {"start": v(-91.8, 77.85) * mm, "end": v(-91.8, 74.68) * mm});
            skLineSegment(sketch, "E1295", {"start": v(-99.67, 74.68) * mm, "end": v(-91.8, 74.68) * mm});
            skLineSegment(sketch, "E1296", {"start": v(-99.67, 77.85) * mm, "end": v(-99.67, 74.68) * mm});
            skLineSegment(sketch, "E1297", {"start": v(-107.85, 77.85) * mm, "end": v(-99.67, 77.85) * mm});
            skLineSegment(sketch, "E1298", {"start": v(-107.85, 77.85) * mm, "end": v(-107.85, 74.68) * mm});
            skLineSegment(sketch, "E1299", {"start": v(-115.72, 74.68) * mm, "end": v(-107.85, 74.68) * mm});
            skLineSegment(sketch, "E1300", {"start": v(-115.72, 77.85) * mm, "end": v(-115.72, 74.68) * mm});
            skLineSegment(sketch, "E1301", {"start": v(-123.9, 77.85) * mm, "end": v(-115.72, 77.85) * mm});
            skLineSegment(sketch, "E1302", {"start": v(-123.9, 77.85) * mm, "end": v(-123.9, 74.68) * mm});
            skLineSegment(sketch, "E1303", {"start": v(-131.76, 74.68) * mm, "end": v(-123.9, 74.68) * mm});
            skLineSegment(sketch, "E1304", {"start": v(-131.76, 77.85) * mm, "end": v(-131.76, 74.68) * mm});
            skLineSegment(sketch, "E1305", {"start": v(-139.94, 77.85) * mm, "end": v(-131.76, 77.85) * mm});
            skLineSegment(sketch, "E1306", {"start": v(-139.94, 77.85) * mm, "end": v(-139.94, 74.68) * mm});
            skLineSegment(sketch, "E1307", {"start": v(-147.8, 74.68) * mm, "end": v(-139.94, 74.68) * mm});
            skLineSegment(sketch, "E1308", {"start": v(-147.8, 77.85) * mm, "end": v(-147.8, 74.68) * mm});
            skLineSegment(sketch, "E1309", {"start": v(-155.98, 77.85) * mm, "end": v(-147.8, 77.85) * mm});
            skLineSegment(sketch, "E1310", {"start": v(-155.98, 77.85) * mm, "end": v(-155.98, 74.68) * mm});
            skLineSegment(sketch, "E1311", {"start": v(-163.85, 74.68) * mm, "end": v(-155.98, 74.68) * mm});
            skLineSegment(sketch, "E1312", {"start": v(-163.85, 77.85) * mm, "end": v(-163.85, 74.68) * mm});
            skLineSegment(sketch, "E1313", {"start": v(-172.03, 77.85) * mm, "end": v(-163.85, 77.85) * mm});
            skLineSegment(sketch, "E1314", {"start": v(-172.03, 77.85) * mm, "end": v(-172.03, 74.68) * mm});
            skLineSegment(sketch, "E1315", {"start": v(-179.9, 74.68) * mm, "end": v(-172.03, 74.68) * mm});
            skLineSegment(sketch, "E1316", {"start": v(-179.9, 77.85) * mm, "end": v(-179.9, 74.68) * mm});
            skLineSegment(sketch, "E1317", {"start": v(-188.07, 77.85) * mm, "end": v(-179.9, 77.85) * mm});
            skLineSegment(sketch, "E1318", {"start": v(-188.07, 77.85) * mm, "end": v(-188.07, 74.68) * mm});
            skLineSegment(sketch, "E1319", {"start": v(-195.94, 74.68) * mm, "end": v(-188.07, 74.68) * mm});
            skLineSegment(sketch, "E1320", {"start": v(-195.94, 77.85) * mm, "end": v(-195.94, 74.68) * mm});
            skLineSegment(sketch, "E1321", {"start": v(-204.12, 77.85) * mm, "end": v(-195.94, 77.85) * mm});
            skLineSegment(sketch, "E1322", {"start": v(-204.12, 77.85) * mm, "end": v(-204.12, 74.68) * mm});
            skLineSegment(sketch, "E1323", {"start": v(-211.99, 74.68) * mm, "end": v(-204.12, 74.68) * mm});
            skLineSegment(sketch, "E1324", {"start": v(-211.99, 77.85) * mm, "end": v(-211.99, 74.68) * mm});
            skLineSegment(sketch, "E1325", {"start": v(-220.16, 77.85) * mm, "end": v(-211.99, 77.85) * mm});
            skLineSegment(sketch, "E1326", {"start": v(-220.16, 77.85) * mm, "end": v(-220.16, 74.68) * mm});
            skLineSegment(sketch, "E1327", {"start": v(-228.03, 74.68) * mm, "end": v(-220.16, 74.68) * mm});
            skLineSegment(sketch, "E1328", {"start": v(-228.03, 77.85) * mm, "end": v(-228.03, 74.68) * mm});
            skLineSegment(sketch, "E1329", {"start": v(-236.2, 77.85) * mm, "end": v(-228.03, 77.85) * mm});
            skLineSegment(sketch, "E1330", {"start": v(-236.2, 77.85) * mm, "end": v(-236.2, 74.68) * mm});
            skLineSegment(sketch, "E1331", {"start": v(-244.08, 74.68) * mm, "end": v(-236.2, 74.68) * mm});
            skLineSegment(sketch, "E1332", {"start": v(-244.08, 77.85) * mm, "end": v(-244.08, 74.68) * mm});
            skLineSegment(sketch, "E1333", {"start": v(-252.25, 77.85) * mm, "end": v(-244.08, 77.85) * mm});
            skLineSegment(sketch, "E1334", {"start": v(-252.25, 77.85) * mm, "end": v(-252.25, 74.68) * mm});
            skLineSegment(sketch, "E1335", {"start": v(-260.12, 74.68) * mm, "end": v(-252.25, 74.68) * mm});
            skLineSegment(sketch, "E1336", {"start": v(-260.12, 77.85) * mm, "end": v(-260.12, 74.68) * mm});
            skLineSegment(sketch, "E1337", {"start": v(-268.3, 77.85) * mm, "end": v(-260.12, 77.85) * mm});
            skLineSegment(sketch, "E1338", {"start": v(-268.3, 77.85) * mm, "end": v(-268.3, 74.68) * mm});
            skLineSegment(sketch, "E1339", {"start": v(-276.17, 74.68) * mm, "end": v(-268.3, 74.68) * mm});
            skLineSegment(sketch, "E1340", {"start": v(-276.17, 77.85) * mm, "end": v(-276.17, 74.68) * mm});
            skLineSegment(sketch, "E1341", {"start": v(-284.35, 77.85) * mm, "end": v(-276.17, 77.85) * mm});
            skLineSegment(sketch, "E1342", {"start": v(-284.35, 77.85) * mm, "end": v(-284.35, 74.68) * mm});
            skLineSegment(sketch, "E1343", {"start": v(-292.22, 74.68) * mm, "end": v(-284.35, 74.68) * mm});
            skLineSegment(sketch, "E1344", {"start": v(-292.22, 77.85) * mm, "end": v(-292.22, 74.68) * mm});
            skLineSegment(sketch, "E1345", {"start": v(-300.4, 77.85) * mm, "end": v(-292.22, 77.85) * mm});
            skLineSegment(sketch, "E1346", {"start": v(-300.4, 77.85) * mm, "end": v(-300.4, 74.68) * mm});
            skLineSegment(sketch, "E1347", {"start": v(-308.26, 74.68) * mm, "end": v(-300.4, 74.68) * mm});
            skLineSegment(sketch, "E1348", {"start": v(-308.26, 77.85) * mm, "end": v(-308.26, 74.68) * mm});
            skLineSegment(sketch, "E1349", {"start": v(-316.44, 77.85) * mm, "end": v(-308.26, 77.85) * mm});
            skLineSegment(sketch, "E1350", {"start": v(-316.44, 77.85) * mm, "end": v(-316.44, 74.68) * mm});
            skLineSegment(sketch, "E1351", {"start": v(-324.3, 74.68) * mm, "end": v(-316.44, 74.68) * mm});
            skLineSegment(sketch, "E1352", {"start": v(-324.3, 77.85) * mm, "end": v(-324.3, 74.68) * mm});
            skLineSegment(sketch, "E1353", {"start": v(-332.48, 77.85) * mm, "end": v(-324.3, 77.85) * mm});
            skLineSegment(sketch, "E1354", {"start": v(-332.48, 77.85) * mm, "end": v(-332.48, 74.68) * mm});
            skLineSegment(sketch, "E1355", {"start": v(-340.35, 74.68) * mm, "end": v(-332.48, 74.68) * mm});
            skLineSegment(sketch, "E1356", {"start": v(-340.35, 77.85) * mm, "end": v(-340.35, 74.68) * mm});
            skLineSegment(sketch, "E1357", {"start": v(-348.53, 77.85) * mm, "end": v(-340.35, 77.85) * mm});
            skLineSegment(sketch, "E1358", {"start": v(-348.53, 77.85) * mm, "end": v(-348.53, 74.68) * mm});
            skLineSegment(sketch, "E1359", {"start": v(-356.4, 74.68) * mm, "end": v(-348.53, 74.68) * mm});
            skLineSegment(sketch, "E1360", {"start": v(-356.4, 77.85) * mm, "end": v(-356.4, 74.68) * mm});
            skLineSegment(sketch, "E1361", {"start": v(-364.57, 77.85) * mm, "end": v(-356.4, 77.85) * mm});
            skLineSegment(sketch, "E1362", {"start": v(-364.57, 77.85) * mm, "end": v(-364.57, 74.68) * mm});
            skLineSegment(sketch, "E1363", {"start": v(-372.44, 74.68) * mm, "end": v(-364.57, 74.68) * mm});
            skLineSegment(sketch, "E1364", {"start": v(-372.44, 77.85) * mm, "end": v(-372.44, 74.68) * mm});
            skLineSegment(sketch, "E1365", {"start": v(-380.62, 77.85) * mm, "end": v(-372.44, 77.85) * mm});
            skLineSegment(sketch, "E1366", {"start": v(-380.62, 77.85) * mm, "end": v(-380.62, 74.68) * mm});
            skLineSegment(sketch, "E1367", {"start": v(-388.49, 74.68) * mm, "end": v(-380.62, 74.68) * mm});
            skLineSegment(sketch, "E1368", {"start": v(-388.49, 77.85) * mm, "end": v(-388.49, 74.68) * mm});
            skLineSegment(sketch, "E1369", {"start": v(-396.66, 77.85) * mm, "end": v(-388.49, 77.85) * mm});
            skLineSegment(sketch, "E1370", {"start": v(-396.66, 77.85) * mm, "end": v(-396.66, 74.68) * mm});
            skLineSegment(sketch, "E1371", {"start": v(-404.53, 74.68) * mm, "end": v(-396.66, 74.68) * mm});
            skLineSegment(sketch, "E1372", {"start": v(-404.53, 77.85) * mm, "end": v(-404.53, 74.68) * mm});
            skLineSegment(sketch, "E1373", {"start": v(-412.7, 77.85) * mm, "end": v(-404.53, 77.85) * mm});
            skLineSegment(sketch, "E1374", {"start": v(-412.7, 77.85) * mm, "end": v(-412.7, 74.68) * mm});
            skLineSegment(sketch, "E1375", {"start": v(-420.58, 74.68) * mm, "end": v(-412.7, 74.68) * mm});
            skLineSegment(sketch, "E1376", {"start": v(-420.58, 77.85) * mm, "end": v(-420.58, 74.68) * mm});
            skLineSegment(sketch, "E1377", {"start": v(-428.75, 77.85) * mm, "end": v(-420.58, 77.85) * mm});
            skLineSegment(sketch, "E1378", {"start": v(-428.75, 77.85) * mm, "end": v(-428.75, 74.68) * mm});
            skLineSegment(sketch, "E1379", {"start": v(-436.62, 74.68) * mm, "end": v(-428.75, 74.68) * mm});
            skLineSegment(sketch, "E1380", {"start": v(-436.62, 77.85) * mm, "end": v(-436.62, 74.68) * mm});
            skLineSegment(sketch, "E1381", {"start": v(-444.72, 77.85) * mm, "end": v(-436.62, 77.85) * mm});
            skLineSegment(sketch, "E1382", {"start": v(309.33, 14.2) * mm, "end": v(314.26, 14.2) * mm});
            skLineSegment(sketch, "E1383", {"start": v(309.33, 17.38) * mm, "end": v(309.33, 14.2) * mm});
            skLineSegment(sketch, "E1384", {"start": v(301.46, 17.38) * mm, "end": v(309.33, 17.38) * mm});
            skLineSegment(sketch, "E1385", {"start": v(301.46, 17.38) * mm, "end": v(301.46, 14.2) * mm});
            skLineSegment(sketch, "E1386", {"start": v(293.29, 14.2) * mm, "end": v(301.46, 14.2) * mm});
            skLineSegment(sketch, "E1387", {"start": v(293.29, 17.38) * mm, "end": v(293.29, 14.2) * mm});
            skLineSegment(sketch, "E1388", {"start": v(285.42, 17.38) * mm, "end": v(293.29, 17.38) * mm});
            skLineSegment(sketch, "E1389", {"start": v(285.42, 17.38) * mm, "end": v(285.42, 14.2) * mm});
            skLineSegment(sketch, "E1390", {"start": v(277.24, 14.2) * mm, "end": v(285.42, 14.2) * mm});
            skLineSegment(sketch, "E1391", {"start": v(277.24, 17.38) * mm, "end": v(277.24, 14.2) * mm});
            skLineSegment(sketch, "E1392", {"start": v(269.37, 17.38) * mm, "end": v(277.24, 17.38) * mm});
            skLineSegment(sketch, "E1393", {"start": v(269.37, 17.38) * mm, "end": v(269.37, 14.2) * mm});
            skLineSegment(sketch, "E1394", {"start": v(261.2, 14.2) * mm, "end": v(269.37, 14.2) * mm});
            skLineSegment(sketch, "E1395", {"start": v(261.2, 17.38) * mm, "end": v(261.2, 14.2) * mm});
            skLineSegment(sketch, "E1396", {"start": v(253.33, 17.38) * mm, "end": v(261.2, 17.38) * mm});
            skLineSegment(sketch, "E1397", {"start": v(253.33, 17.38) * mm, "end": v(253.33, 14.2) * mm});
            skLineSegment(sketch, "E1398", {"start": v(245.15, 14.2) * mm, "end": v(253.33, 14.2) * mm});
            skLineSegment(sketch, "E1399", {"start": v(245.15, 17.38) * mm, "end": v(245.15, 14.2) * mm});
            skLineSegment(sketch, "E1400", {"start": v(237.28, 17.38) * mm, "end": v(245.15, 17.38) * mm});
            skLineSegment(sketch, "E1401", {"start": v(237.28, 17.38) * mm, "end": v(237.28, 14.2) * mm});
            skLineSegment(sketch, "E1402", {"start": v(229.1, 14.2) * mm, "end": v(237.28, 14.2) * mm});
            skLineSegment(sketch, "E1403", {"start": v(229.1, 17.38) * mm, "end": v(229.1, 14.2) * mm});
            skLineSegment(sketch, "E1404", {"start": v(221.23, 17.38) * mm, "end": v(229.1, 17.38) * mm});
            skLineSegment(sketch, "E1405", {"start": v(221.23, 17.38) * mm, "end": v(221.23, 14.2) * mm});
            skLineSegment(sketch, "E1406", {"start": v(213.06, 14.2) * mm, "end": v(221.23, 14.2) * mm});
            skLineSegment(sketch, "E1407", {"start": v(213.06, 17.38) * mm, "end": v(213.06, 14.2) * mm});
            skLineSegment(sketch, "E1408", {"start": v(205.19, 17.38) * mm, "end": v(213.06, 17.38) * mm});
            skLineSegment(sketch, "E1409", {"start": v(205.19, 17.38) * mm, "end": v(205.19, 14.2) * mm});
            skLineSegment(sketch, "E1410", {"start": v(197.01, 14.2) * mm, "end": v(205.19, 14.2) * mm});
            skLineSegment(sketch, "E1411", {"start": v(197.01, 17.38) * mm, "end": v(197.01, 14.2) * mm});
            skLineSegment(sketch, "E1412", {"start": v(189.14, 17.38) * mm, "end": v(197.01, 17.38) * mm});
            skLineSegment(sketch, "E1413", {"start": v(189.14, 17.38) * mm, "end": v(189.14, 14.2) * mm});
            skLineSegment(sketch, "E1414", {"start": v(180.97, 14.2) * mm, "end": v(189.14, 14.2) * mm});
            skLineSegment(sketch, "E1415", {"start": v(180.97, 17.38) * mm, "end": v(180.97, 14.2) * mm});
            skLineSegment(sketch, "E1416", {"start": v(173.1, 17.38) * mm, "end": v(180.97, 17.38) * mm});
            skLineSegment(sketch, "E1417", {"start": v(173.1, 17.38) * mm, "end": v(173.1, 14.2) * mm});
            skLineSegment(sketch, "E1418", {"start": v(164.92, 14.2) * mm, "end": v(173.1, 14.2) * mm});
            skLineSegment(sketch, "E1419", {"start": v(164.92, 17.38) * mm, "end": v(164.92, 14.2) * mm});
            skLineSegment(sketch, "E1420", {"start": v(157.05, 17.38) * mm, "end": v(164.92, 17.38) * mm});
            skLineSegment(sketch, "E1421", {"start": v(157.05, 17.38) * mm, "end": v(157.05, 14.2) * mm});
            skLineSegment(sketch, "E1422", {"start": v(148.88, 14.2) * mm, "end": v(157.05, 14.2) * mm});
            skLineSegment(sketch, "E1423", {"start": v(148.88, 17.38) * mm, "end": v(148.88, 14.2) * mm});
            skLineSegment(sketch, "E1424", {"start": v(141, 17.38) * mm, "end": v(148.88, 17.38) * mm});
            skLineSegment(sketch, "E1425", {"start": v(141, 17.38) * mm, "end": v(141, 14.2) * mm});
            skLineSegment(sketch, "E1426", {"start": v(132.83, 14.2) * mm, "end": v(141, 14.2) * mm});
            skLineSegment(sketch, "E1427", {"start": v(132.83, 17.38) * mm, "end": v(132.83, 14.2) * mm});
            skLineSegment(sketch, "E1428", {"start": v(124.96, 17.38) * mm, "end": v(132.83, 17.38) * mm});
            skLineSegment(sketch, "E1429", {"start": v(124.96, 17.38) * mm, "end": v(124.96, 14.2) * mm});
            skLineSegment(sketch, "E1430", {"start": v(116.79, 14.2) * mm, "end": v(124.96, 14.2) * mm});
            skLineSegment(sketch, "E1431", {"start": v(116.79, 17.38) * mm, "end": v(116.79, 14.2) * mm});
            skLineSegment(sketch, "E1432", {"start": v(108.92, 17.38) * mm, "end": v(116.79, 17.38) * mm});
            skLineSegment(sketch, "E1433", {"start": v(108.92, 17.38) * mm, "end": v(108.92, 14.2) * mm});
            skLineSegment(sketch, "E1434", {"start": v(100.74, 14.2) * mm, "end": v(108.92, 14.2) * mm});
            skLineSegment(sketch, "E1435", {"start": v(100.74, 17.38) * mm, "end": v(100.74, 14.2) * mm});
            skLineSegment(sketch, "E1436", {"start": v(92.87, 17.38) * mm, "end": v(100.74, 17.38) * mm});
            skLineSegment(sketch, "E1437", {"start": v(92.87, 17.38) * mm, "end": v(92.87, 14.2) * mm});
            skLineSegment(sketch, "E1438", {"start": v(84.7, 14.2) * mm, "end": v(92.87, 14.2) * mm});
            skLineSegment(sketch, "E1439", {"start": v(84.7, 17.38) * mm, "end": v(84.7, 14.2) * mm});
            skLineSegment(sketch, "E1440", {"start": v(76.83, 17.38) * mm, "end": v(84.7, 17.38) * mm});
            skLineSegment(sketch, "E1441", {"start": v(76.83, 17.38) * mm, "end": v(76.83, 14.2) * mm});
            skLineSegment(sketch, "E1442", {"start": v(68.65, 14.2) * mm, "end": v(76.83, 14.2) * mm});
            skLineSegment(sketch, "E1443", {"start": v(68.65, 17.38) * mm, "end": v(68.65, 14.2) * mm});
            skLineSegment(sketch, "E1444", {"start": v(60.78, 17.38) * mm, "end": v(68.65, 17.38) * mm});
            skLineSegment(sketch, "E1445", {"start": v(60.78, 17.38) * mm, "end": v(60.78, 14.2) * mm});
            skLineSegment(sketch, "E1446", {"start": v(52.6, 14.2) * mm, "end": v(60.78, 14.2) * mm});
            skLineSegment(sketch, "E1447", {"start": v(52.6, 17.38) * mm, "end": v(52.6, 14.2) * mm});
            skLineSegment(sketch, "E1448", {"start": v(44.74, 17.38) * mm, "end": v(52.6, 17.38) * mm});
            skLineSegment(sketch, "E1449", {"start": v(44.74, 17.38) * mm, "end": v(44.74, 14.2) * mm});
            skLineSegment(sketch, "E1450", {"start": v(36.56, 14.2) * mm, "end": v(44.74, 14.2) * mm});
            skLineSegment(sketch, "E1451", {"start": v(36.56, 17.38) * mm, "end": v(36.56, 14.2) * mm});
            skLineSegment(sketch, "E1452", {"start": v(28.7, 17.38) * mm, "end": v(36.56, 17.38) * mm});
            skLineSegment(sketch, "E1453", {"start": v(28.7, 17.38) * mm, "end": v(28.7, 14.2) * mm});
            skLineSegment(sketch, "E1454", {"start": v(20.52, 14.2) * mm, "end": v(28.7, 14.2) * mm});
            skLineSegment(sketch, "E1455", {"start": v(20.52, 17.38) * mm, "end": v(20.52, 14.2) * mm});
            skLineSegment(sketch, "E1456", {"start": v(12.65, 17.38) * mm, "end": v(20.52, 17.38) * mm});
            skLineSegment(sketch, "E1457", {"start": v(12.65, 17.38) * mm, "end": v(12.65, 14.2) * mm});
            skLineSegment(sketch, "E1458", {"start": v(4.47, 14.2) * mm, "end": v(12.65, 14.2) * mm});
            skLineSegment(sketch, "E1459", {"start": v(4.47, 17.38) * mm, "end": v(4.47, 14.2) * mm});
            skLineSegment(sketch, "E1460", {"start": v(-3.4, 17.38) * mm, "end": v(4.47, 17.38) * mm});
            skLineSegment(sketch, "E1461", {"start": v(-3.4, 17.38) * mm, "end": v(-3.4, 14.2) * mm});
            skLineSegment(sketch, "E1462", {"start": v(-11.57, 14.2) * mm, "end": v(-3.4, 14.2) * mm});
            skLineSegment(sketch, "E1463", {"start": v(-11.57, 17.38) * mm, "end": v(-11.57, 14.2) * mm});
            skLineSegment(sketch, "E1464", {"start": v(-19.44, 17.38) * mm, "end": v(-11.57, 17.38) * mm});
            skLineSegment(sketch, "E1465", {"start": v(-19.44, 17.38) * mm, "end": v(-19.44, 14.2) * mm});
            skLineSegment(sketch, "E1466", {"start": v(-27.62, 14.2) * mm, "end": v(-19.44, 14.2) * mm});
            skLineSegment(sketch, "E1467", {"start": v(-27.62, 17.38) * mm, "end": v(-27.62, 14.2) * mm});
            skLineSegment(sketch, "E1468", {"start": v(-35.5, 17.38) * mm, "end": v(-27.62, 17.38) * mm});
            skLineSegment(sketch, "E1469", {"start": v(-35.5, 17.38) * mm, "end": v(-35.5, 14.2) * mm});
            skLineSegment(sketch, "E1470", {"start": v(-43.67, 14.2) * mm, "end": v(-35.5, 14.2) * mm});
            skLineSegment(sketch, "E1471", {"start": v(-43.67, 17.38) * mm, "end": v(-43.67, 14.2) * mm});
            skLineSegment(sketch, "E1472", {"start": v(-51.54, 17.38) * mm, "end": v(-43.67, 17.38) * mm});
            skLineSegment(sketch, "E1473", {"start": v(-51.54, 17.38) * mm, "end": v(-51.54, 14.2) * mm});
            skLineSegment(sketch, "E1474", {"start": v(-59.71, 14.2) * mm, "end": v(-51.54, 14.2) * mm});
            skLineSegment(sketch, "E1475", {"start": v(-59.71, 17.38) * mm, "end": v(-59.71, 14.2) * mm});
            skLineSegment(sketch, "E1476", {"start": v(-67.58, 17.38) * mm, "end": v(-59.71, 17.38) * mm});
            skLineSegment(sketch, "E1477", {"start": v(-67.58, 17.38) * mm, "end": v(-67.58, 14.2) * mm});
            skLineSegment(sketch, "E1478", {"start": v(-75.76, 14.2) * mm, "end": v(-67.58, 14.2) * mm});
            skLineSegment(sketch, "E1479", {"start": v(-75.76, 17.38) * mm, "end": v(-75.76, 14.2) * mm});
            skLineSegment(sketch, "E1480", {"start": v(-83.63, 17.38) * mm, "end": v(-75.76, 17.38) * mm});
            skLineSegment(sketch, "E1481", {"start": v(-83.63, 17.38) * mm, "end": v(-83.63, 14.2) * mm});
            skLineSegment(sketch, "E1482", {"start": v(-91.8, 14.2) * mm, "end": v(-83.63, 14.2) * mm});
            skLineSegment(sketch, "E1483", {"start": v(-91.8, 17.38) * mm, "end": v(-91.8, 14.2) * mm});
            skLineSegment(sketch, "E1484", {"start": v(-99.67, 17.38) * mm, "end": v(-91.8, 17.38) * mm});
            skLineSegment(sketch, "E1485", {"start": v(-99.67, 17.38) * mm, "end": v(-99.67, 14.2) * mm});
            skLineSegment(sketch, "E1486", {"start": v(-107.85, 14.2) * mm, "end": v(-99.67, 14.2) * mm});
            skLineSegment(sketch, "E1487", {"start": v(-107.85, 17.38) * mm, "end": v(-107.85, 14.2) * mm});
            skLineSegment(sketch, "E1488", {"start": v(-115.72, 17.38) * mm, "end": v(-107.85, 17.38) * mm});
            skLineSegment(sketch, "E1489", {"start": v(-115.72, 17.38) * mm, "end": v(-115.72, 14.2) * mm});
            skLineSegment(sketch, "E1490", {"start": v(-123.9, 14.2) * mm, "end": v(-115.72, 14.2) * mm});
            skLineSegment(sketch, "E1491", {"start": v(-123.9, 17.38) * mm, "end": v(-123.9, 14.2) * mm});
            skLineSegment(sketch, "E1492", {"start": v(-131.76, 17.38) * mm, "end": v(-123.9, 17.38) * mm});
            skLineSegment(sketch, "E1493", {"start": v(-131.76, 17.38) * mm, "end": v(-131.76, 14.2) * mm});
            skLineSegment(sketch, "E1494", {"start": v(-139.94, 14.2) * mm, "end": v(-131.76, 14.2) * mm});
            skLineSegment(sketch, "E1495", {"start": v(-139.94, 17.38) * mm, "end": v(-139.94, 14.2) * mm});
            skLineSegment(sketch, "E1496", {"start": v(-147.8, 17.38) * mm, "end": v(-139.94, 17.38) * mm});
            skLineSegment(sketch, "E1497", {"start": v(-147.8, 17.38) * mm, "end": v(-147.8, 14.2) * mm});
            skLineSegment(sketch, "E1498", {"start": v(-155.98, 14.2) * mm, "end": v(-147.8, 14.2) * mm});
            skLineSegment(sketch, "E1499", {"start": v(-155.98, 17.38) * mm, "end": v(-155.98, 14.2) * mm});
            skLineSegment(sketch, "E1500", {"start": v(-163.85, 17.38) * mm, "end": v(-155.98, 17.38) * mm});
            skLineSegment(sketch, "E1501", {"start": v(-163.85, 17.38) * mm, "end": v(-163.85, 14.2) * mm});
            skLineSegment(sketch, "E1502", {"start": v(-172.03, 14.2) * mm, "end": v(-163.85, 14.2) * mm});
            skLineSegment(sketch, "E1503", {"start": v(-172.03, 17.38) * mm, "end": v(-172.03, 14.2) * mm});
            skLineSegment(sketch, "E1504", {"start": v(-179.9, 17.38) * mm, "end": v(-172.03, 17.38) * mm});
            skLineSegment(sketch, "E1505", {"start": v(-179.9, 17.38) * mm, "end": v(-179.9, 14.2) * mm});
            skLineSegment(sketch, "E1506", {"start": v(-188.07, 14.2) * mm, "end": v(-179.9, 14.2) * mm});
            skLineSegment(sketch, "E1507", {"start": v(-188.07, 17.38) * mm, "end": v(-188.07, 14.2) * mm});
            skLineSegment(sketch, "E1508", {"start": v(-195.94, 17.38) * mm, "end": v(-188.07, 17.38) * mm});
            skLineSegment(sketch, "E1509", {"start": v(-195.94, 17.38) * mm, "end": v(-195.94, 14.2) * mm});
            skLineSegment(sketch, "E1510", {"start": v(-204.12, 14.2) * mm, "end": v(-195.94, 14.2) * mm});
            skLineSegment(sketch, "E1511", {"start": v(-204.12, 17.38) * mm, "end": v(-204.12, 14.2) * mm});
            skLineSegment(sketch, "E1512", {"start": v(-211.99, 17.38) * mm, "end": v(-204.12, 17.38) * mm});
            skLineSegment(sketch, "E1513", {"start": v(-211.99, 17.38) * mm, "end": v(-211.99, 14.2) * mm});
            skLineSegment(sketch, "E1514", {"start": v(-220.16, 14.2) * mm, "end": v(-211.99, 14.2) * mm});
            skLineSegment(sketch, "E1515", {"start": v(-220.16, 17.38) * mm, "end": v(-220.16, 14.2) * mm});
            skLineSegment(sketch, "E1516", {"start": v(-228.03, 17.38) * mm, "end": v(-220.16, 17.38) * mm});
            skLineSegment(sketch, "E1517", {"start": v(-228.03, 17.38) * mm, "end": v(-228.03, 14.2) * mm});
            skLineSegment(sketch, "E1518", {"start": v(-236.2, 14.2) * mm, "end": v(-228.03, 14.2) * mm});
            skLineSegment(sketch, "E1519", {"start": v(-236.2, 17.38) * mm, "end": v(-236.2, 14.2) * mm});
            skLineSegment(sketch, "E1520", {"start": v(-244.08, 17.38) * mm, "end": v(-236.2, 17.38) * mm});
            skLineSegment(sketch, "E1521", {"start": v(-244.08, 17.38) * mm, "end": v(-244.08, 14.2) * mm});
            skLineSegment(sketch, "E1522", {"start": v(-252.25, 14.2) * mm, "end": v(-244.08, 14.2) * mm});
            skLineSegment(sketch, "E1523", {"start": v(-252.25, 17.38) * mm, "end": v(-252.25, 14.2) * mm});
            skLineSegment(sketch, "E1524", {"start": v(-260.12, 17.38) * mm, "end": v(-252.25, 17.38) * mm});
            skLineSegment(sketch, "E1525", {"start": v(-260.12, 17.38) * mm, "end": v(-260.12, 14.2) * mm});
            skLineSegment(sketch, "E1526", {"start": v(-268.3, 14.2) * mm, "end": v(-260.12, 14.2) * mm});
            skLineSegment(sketch, "E1527", {"start": v(-268.3, 17.38) * mm, "end": v(-268.3, 14.2) * mm});
            skLineSegment(sketch, "E1528", {"start": v(-276.17, 17.38) * mm, "end": v(-268.3, 17.38) * mm});
            skLineSegment(sketch, "E1529", {"start": v(-276.17, 17.38) * mm, "end": v(-276.17, 14.2) * mm});
            skLineSegment(sketch, "E1530", {"start": v(-284.35, 14.2) * mm, "end": v(-276.17, 14.2) * mm});
            skLineSegment(sketch, "E1531", {"start": v(-284.35, 17.38) * mm, "end": v(-284.35, 14.2) * mm});
            skLineSegment(sketch, "E1532", {"start": v(-292.22, 17.38) * mm, "end": v(-284.35, 17.38) * mm});
            skLineSegment(sketch, "E1533", {"start": v(-292.22, 17.38) * mm, "end": v(-292.22, 14.2) * mm});
            skLineSegment(sketch, "E1534", {"start": v(-300.4, 14.2) * mm, "end": v(-292.22, 14.2) * mm});
            skLineSegment(sketch, "E1535", {"start": v(-300.4, 17.38) * mm, "end": v(-300.4, 14.2) * mm});
            skLineSegment(sketch, "E1536", {"start": v(-308.26, 17.38) * mm, "end": v(-300.4, 17.38) * mm});
            skLineSegment(sketch, "E1537", {"start": v(-308.26, 17.38) * mm, "end": v(-308.26, 14.2) * mm});
            skLineSegment(sketch, "E1538", {"start": v(-316.44, 14.2) * mm, "end": v(-308.26, 14.2) * mm});
            skLineSegment(sketch, "E1539", {"start": v(-316.44, 17.38) * mm, "end": v(-316.44, 14.2) * mm});
            skLineSegment(sketch, "E1540", {"start": v(-324.3, 17.38) * mm, "end": v(-316.44, 17.38) * mm});
            skLineSegment(sketch, "E1541", {"start": v(-324.3, 17.38) * mm, "end": v(-324.3, 14.2) * mm});
            skLineSegment(sketch, "E1542", {"start": v(-332.48, 14.2) * mm, "end": v(-324.3, 14.2) * mm});
            skLineSegment(sketch, "E1543", {"start": v(-332.48, 17.38) * mm, "end": v(-332.48, 14.2) * mm});
            skLineSegment(sketch, "E1544", {"start": v(-340.35, 17.38) * mm, "end": v(-332.48, 17.38) * mm});
            skLineSegment(sketch, "E1545", {"start": v(-340.35, 17.38) * mm, "end": v(-340.35, 14.2) * mm});
            skLineSegment(sketch, "E1546", {"start": v(-348.53, 14.2) * mm, "end": v(-340.35, 14.2) * mm});
            skLineSegment(sketch, "E1547", {"start": v(-348.53, 17.38) * mm, "end": v(-348.53, 14.2) * mm});
            skLineSegment(sketch, "E1548", {"start": v(-356.4, 17.38) * mm, "end": v(-348.53, 17.38) * mm});
            skLineSegment(sketch, "E1549", {"start": v(-356.4, 17.38) * mm, "end": v(-356.4, 14.2) * mm});
            skLineSegment(sketch, "E1550", {"start": v(-364.57, 14.2) * mm, "end": v(-356.4, 14.2) * mm});
            skLineSegment(sketch, "E1551", {"start": v(-364.57, 17.38) * mm, "end": v(-364.57, 14.2) * mm});
            skLineSegment(sketch, "E1552", {"start": v(-372.44, 17.38) * mm, "end": v(-364.57, 17.38) * mm});
            skLineSegment(sketch, "E1553", {"start": v(-372.44, 17.38) * mm, "end": v(-372.44, 14.2) * mm});
            skLineSegment(sketch, "E1554", {"start": v(-380.62, 14.2) * mm, "end": v(-372.44, 14.2) * mm});
            skLineSegment(sketch, "E1555", {"start": v(-380.62, 17.38) * mm, "end": v(-380.62, 14.2) * mm});
            skLineSegment(sketch, "E1556", {"start": v(-388.49, 17.38) * mm, "end": v(-380.62, 17.38) * mm});
            skLineSegment(sketch, "E1557", {"start": v(-388.49, 17.38) * mm, "end": v(-388.49, 14.2) * mm});
            skLineSegment(sketch, "E1558", {"start": v(-396.66, 14.2) * mm, "end": v(-388.49, 14.2) * mm});
            skLineSegment(sketch, "E1559", {"start": v(-396.66, 17.38) * mm, "end": v(-396.66, 14.2) * mm});
            skLineSegment(sketch, "E1560", {"start": v(-404.53, 17.38) * mm, "end": v(-396.66, 17.38) * mm});
            skLineSegment(sketch, "E1561", {"start": v(-404.53, 17.38) * mm, "end": v(-404.53, 14.2) * mm});
            skLineSegment(sketch, "E1562", {"start": v(-412.7, 14.2) * mm, "end": v(-404.53, 14.2) * mm});
            skLineSegment(sketch, "E1563", {"start": v(-412.7, 17.38) * mm, "end": v(-412.7, 14.2) * mm});
            skLineSegment(sketch, "E1564", {"start": v(-420.58, 17.38) * mm, "end": v(-412.7, 17.38) * mm});
            skLineSegment(sketch, "E1565", {"start": v(-420.58, 17.38) * mm, "end": v(-420.58, 14.2) * mm});
            skLineSegment(sketch, "E1566", {"start": v(-428.75, 14.2) * mm, "end": v(-420.58, 14.2) * mm});
            skLineSegment(sketch, "E1567", {"start": v(-428.75, 17.38) * mm, "end": v(-428.75, 14.2) * mm});
            skLineSegment(sketch, "E1568", {"start": v(-436.62, 17.38) * mm, "end": v(-428.75, 17.38) * mm});
            skLineSegment(sketch, "E1569", {"start": v(-436.62, 17.38) * mm, "end": v(-436.62, 14.2) * mm});
            skFitSpline(sketch, "E1570", {"points": [v(-386.73, 66.72) * mm, v(-386.72, 66.1) * mm, v(-387.06, 65.52) * mm, v(-387.6, 65.2) * mm]});
            skFitSpline(sketch, "E1571", {"points": [v(-387.6, 65.2) * mm, v(-388.14, 64.9) * mm, v(-388.8, 64.9) * mm, v(-389.34, 65.2) * mm]});
            skFitSpline(sketch, "E1572", {"points": [v(-389.34, 65.2) * mm, v(-389.88, 65.52) * mm, v(-390.21, 66.1) * mm, v(-390.21, 66.72) * mm]});
            skFitSpline(sketch, "E1573", {"points": [v(-390.21, 66.72) * mm, v(-390.21, 67.35) * mm, v(-389.88, 67.92) * mm, v(-389.34, 68.24) * mm]});
            skFitSpline(sketch, "E1574", {"points": [v(-389.34, 68.24) * mm, v(-388.8, 68.55) * mm, v(-388.14, 68.55) * mm, v(-387.6, 68.24) * mm]});
            skFitSpline(sketch, "E1575", {"points": [v(-387.6, 68.24) * mm, v(-387.06, 67.92) * mm, v(-386.72, 67.35) * mm, v(-386.73, 66.72) * mm]});
            skLineSegment(sketch, "E1576", {"start": v(-441.47, 14.2) * mm, "end": v(-436.62, 14.2) * mm});
            skFitSpline(sketch, "E1577", {"points": [v(-323.43, 66.72) * mm, v(-323.42, 66.1) * mm, v(-323.76, 65.52) * mm, v(-324.3, 65.2) * mm]});
            skFitSpline(sketch, "E1578", {"points": [v(-324.3, 65.2) * mm, v(-324.84, 64.9) * mm, v(-325.5, 64.9) * mm, v(-326.04, 65.2) * mm]});
            skFitSpline(sketch, "E1579", {"points": [v(-326.04, 65.2) * mm, v(-326.58, 65.52) * mm, v(-326.91, 66.1) * mm, v(-326.91, 66.72) * mm]});
            skFitSpline(sketch, "E1580", {"points": [v(-326.91, 66.72) * mm, v(-326.91, 67.35) * mm, v(-326.58, 67.92) * mm, v(-326.04, 68.24) * mm]});
            skFitSpline(sketch, "E1581", {"points": [v(-326.04, 68.24) * mm, v(-325.5, 68.55) * mm, v(-324.84, 68.55) * mm, v(-324.3, 68.24) * mm]});
            skFitSpline(sketch, "E1582", {"points": [v(-324.3, 68.24) * mm, v(-323.76, 67.92) * mm, v(-323.42, 67.35) * mm, v(-323.43, 66.72) * mm]});
            skFitSpline(sketch, "E1583", {"points": [v(-260.13, 66.72) * mm, v(-260.12, 66.1) * mm, v(-260.46, 65.52) * mm, v(-261, 65.2) * mm]});
            skFitSpline(sketch, "E1584", {"points": [v(-261, 65.2) * mm, v(-261.54, 64.9) * mm, v(-262.2, 64.9) * mm, v(-262.74, 65.2) * mm]});
            skFitSpline(sketch, "E1585", {"points": [v(-262.74, 65.2) * mm, v(-263.28, 65.52) * mm, v(-263.61, 66.1) * mm, v(-263.61, 66.72) * mm]});
            skFitSpline(sketch, "E1586", {"points": [v(-263.61, 66.72) * mm, v(-263.61, 67.35) * mm, v(-263.28, 67.92) * mm, v(-262.74, 68.24) * mm]});
            skFitSpline(sketch, "E1587", {"points": [v(-262.74, 68.24) * mm, v(-262.2, 68.55) * mm, v(-261.54, 68.55) * mm, v(-261, 68.24) * mm]});
            skFitSpline(sketch, "E1588", {"points": [v(-261, 68.24) * mm, v(-260.46, 67.92) * mm, v(-260.12, 67.35) * mm, v(-260.13, 66.72) * mm]});
            skFitSpline(sketch, "E1589", {"points": [v(-196.83, 66.72) * mm, v(-196.82, 66.1) * mm, v(-197.16, 65.52) * mm, v(-197.7, 65.2) * mm]});
            skFitSpline(sketch, "E1590", {"points": [v(-197.7, 65.2) * mm, v(-198.24, 64.9) * mm, v(-198.9, 64.9) * mm, v(-199.44, 65.2) * mm]});
            skFitSpline(sketch, "E1591", {"points": [v(-199.44, 65.2) * mm, v(-199.98, 65.52) * mm, v(-200.32, 66.1) * mm, v(-200.31, 66.72) * mm]});
            skFitSpline(sketch, "E1592", {"points": [v(-200.31, 66.72) * mm, v(-200.32, 67.35) * mm, v(-199.98, 67.92) * mm, v(-199.44, 68.24) * mm]});
            skFitSpline(sketch, "E1593", {"points": [v(-199.44, 68.24) * mm, v(-198.9, 68.55) * mm, v(-198.24, 68.55) * mm, v(-197.7, 68.24) * mm]});
            skFitSpline(sketch, "E1594", {"points": [v(-197.7, 68.24) * mm, v(-197.16, 67.92) * mm, v(-196.82, 67.35) * mm, v(-196.83, 66.72) * mm]});
            skFitSpline(sketch, "E1595", {"points": [v(-133.53, 66.72) * mm, v(-133.52, 66.1) * mm, v(-133.86, 65.52) * mm, v(-134.4, 65.2) * mm]});
            skFitSpline(sketch, "E1596", {"points": [v(-134.4, 65.2) * mm, v(-134.94, 64.9) * mm, v(-135.6, 64.9) * mm, v(-136.14, 65.2) * mm]});
            skFitSpline(sketch, "E1597", {"points": [v(-136.14, 65.2) * mm, v(-136.68, 65.52) * mm, v(-137.02, 66.1) * mm, v(-137.01, 66.72) * mm]});
            skFitSpline(sketch, "E1598", {"points": [v(-137.01, 66.72) * mm, v(-137.02, 67.35) * mm, v(-136.68, 67.92) * mm, v(-136.14, 68.24) * mm]});
            skFitSpline(sketch, "E1599", {"points": [v(-136.14, 68.24) * mm, v(-135.6, 68.55) * mm, v(-134.94, 68.55) * mm, v(-134.4, 68.24) * mm]});
            skFitSpline(sketch, "E1600", {"points": [v(-134.4, 68.24) * mm, v(-133.86, 67.92) * mm, v(-133.52, 67.35) * mm, v(-133.53, 66.72) * mm]});
            skFitSpline(sketch, "E1601", {"points": [v(-70.23, 66.72) * mm, v(-70.22, 66.1) * mm, v(-70.56, 65.52) * mm, v(-71.1, 65.2) * mm]});
            skFitSpline(sketch, "E1602", {"points": [v(-71.1, 65.2) * mm, v(-71.64, 64.9) * mm, v(-72.3, 64.9) * mm, v(-72.84, 65.2) * mm]});
            skFitSpline(sketch, "E1603", {"points": [v(-72.84, 65.2) * mm, v(-73.38, 65.52) * mm, v(-73.72, 66.1) * mm, v(-73.71, 66.72) * mm]});
            skFitSpline(sketch, "E1604", {"points": [v(-73.71, 66.72) * mm, v(-73.72, 67.35) * mm, v(-73.38, 67.92) * mm, v(-72.84, 68.24) * mm]});
            skFitSpline(sketch, "E1605", {"points": [v(-72.84, 68.24) * mm, v(-72.3, 68.55) * mm, v(-71.64, 68.55) * mm, v(-71.1, 68.24) * mm]});
            skFitSpline(sketch, "E1606", {"points": [v(-71.1, 68.24) * mm, v(-70.56, 67.92) * mm, v(-70.22, 67.35) * mm, v(-70.23, 66.72) * mm]});
            skFitSpline(sketch, "E1607", {"points": [v(-6.93, 66.72) * mm, v(-6.92, 66.1) * mm, v(-7.26, 65.52) * mm, v(-7.8, 65.2) * mm]});
            skFitSpline(sketch, "E1608", {"points": [v(-7.8, 65.2) * mm, v(-8.34, 64.9) * mm, v(-9, 64.9) * mm, v(-9.54, 65.2) * mm]});
            skFitSpline(sketch, "E1609", {"points": [v(-9.54, 65.2) * mm, v(-10.08, 65.52) * mm, v(-10.42, 66.1) * mm, v(-10.41, 66.72) * mm]});
            skFitSpline(sketch, "E1610", {"points": [v(-10.41, 66.72) * mm, v(-10.42, 67.35) * mm, v(-10.08, 67.92) * mm, v(-9.54, 68.24) * mm]});
            skFitSpline(sketch, "E1611", {"points": [v(-9.54, 68.24) * mm, v(-9, 68.55) * mm, v(-8.34, 68.55) * mm, v(-7.8, 68.24) * mm]});
            skFitSpline(sketch, "E1612", {"points": [v(-7.8, 68.24) * mm, v(-7.26, 67.92) * mm, v(-6.92, 67.35) * mm, v(-6.93, 66.72) * mm]});
            skFitSpline(sketch, "E1613", {"points": [v(56.37, 66.72) * mm, v(56.38, 66.1) * mm, v(56.04, 65.52) * mm, v(55.5, 65.2) * mm]});
            skFitSpline(sketch, "E1614", {"points": [v(55.5, 65.2) * mm, v(54.96, 64.9) * mm, v(54.3, 64.9) * mm, v(53.76, 65.2) * mm]});
            skFitSpline(sketch, "E1615", {"points": [v(53.76, 65.2) * mm, v(53.22, 65.52) * mm, v(52.88, 66.1) * mm, v(52.89, 66.72) * mm]});
            skFitSpline(sketch, "E1616", {"points": [v(52.89, 66.72) * mm, v(52.88, 67.35) * mm, v(53.22, 67.92) * mm, v(53.76, 68.24) * mm]});
            skFitSpline(sketch, "E1617", {"points": [v(53.76, 68.24) * mm, v(54.3, 68.55) * mm, v(54.96, 68.55) * mm, v(55.5, 68.24) * mm]});
            skFitSpline(sketch, "E1618", {"points": [v(55.5, 68.24) * mm, v(56.04, 67.92) * mm, v(56.38, 67.35) * mm, v(56.37, 66.72) * mm]});
            skFitSpline(sketch, "E1619", {"points": [v(119.67, 66.72) * mm, v(119.68, 66.1) * mm, v(119.34, 65.52) * mm, v(118.8, 65.2) * mm]});
            skFitSpline(sketch, "E1620", {"points": [v(118.8, 65.2) * mm, v(118.26, 64.9) * mm, v(117.6, 64.9) * mm, v(117.06, 65.2) * mm]});
            skFitSpline(sketch, "E1621", {"points": [v(117.06, 65.2) * mm, v(116.52, 65.52) * mm, v(116.18, 66.1) * mm, v(116.19, 66.72) * mm]});
            skFitSpline(sketch, "E1622", {"points": [v(116.19, 66.72) * mm, v(116.18, 67.35) * mm, v(116.52, 67.92) * mm, v(117.06, 68.24) * mm]});
            skFitSpline(sketch, "E1623", {"points": [v(117.06, 68.24) * mm, v(117.6, 68.55) * mm, v(118.26, 68.55) * mm, v(118.8, 68.24) * mm]});
            skFitSpline(sketch, "E1624", {"points": [v(118.8, 68.24) * mm, v(119.34, 67.92) * mm, v(119.68, 67.35) * mm, v(119.67, 66.72) * mm]});
            skFitSpline(sketch, "E1625", {"points": [v(182.97, 66.72) * mm, v(182.98, 66.1) * mm, v(182.64, 65.52) * mm, v(182.1, 65.2) * mm]});
            skFitSpline(sketch, "E1626", {"points": [v(182.1, 65.2) * mm, v(181.56, 64.9) * mm, v(180.9, 64.9) * mm, v(180.36, 65.2) * mm]});
            skFitSpline(sketch, "E1627", {"points": [v(180.36, 65.2) * mm, v(179.82, 65.52) * mm, v(179.48, 66.1) * mm, v(179.49, 66.72) * mm]});
            skFitSpline(sketch, "E1628", {"points": [v(179.49, 66.72) * mm, v(179.48, 67.35) * mm, v(179.82, 67.92) * mm, v(180.36, 68.24) * mm]});
            skFitSpline(sketch, "E1629", {"points": [v(180.36, 68.24) * mm, v(180.9, 68.55) * mm, v(181.56, 68.55) * mm, v(182.1, 68.24) * mm]});
            skFitSpline(sketch, "E1630", {"points": [v(182.1, 68.24) * mm, v(182.64, 67.92) * mm, v(182.98, 67.35) * mm, v(182.97, 66.72) * mm]});
            skFitSpline(sketch, "E1631", {"points": [v(246.27, 66.72) * mm, v(246.28, 66.1) * mm, v(245.94, 65.52) * mm, v(245.4, 65.2) * mm]});
            skFitSpline(sketch, "E1632", {"points": [v(245.4, 65.2) * mm, v(244.86, 64.9) * mm, v(244.2, 64.9) * mm, v(243.66, 65.2) * mm]});
            skFitSpline(sketch, "E1633", {"points": [v(243.66, 65.2) * mm, v(243.12, 65.52) * mm, v(242.79, 66.1) * mm, v(242.79, 66.72) * mm]});
            skFitSpline(sketch, "E1634", {"points": [v(242.79, 66.72) * mm, v(242.79, 67.35) * mm, v(243.12, 67.92) * mm, v(243.66, 68.24) * mm]});
            skFitSpline(sketch, "E1635", {"points": [v(243.66, 68.24) * mm, v(244.2, 68.55) * mm, v(244.86, 68.55) * mm, v(245.4, 68.24) * mm]});
            skFitSpline(sketch, "E1636", {"points": [v(245.4, 68.24) * mm, v(245.94, 67.92) * mm, v(246.28, 67.35) * mm, v(246.27, 66.72) * mm]});
            skLineSegment(sketch, "E1637", {"start": v(313.2, -134.31) * mm, "end": v(313.2, -125.3) * mm});
            skLineSegment(sketch, "E1638", {"start": v(316.37, -134.31) * mm, "end": v(313.2, -134.31) * mm});
            skLineSegment(sketch, "E1639", {"start": v(316.37, -143.56) * mm, "end": v(316.37, -134.31) * mm});
            skLineSegment(sketch, "E1640", {"start": v(316.37, -143.56) * mm, "end": v(313.2, -143.56) * mm});
            skLineSegment(sketch, "E1641", {"start": v(313.2, -152.5) * mm, "end": v(313.2, -143.56) * mm});
            skLineSegment(sketch, "E1642", {"start": v(316.37, -152.5) * mm, "end": v(313.2, -152.5) * mm});
            skLineSegment(sketch, "E1643", {"start": v(316.37, -161.74) * mm, "end": v(316.37, -152.5) * mm});
            skLineSegment(sketch, "E1644", {"start": v(316.37, -161.74) * mm, "end": v(313.2, -161.74) * mm});
            skLineSegment(sketch, "E1645", {"start": v(313.2, -170.68) * mm, "end": v(313.2, -161.74) * mm});
            skLineSegment(sketch, "E1646", {"start": v(316.37, -170.68) * mm, "end": v(313.2, -170.68) * mm});
            skLineSegment(sketch, "E1647", {"start": v(316.37, -179.93) * mm, "end": v(316.37, -170.68) * mm});
            skLineSegment(sketch, "E1648", {"start": v(316.37, -179.93) * mm, "end": v(313.2, -179.93) * mm});
            skLineSegment(sketch, "E1649", {"start": v(313.2, -188.95) * mm, "end": v(313.2, -179.93) * mm});
            skLineSegment(sketch, "E1650", {"start": v(-445.78, -134.31) * mm, "end": v(-445.78, -125.3) * mm});
            skLineSegment(sketch, "E1651", {"start": v(-442.6, -134.31) * mm, "end": v(-445.78, -134.31) * mm});
            skLineSegment(sketch, "E1652", {"start": v(-442.6, -143.56) * mm, "end": v(-442.6, -134.31) * mm});
            skLineSegment(sketch, "E1653", {"start": v(-442.6, -143.56) * mm, "end": v(-445.78, -143.56) * mm});
            skLineSegment(sketch, "E1654", {"start": v(-445.78, -152.5) * mm, "end": v(-445.78, -143.56) * mm});
            skLineSegment(sketch, "E1655", {"start": v(-442.6, -152.5) * mm, "end": v(-445.78, -152.5) * mm});
            skLineSegment(sketch, "E1656", {"start": v(-442.6, -161.74) * mm, "end": v(-442.6, -152.5) * mm});
            skLineSegment(sketch, "E1657", {"start": v(-442.6, -161.74) * mm, "end": v(-445.78, -161.74) * mm});
            skLineSegment(sketch, "E1658", {"start": v(-445.78, -170.68) * mm, "end": v(-445.78, -161.74) * mm});
            skLineSegment(sketch, "E1659", {"start": v(-442.6, -170.68) * mm, "end": v(-445.78, -170.68) * mm});
            skLineSegment(sketch, "E1660", {"start": v(-442.6, -179.93) * mm, "end": v(-442.6, -170.68) * mm});
            skLineSegment(sketch, "E1661", {"start": v(-442.6, -179.93) * mm, "end": v(-445.78, -179.93) * mm});
            skLineSegment(sketch, "E1662", {"start": v(-445.78, -179.93) * mm, "end": v(-445.85, -185.75) * mm});
            skLineSegment(sketch, "E1663", {"start": v(-445.85, -185.75) * mm, "end": v(-442.42, -185.75) * mm});
            skLineSegment(sketch, "E1664", {"start": v(-442.42, -185.75) * mm, "end": v(-442.42, -185.83) * mm});
            skLineSegment(sketch, "E1665", {"start": v(-442.42, -185.83) * mm, "end": v(-442.42, -189.02) * mm});
            skLineSegment(sketch, "E1666", {"start": v(308.27, -125.3) * mm, "end": v(313.2, -125.3) * mm});
            skLineSegment(sketch, "E1667", {"start": v(308.27, -125.3) * mm, "end": v(308.27, -128.47) * mm});
            skLineSegment(sketch, "E1668", {"start": v(300.4, -128.47) * mm, "end": v(308.27, -128.47) * mm});
            skLineSegment(sketch, "E1669", {"start": v(300.4, -125.3) * mm, "end": v(300.4, -128.47) * mm});
            skLineSegment(sketch, "E1670", {"start": v(292.22, -125.3) * mm, "end": v(300.4, -125.3) * mm});
            skLineSegment(sketch, "E1671", {"start": v(292.22, -125.3) * mm, "end": v(292.22, -128.47) * mm});
            skLineSegment(sketch, "E1672", {"start": v(284.35, -128.47) * mm, "end": v(292.22, -128.47) * mm});
            skLineSegment(sketch, "E1673", {"start": v(284.35, -125.3) * mm, "end": v(284.35, -128.47) * mm});
            skLineSegment(sketch, "E1674", {"start": v(276.18, -125.3) * mm, "end": v(284.35, -125.3) * mm});
            skLineSegment(sketch, "E1675", {"start": v(276.18, -125.3) * mm, "end": v(276.18, -128.47) * mm});
            skLineSegment(sketch, "E1676", {"start": v(268.3, -128.47) * mm, "end": v(276.18, -128.47) * mm});
            skLineSegment(sketch, "E1677", {"start": v(268.3, -125.3) * mm, "end": v(268.3, -128.47) * mm});
            skLineSegment(sketch, "E1678", {"start": v(260.13, -125.3) * mm, "end": v(268.3, -125.3) * mm});
            skLineSegment(sketch, "E1679", {"start": v(260.13, -125.3) * mm, "end": v(260.13, -128.47) * mm});
            skLineSegment(sketch, "E1680", {"start": v(252.26, -128.47) * mm, "end": v(260.13, -128.47) * mm});
            skLineSegment(sketch, "E1681", {"start": v(252.26, -125.3) * mm, "end": v(252.26, -128.47) * mm});
            skLineSegment(sketch, "E1682", {"start": v(244.09, -125.3) * mm, "end": v(252.26, -125.3) * mm});
            skLineSegment(sketch, "E1683", {"start": v(244.09, -125.3) * mm, "end": v(244.09, -128.47) * mm});
            skLineSegment(sketch, "E1684", {"start": v(236.22, -128.47) * mm, "end": v(244.09, -128.47) * mm});
            skLineSegment(sketch, "E1685", {"start": v(236.22, -125.3) * mm, "end": v(236.22, -128.47) * mm});
            skLineSegment(sketch, "E1686", {"start": v(228.04, -125.3) * mm, "end": v(236.22, -125.3) * mm});
            skLineSegment(sketch, "E1687", {"start": v(228.04, -125.3) * mm, "end": v(228.04, -128.47) * mm});
            skLineSegment(sketch, "E1688", {"start": v(220.17, -128.47) * mm, "end": v(228.04, -128.47) * mm});
            skLineSegment(sketch, "E1689", {"start": v(220.17, -125.3) * mm, "end": v(220.17, -128.47) * mm});
            skLineSegment(sketch, "E1690", {"start": v(212, -125.3) * mm, "end": v(220.17, -125.3) * mm});
            skLineSegment(sketch, "E1691", {"start": v(212, -125.3) * mm, "end": v(212, -128.47) * mm});
            skLineSegment(sketch, "E1692", {"start": v(204.13, -128.47) * mm, "end": v(212, -128.47) * mm});
            skLineSegment(sketch, "E1693", {"start": v(204.13, -125.3) * mm, "end": v(204.13, -128.47) * mm});
            skLineSegment(sketch, "E1694", {"start": v(195.95, -125.3) * mm, "end": v(204.13, -125.3) * mm});
            skLineSegment(sketch, "E1695", {"start": v(195.95, -125.3) * mm, "end": v(195.95, -128.47) * mm});
            skLineSegment(sketch, "E1696", {"start": v(188.08, -128.47) * mm, "end": v(195.95, -128.47) * mm});
            skLineSegment(sketch, "E1697", {"start": v(188.08, -125.3) * mm, "end": v(188.08, -128.47) * mm});
            skLineSegment(sketch, "E1698", {"start": v(179.9, -125.3) * mm, "end": v(188.08, -125.3) * mm});
            skLineSegment(sketch, "E1699", {"start": v(179.9, -125.3) * mm, "end": v(179.9, -128.47) * mm});
            skLineSegment(sketch, "E1700", {"start": v(172.04, -128.47) * mm, "end": v(179.9, -128.47) * mm});
            skLineSegment(sketch, "E1701", {"start": v(172.04, -125.3) * mm, "end": v(172.04, -128.47) * mm});
            skLineSegment(sketch, "E1702", {"start": v(163.86, -125.3) * mm, "end": v(172.04, -125.3) * mm});
            skLineSegment(sketch, "E1703", {"start": v(163.86, -125.3) * mm, "end": v(163.86, -128.47) * mm});
            skLineSegment(sketch, "E1704", {"start": v(156, -128.47) * mm, "end": v(163.86, -128.47) * mm});
            skLineSegment(sketch, "E1705", {"start": v(156, -125.3) * mm, "end": v(156, -128.47) * mm});
            skLineSegment(sketch, "E1706", {"start": v(147.82, -125.3) * mm, "end": v(156, -125.3) * mm});
            skLineSegment(sketch, "E1707", {"start": v(147.82, -125.3) * mm, "end": v(147.82, -128.47) * mm});
            skLineSegment(sketch, "E1708", {"start": v(139.95, -128.47) * mm, "end": v(147.82, -128.47) * mm});
            skLineSegment(sketch, "E1709", {"start": v(139.95, -125.3) * mm, "end": v(139.95, -128.47) * mm});
            skLineSegment(sketch, "E1710", {"start": v(131.77, -125.3) * mm, "end": v(139.95, -125.3) * mm});
            skLineSegment(sketch, "E1711", {"start": v(131.77, -125.3) * mm, "end": v(131.77, -128.47) * mm});
            skLineSegment(sketch, "E1712", {"start": v(123.9, -128.47) * mm, "end": v(131.77, -128.47) * mm});
            skLineSegment(sketch, "E1713", {"start": v(123.9, -125.3) * mm, "end": v(123.9, -128.47) * mm});
            skLineSegment(sketch, "E1714", {"start": v(115.73, -125.3) * mm, "end": v(123.9, -125.3) * mm});
            skLineSegment(sketch, "E1715", {"start": v(115.73, -125.3) * mm, "end": v(115.73, -128.47) * mm});
            skLineSegment(sketch, "E1716", {"start": v(107.86, -128.47) * mm, "end": v(115.73, -128.47) * mm});
            skLineSegment(sketch, "E1717", {"start": v(107.86, -125.3) * mm, "end": v(107.86, -128.47) * mm});
            skLineSegment(sketch, "E1718", {"start": v(99.68, -125.3) * mm, "end": v(107.86, -125.3) * mm});
            skLineSegment(sketch, "E1719", {"start": v(99.68, -125.3) * mm, "end": v(99.68, -128.47) * mm});
            skLineSegment(sketch, "E1720", {"start": v(91.8, -128.47) * mm, "end": v(99.68, -128.47) * mm});
            skLineSegment(sketch, "E1721", {"start": v(91.8, -125.3) * mm, "end": v(91.8, -128.47) * mm});
            skLineSegment(sketch, "E1722", {"start": v(83.63, -125.3) * mm, "end": v(91.8, -125.3) * mm});
            skLineSegment(sketch, "E1723", {"start": v(83.63, -125.3) * mm, "end": v(83.63, -128.47) * mm});
            skLineSegment(sketch, "E1724", {"start": v(75.76, -128.47) * mm, "end": v(83.63, -128.47) * mm});
            skLineSegment(sketch, "E1725", {"start": v(75.76, -125.3) * mm, "end": v(75.76, -128.47) * mm});
            skLineSegment(sketch, "E1726", {"start": v(67.59, -125.3) * mm, "end": v(75.76, -125.3) * mm});
            skLineSegment(sketch, "E1727", {"start": v(67.59, -125.3) * mm, "end": v(67.59, -128.47) * mm});
            skLineSegment(sketch, "E1728", {"start": v(59.72, -128.47) * mm, "end": v(67.59, -128.47) * mm});
            skLineSegment(sketch, "E1729", {"start": v(59.72, -125.3) * mm, "end": v(59.72, -128.47) * mm});
            skLineSegment(sketch, "E1730", {"start": v(51.54, -125.3) * mm, "end": v(59.72, -125.3) * mm});
            skLineSegment(sketch, "E1731", {"start": v(51.54, -125.3) * mm, "end": v(51.54, -128.47) * mm});
            skLineSegment(sketch, "E1732", {"start": v(43.67, -128.47) * mm, "end": v(51.54, -128.47) * mm});
            skLineSegment(sketch, "E1733", {"start": v(43.67, -125.3) * mm, "end": v(43.67, -128.47) * mm});
            skLineSegment(sketch, "E1734", {"start": v(35.5, -125.3) * mm, "end": v(43.67, -125.3) * mm});
            skLineSegment(sketch, "E1735", {"start": v(35.5, -125.3) * mm, "end": v(35.5, -128.47) * mm});
            skLineSegment(sketch, "E1736", {"start": v(27.63, -128.47) * mm, "end": v(35.5, -128.47) * mm});
            skLineSegment(sketch, "E1737", {"start": v(27.63, -125.3) * mm, "end": v(27.63, -128.47) * mm});
            skLineSegment(sketch, "E1738", {"start": v(19.45, -125.3) * mm, "end": v(27.63, -125.3) * mm});
            skLineSegment(sketch, "E1739", {"start": v(19.45, -125.3) * mm, "end": v(19.45, -128.47) * mm});
            skLineSegment(sketch, "E1740", {"start": v(11.58, -128.47) * mm, "end": v(19.45, -128.47) * mm});
            skLineSegment(sketch, "E1741", {"start": v(11.58, -125.3) * mm, "end": v(11.58, -128.47) * mm});
            skLineSegment(sketch, "E1742", {"start": v(3.4, -125.3) * mm, "end": v(11.58, -125.3) * mm});
            skLineSegment(sketch, "E1743", {"start": v(3.4, -125.3) * mm, "end": v(3.4, -128.47) * mm});
            skLineSegment(sketch, "E1744", {"start": v(-4.46, -128.47) * mm, "end": v(3.4, -128.47) * mm});
            skLineSegment(sketch, "E1745", {"start": v(-4.46, -125.3) * mm, "end": v(-4.46, -128.47) * mm});
            skLineSegment(sketch, "E1746", {"start": v(-12.64, -125.3) * mm, "end": v(-4.46, -125.3) * mm});
            skLineSegment(sketch, "E1747", {"start": v(-12.64, -125.3) * mm, "end": v(-12.64, -128.47) * mm});
            skLineSegment(sketch, "E1748", {"start": v(-20.5, -128.47) * mm, "end": v(-12.64, -128.47) * mm});
            skLineSegment(sketch, "E1749", {"start": v(-20.5, -125.3) * mm, "end": v(-20.5, -128.47) * mm});
            skLineSegment(sketch, "E1750", {"start": v(-28.68, -125.3) * mm, "end": v(-20.5, -125.3) * mm});
            skLineSegment(sketch, "E1751", {"start": v(-28.68, -125.3) * mm, "end": v(-28.68, -128.47) * mm});
            skLineSegment(sketch, "E1752", {"start": v(-36.55, -128.47) * mm, "end": v(-28.68, -128.47) * mm});
            skLineSegment(sketch, "E1753", {"start": v(-36.55, -125.3) * mm, "end": v(-36.55, -128.47) * mm});
            skLineSegment(sketch, "E1754", {"start": v(-44.73, -125.3) * mm, "end": v(-36.55, -125.3) * mm});
            skLineSegment(sketch, "E1755", {"start": v(-44.73, -125.3) * mm, "end": v(-44.73, -128.47) * mm});
            skLineSegment(sketch, "E1756", {"start": v(-52.6, -128.47) * mm, "end": v(-44.73, -128.47) * mm});
            skLineSegment(sketch, "E1757", {"start": v(-52.6, -125.3) * mm, "end": v(-52.6, -128.47) * mm});
            skLineSegment(sketch, "E1758", {"start": v(-60.77, -125.3) * mm, "end": v(-52.6, -125.3) * mm});
            skLineSegment(sketch, "E1759", {"start": v(-60.77, -125.3) * mm, "end": v(-60.77, -128.47) * mm});
            skLineSegment(sketch, "E1760", {"start": v(-68.64, -128.47) * mm, "end": v(-60.77, -128.47) * mm});
            skLineSegment(sketch, "E1761", {"start": v(-68.64, -125.3) * mm, "end": v(-68.64, -128.47) * mm});
            skLineSegment(sketch, "E1762", {"start": v(-76.82, -125.3) * mm, "end": v(-68.64, -125.3) * mm});
            skLineSegment(sketch, "E1763", {"start": v(-76.82, -125.3) * mm, "end": v(-76.82, -128.47) * mm});
            skLineSegment(sketch, "E1764", {"start": v(-84.69, -128.47) * mm, "end": v(-76.82, -128.47) * mm});
            skLineSegment(sketch, "E1765", {"start": v(-84.69, -125.3) * mm, "end": v(-84.69, -128.47) * mm});
            skLineSegment(sketch, "E1766", {"start": v(-92.86, -125.3) * mm, "end": v(-84.69, -125.3) * mm});
            skLineSegment(sketch, "E1767", {"start": v(-92.86, -125.3) * mm, "end": v(-92.86, -128.47) * mm});
            skLineSegment(sketch, "E1768", {"start": v(-100.73, -128.47) * mm, "end": v(-92.86, -128.47) * mm});
            skLineSegment(sketch, "E1769", {"start": v(-100.73, -125.3) * mm, "end": v(-100.73, -128.47) * mm});
            skLineSegment(sketch, "E1770", {"start": v(-108.9, -125.3) * mm, "end": v(-100.73, -125.3) * mm});
            skLineSegment(sketch, "E1771", {"start": v(-108.9, -125.3) * mm, "end": v(-108.9, -128.47) * mm});
            skLineSegment(sketch, "E1772", {"start": v(-116.78, -128.47) * mm, "end": v(-108.9, -128.47) * mm});
            skLineSegment(sketch, "E1773", {"start": v(-116.78, -125.3) * mm, "end": v(-116.78, -128.47) * mm});
            skLineSegment(sketch, "E1774", {"start": v(-124.95, -125.3) * mm, "end": v(-116.78, -125.3) * mm});
            skLineSegment(sketch, "E1775", {"start": v(-124.95, -125.3) * mm, "end": v(-124.95, -128.47) * mm});
            skLineSegment(sketch, "E1776", {"start": v(-132.82, -128.47) * mm, "end": v(-124.95, -128.47) * mm});
            skLineSegment(sketch, "E1777", {"start": v(-132.82, -125.3) * mm, "end": v(-132.82, -128.47) * mm});
            skLineSegment(sketch, "E1778", {"start": v(-141, -125.3) * mm, "end": v(-132.82, -125.3) * mm});
            skLineSegment(sketch, "E1779", {"start": v(-141, -125.3) * mm, "end": v(-141, -128.47) * mm});
            skLineSegment(sketch, "E1780", {"start": v(-148.87, -128.47) * mm, "end": v(-141, -128.47) * mm});
            skLineSegment(sketch, "E1781", {"start": v(-148.87, -125.3) * mm, "end": v(-148.87, -128.47) * mm});
            skLineSegment(sketch, "E1782", {"start": v(-157.05, -125.3) * mm, "end": v(-148.87, -125.3) * mm});
            skLineSegment(sketch, "E1783", {"start": v(-157.05, -125.3) * mm, "end": v(-157.05, -128.47) * mm});
            skLineSegment(sketch, "E1784", {"start": v(-164.92, -128.47) * mm, "end": v(-157.05, -128.47) * mm});
            skLineSegment(sketch, "E1785", {"start": v(-164.92, -125.3) * mm, "end": v(-164.92, -128.47) * mm});
            skLineSegment(sketch, "E1786", {"start": v(-173.1, -125.3) * mm, "end": v(-164.92, -125.3) * mm});
            skLineSegment(sketch, "E1787", {"start": v(-173.1, -125.3) * mm, "end": v(-173.1, -128.47) * mm});
            skLineSegment(sketch, "E1788", {"start": v(-180.96, -128.47) * mm, "end": v(-173.1, -128.47) * mm});
            skLineSegment(sketch, "E1789", {"start": v(-180.96, -125.3) * mm, "end": v(-180.96, -128.47) * mm});
            skLineSegment(sketch, "E1790", {"start": v(-189.14, -125.3) * mm, "end": v(-180.96, -125.3) * mm});
            skLineSegment(sketch, "E1791", {"start": v(-189.14, -125.3) * mm, "end": v(-189.14, -128.47) * mm});
            skLineSegment(sketch, "E1792", {"start": v(-197, -128.47) * mm, "end": v(-189.14, -128.47) * mm});
            skLineSegment(sketch, "E1793", {"start": v(-197, -125.3) * mm, "end": v(-197, -128.47) * mm});
            skLineSegment(sketch, "E1794", {"start": v(-205.18, -125.3) * mm, "end": v(-197, -125.3) * mm});
            skLineSegment(sketch, "E1795", {"start": v(-205.18, -125.3) * mm, "end": v(-205.18, -128.47) * mm});
            skLineSegment(sketch, "E1796", {"start": v(-213.05, -128.47) * mm, "end": v(-205.18, -128.47) * mm});
            skLineSegment(sketch, "E1797", {"start": v(-213.05, -125.3) * mm, "end": v(-213.05, -128.47) * mm});
            skLineSegment(sketch, "E1798", {"start": v(-221.23, -125.3) * mm, "end": v(-213.05, -125.3) * mm});
            skLineSegment(sketch, "E1799", {"start": v(-221.23, -125.3) * mm, "end": v(-221.23, -128.47) * mm});
            skLineSegment(sketch, "E1800", {"start": v(-229.1, -128.47) * mm, "end": v(-221.23, -128.47) * mm});
            skLineSegment(sketch, "E1801", {"start": v(-229.1, -125.3) * mm, "end": v(-229.1, -128.47) * mm});
            skLineSegment(sketch, "E1802", {"start": v(-237.27, -125.3) * mm, "end": v(-229.1, -125.3) * mm});
            skLineSegment(sketch, "E1803", {"start": v(-237.27, -125.3) * mm, "end": v(-237.27, -128.47) * mm});
            skLineSegment(sketch, "E1804", {"start": v(-245.14, -128.47) * mm, "end": v(-237.27, -128.47) * mm});
            skLineSegment(sketch, "E1805", {"start": v(-245.14, -125.3) * mm, "end": v(-245.14, -128.47) * mm});
            skLineSegment(sketch, "E1806", {"start": v(-253.32, -125.3) * mm, "end": v(-245.14, -125.3) * mm});
            skLineSegment(sketch, "E1807", {"start": v(-253.32, -125.3) * mm, "end": v(-253.32, -128.47) * mm});
            skLineSegment(sketch, "E1808", {"start": v(-261.19, -128.47) * mm, "end": v(-253.32, -128.47) * mm});
            skLineSegment(sketch, "E1809", {"start": v(-261.19, -125.3) * mm, "end": v(-261.19, -128.47) * mm});
            skLineSegment(sketch, "E1810", {"start": v(-269.36, -125.3) * mm, "end": v(-261.19, -125.3) * mm});
            skLineSegment(sketch, "E1811", {"start": v(-269.36, -125.3) * mm, "end": v(-269.36, -128.47) * mm});
            skLineSegment(sketch, "E1812", {"start": v(-277.23, -128.47) * mm, "end": v(-269.36, -128.47) * mm});
            skLineSegment(sketch, "E1813", {"start": v(-277.23, -125.3) * mm, "end": v(-277.23, -128.47) * mm});
            skLineSegment(sketch, "E1814", {"start": v(-285.4, -125.3) * mm, "end": v(-277.23, -125.3) * mm});
            skLineSegment(sketch, "E1815", {"start": v(-285.4, -125.3) * mm, "end": v(-285.4, -128.47) * mm});
            skLineSegment(sketch, "E1816", {"start": v(-293.28, -128.47) * mm, "end": v(-285.4, -128.47) * mm});
            skLineSegment(sketch, "E1817", {"start": v(-293.28, -125.3) * mm, "end": v(-293.28, -128.47) * mm});
            skLineSegment(sketch, "E1818", {"start": v(-301.45, -125.3) * mm, "end": v(-293.28, -125.3) * mm});
            skLineSegment(sketch, "E1819", {"start": v(-301.45, -125.3) * mm, "end": v(-301.45, -128.47) * mm});
            skLineSegment(sketch, "E1820", {"start": v(-309.32, -128.47) * mm, "end": v(-301.45, -128.47) * mm});
            skLineSegment(sketch, "E1821", {"start": v(-309.32, -125.3) * mm, "end": v(-309.32, -128.47) * mm});
            skLineSegment(sketch, "E1822", {"start": v(-317.5, -125.3) * mm, "end": v(-309.32, -125.3) * mm});
            skLineSegment(sketch, "E1823", {"start": v(-317.5, -125.3) * mm, "end": v(-317.5, -128.47) * mm});
            skLineSegment(sketch, "E1824", {"start": v(-325.37, -128.47) * mm, "end": v(-317.5, -128.47) * mm});
            skLineSegment(sketch, "E1825", {"start": v(-325.37, -125.3) * mm, "end": v(-325.37, -128.47) * mm});
            skLineSegment(sketch, "E1826", {"start": v(-333.54, -125.3) * mm, "end": v(-325.37, -125.3) * mm});
            skLineSegment(sketch, "E1827", {"start": v(-333.54, -125.3) * mm, "end": v(-333.54, -128.47) * mm});
            skLineSegment(sketch, "E1828", {"start": v(-341.41, -128.47) * mm, "end": v(-333.54, -128.47) * mm});
            skLineSegment(sketch, "E1829", {"start": v(-341.41, -125.3) * mm, "end": v(-341.41, -128.47) * mm});
            skLineSegment(sketch, "E1830", {"start": v(-349.59, -125.3) * mm, "end": v(-341.41, -125.3) * mm});
            skLineSegment(sketch, "E1831", {"start": v(-349.59, -125.3) * mm, "end": v(-349.59, -128.47) * mm});
            skLineSegment(sketch, "E1832", {"start": v(-357.46, -128.47) * mm, "end": v(-349.59, -128.47) * mm});
            skLineSegment(sketch, "E1833", {"start": v(-357.46, -125.3) * mm, "end": v(-357.46, -128.47) * mm});
            skLineSegment(sketch, "E1834", {"start": v(-365.63, -125.3) * mm, "end": v(-357.46, -125.3) * mm});
            skLineSegment(sketch, "E1835", {"start": v(-365.63, -125.3) * mm, "end": v(-365.63, -128.47) * mm});
            skLineSegment(sketch, "E1836", {"start": v(-373.5, -128.47) * mm, "end": v(-365.63, -128.47) * mm});
            skLineSegment(sketch, "E1837", {"start": v(-373.5, -125.3) * mm, "end": v(-373.5, -128.47) * mm});
            skLineSegment(sketch, "E1838", {"start": v(-381.68, -125.3) * mm, "end": v(-373.5, -125.3) * mm});
            skLineSegment(sketch, "E1839", {"start": v(-381.68, -125.3) * mm, "end": v(-381.68, -128.47) * mm});
            skLineSegment(sketch, "E1840", {"start": v(-389.55, -128.47) * mm, "end": v(-381.68, -128.47) * mm});
            skLineSegment(sketch, "E1841", {"start": v(-389.55, -125.3) * mm, "end": v(-389.55, -128.47) * mm});
            skLineSegment(sketch, "E1842", {"start": v(-397.72, -125.3) * mm, "end": v(-389.55, -125.3) * mm});
            skLineSegment(sketch, "E1843", {"start": v(-397.72, -125.3) * mm, "end": v(-397.72, -128.47) * mm});
            skLineSegment(sketch, "E1844", {"start": v(-405.6, -128.47) * mm, "end": v(-397.72, -128.47) * mm});
            skLineSegment(sketch, "E1845", {"start": v(-405.6, -125.3) * mm, "end": v(-405.6, -128.47) * mm});
            skLineSegment(sketch, "E1846", {"start": v(-413.77, -125.3) * mm, "end": v(-405.6, -125.3) * mm});
            skLineSegment(sketch, "E1847", {"start": v(-413.77, -125.3) * mm, "end": v(-413.77, -128.47) * mm});
            skLineSegment(sketch, "E1848", {"start": v(-421.64, -128.47) * mm, "end": v(-413.77, -128.47) * mm});
            skLineSegment(sketch, "E1849", {"start": v(-421.64, -125.3) * mm, "end": v(-421.64, -128.47) * mm});
            skLineSegment(sketch, "E1850", {"start": v(-429.82, -125.3) * mm, "end": v(-421.64, -125.3) * mm});
            skLineSegment(sketch, "E1851", {"start": v(-429.82, -125.3) * mm, "end": v(-429.82, -128.47) * mm});
            skLineSegment(sketch, "E1852", {"start": v(-437.69, -128.47) * mm, "end": v(-429.82, -128.47) * mm});
            skLineSegment(sketch, "E1853", {"start": v(-437.69, -125.3) * mm, "end": v(-437.69, -128.47) * mm});
            skLineSegment(sketch, "E1854", {"start": v(-445.78, -125.3) * mm, "end": v(-437.69, -125.3) * mm});
            skLineSegment(sketch, "E1855", {"start": v(308.27, -188.95) * mm, "end": v(313.2, -188.95) * mm});
            skLineSegment(sketch, "E1856", {"start": v(308.27, -185.77) * mm, "end": v(308.27, -188.95) * mm});
            skLineSegment(sketch, "E1857", {"start": v(300.4, -185.77) * mm, "end": v(308.27, -185.77) * mm});
            skLineSegment(sketch, "E1858", {"start": v(300.4, -185.77) * mm, "end": v(300.4, -188.95) * mm});
            skLineSegment(sketch, "E1859", {"start": v(292.22, -188.95) * mm, "end": v(300.4, -188.95) * mm});
            skLineSegment(sketch, "E1860", {"start": v(292.22, -185.77) * mm, "end": v(292.22, -188.95) * mm});
            skLineSegment(sketch, "E1861", {"start": v(284.35, -185.77) * mm, "end": v(292.22, -185.77) * mm});
            skLineSegment(sketch, "E1862", {"start": v(284.35, -185.77) * mm, "end": v(284.35, -188.95) * mm});
            skLineSegment(sketch, "E1863", {"start": v(276.18, -188.95) * mm, "end": v(284.35, -188.95) * mm});
            skLineSegment(sketch, "E1864", {"start": v(276.18, -185.77) * mm, "end": v(276.18, -188.95) * mm});
            skLineSegment(sketch, "E1865", {"start": v(268.3, -185.77) * mm, "end": v(276.18, -185.77) * mm});
            skLineSegment(sketch, "E1866", {"start": v(268.3, -185.77) * mm, "end": v(268.3, -188.95) * mm});
            skLineSegment(sketch, "E1867", {"start": v(260.13, -188.95) * mm, "end": v(268.3, -188.95) * mm});
            skLineSegment(sketch, "E1868", {"start": v(260.13, -185.77) * mm, "end": v(260.13, -188.95) * mm});
            skLineSegment(sketch, "E1869", {"start": v(252.26, -185.77) * mm, "end": v(260.13, -185.77) * mm});
            skLineSegment(sketch, "E1870", {"start": v(252.26, -185.77) * mm, "end": v(252.26, -188.95) * mm});
            skLineSegment(sketch, "E1871", {"start": v(244.09, -188.95) * mm, "end": v(252.26, -188.95) * mm});
            skLineSegment(sketch, "E1872", {"start": v(244.09, -185.77) * mm, "end": v(244.09, -188.95) * mm});
            skLineSegment(sketch, "E1873", {"start": v(236.22, -185.77) * mm, "end": v(244.09, -185.77) * mm});
            skLineSegment(sketch, "E1874", {"start": v(236.22, -185.77) * mm, "end": v(236.22, -188.95) * mm});
            skLineSegment(sketch, "E1875", {"start": v(228.04, -188.95) * mm, "end": v(236.22, -188.95) * mm});
            skLineSegment(sketch, "E1876", {"start": v(228.04, -185.77) * mm, "end": v(228.04, -188.95) * mm});
            skLineSegment(sketch, "E1877", {"start": v(220.17, -185.77) * mm, "end": v(228.04, -185.77) * mm});
            skLineSegment(sketch, "E1878", {"start": v(220.17, -185.77) * mm, "end": v(220.17, -188.95) * mm});
            skLineSegment(sketch, "E1879", {"start": v(212, -188.95) * mm, "end": v(220.17, -188.95) * mm});
            skLineSegment(sketch, "E1880", {"start": v(212, -185.77) * mm, "end": v(212, -188.95) * mm});
            skLineSegment(sketch, "E1881", {"start": v(204.13, -185.77) * mm, "end": v(212, -185.77) * mm});
            skLineSegment(sketch, "E1882", {"start": v(204.13, -185.77) * mm, "end": v(204.13, -188.95) * mm});
            skLineSegment(sketch, "E1883", {"start": v(195.95, -188.95) * mm, "end": v(204.13, -188.95) * mm});
            skLineSegment(sketch, "E1884", {"start": v(195.95, -185.77) * mm, "end": v(195.95, -188.95) * mm});
            skLineSegment(sketch, "E1885", {"start": v(188.08, -185.77) * mm, "end": v(195.95, -185.77) * mm});
            skLineSegment(sketch, "E1886", {"start": v(188.08, -185.77) * mm, "end": v(188.08, -188.95) * mm});
            skLineSegment(sketch, "E1887", {"start": v(179.9, -188.95) * mm, "end": v(188.08, -188.95) * mm});
            skLineSegment(sketch, "E1888", {"start": v(179.9, -185.77) * mm, "end": v(179.9, -188.95) * mm});
            skLineSegment(sketch, "E1889", {"start": v(172.04, -185.77) * mm, "end": v(179.9, -185.77) * mm});
            skLineSegment(sketch, "E1890", {"start": v(172.04, -185.77) * mm, "end": v(172.04, -188.95) * mm});
            skLineSegment(sketch, "E1891", {"start": v(163.86, -188.95) * mm, "end": v(172.04, -188.95) * mm});
            skLineSegment(sketch, "E1892", {"start": v(163.86, -185.77) * mm, "end": v(163.86, -188.95) * mm});
            skLineSegment(sketch, "E1893", {"start": v(156, -185.77) * mm, "end": v(163.86, -185.77) * mm});
            skLineSegment(sketch, "E1894", {"start": v(156, -185.77) * mm, "end": v(156, -188.95) * mm});
            skLineSegment(sketch, "E1895", {"start": v(147.82, -188.95) * mm, "end": v(156, -188.95) * mm});
            skLineSegment(sketch, "E1896", {"start": v(147.82, -185.77) * mm, "end": v(147.82, -188.95) * mm});
            skLineSegment(sketch, "E1897", {"start": v(139.95, -185.77) * mm, "end": v(147.82, -185.77) * mm});
            skLineSegment(sketch, "E1898", {"start": v(139.95, -185.77) * mm, "end": v(139.95, -188.95) * mm});
            skLineSegment(sketch, "E1899", {"start": v(131.77, -188.95) * mm, "end": v(139.95, -188.95) * mm});
            skLineSegment(sketch, "E1900", {"start": v(131.77, -185.77) * mm, "end": v(131.77, -188.95) * mm});
            skLineSegment(sketch, "E1901", {"start": v(123.9, -185.77) * mm, "end": v(131.77, -185.77) * mm});
            skLineSegment(sketch, "E1902", {"start": v(123.9, -185.77) * mm, "end": v(123.9, -188.95) * mm});
            skLineSegment(sketch, "E1903", {"start": v(115.73, -188.95) * mm, "end": v(123.9, -188.95) * mm});
            skLineSegment(sketch, "E1904", {"start": v(115.73, -185.77) * mm, "end": v(115.73, -188.95) * mm});
            skLineSegment(sketch, "E1905", {"start": v(107.86, -185.77) * mm, "end": v(115.73, -185.77) * mm});
            skLineSegment(sketch, "E1906", {"start": v(107.86, -185.77) * mm, "end": v(107.86, -188.95) * mm});
            skLineSegment(sketch, "E1907", {"start": v(99.68, -188.95) * mm, "end": v(107.86, -188.95) * mm});
            skLineSegment(sketch, "E1908", {"start": v(99.68, -185.77) * mm, "end": v(99.68, -188.95) * mm});
            skLineSegment(sketch, "E1909", {"start": v(91.8, -185.77) * mm, "end": v(99.68, -185.77) * mm});
            skLineSegment(sketch, "E1910", {"start": v(91.8, -185.77) * mm, "end": v(91.8, -188.95) * mm});
            skLineSegment(sketch, "E1911", {"start": v(83.63, -188.95) * mm, "end": v(91.8, -188.95) * mm});
            skLineSegment(sketch, "E1912", {"start": v(83.63, -185.77) * mm, "end": v(83.63, -188.95) * mm});
            skLineSegment(sketch, "E1913", {"start": v(75.76, -185.77) * mm, "end": v(83.63, -185.77) * mm});
            skLineSegment(sketch, "E1914", {"start": v(75.76, -185.77) * mm, "end": v(75.76, -188.95) * mm});
            skLineSegment(sketch, "E1915", {"start": v(67.59, -188.95) * mm, "end": v(75.76, -188.95) * mm});
            skLineSegment(sketch, "E1916", {"start": v(67.59, -185.77) * mm, "end": v(67.59, -188.95) * mm});
            skLineSegment(sketch, "E1917", {"start": v(59.72, -185.77) * mm, "end": v(67.59, -185.77) * mm});
            skLineSegment(sketch, "E1918", {"start": v(59.72, -185.77) * mm, "end": v(59.72, -188.95) * mm});
            skLineSegment(sketch, "E1919", {"start": v(51.54, -188.95) * mm, "end": v(59.72, -188.95) * mm});
            skLineSegment(sketch, "E1920", {"start": v(51.54, -185.77) * mm, "end": v(51.54, -188.95) * mm});
            skLineSegment(sketch, "E1921", {"start": v(43.67, -185.77) * mm, "end": v(51.54, -185.77) * mm});
            skLineSegment(sketch, "E1922", {"start": v(43.67, -185.77) * mm, "end": v(43.67, -188.95) * mm});
            skLineSegment(sketch, "E1923", {"start": v(35.5, -188.95) * mm, "end": v(43.67, -188.95) * mm});
            skLineSegment(sketch, "E1924", {"start": v(35.5, -185.77) * mm, "end": v(35.5, -188.95) * mm});
            skLineSegment(sketch, "E1925", {"start": v(27.63, -185.77) * mm, "end": v(35.5, -185.77) * mm});
            skLineSegment(sketch, "E1926", {"start": v(27.63, -185.77) * mm, "end": v(27.63, -188.95) * mm});
            skLineSegment(sketch, "E1927", {"start": v(19.45, -188.95) * mm, "end": v(27.63, -188.95) * mm});
            skLineSegment(sketch, "E1928", {"start": v(19.45, -185.77) * mm, "end": v(19.45, -188.95) * mm});
            skLineSegment(sketch, "E1929", {"start": v(11.58, -185.77) * mm, "end": v(19.45, -185.77) * mm});
            skLineSegment(sketch, "E1930", {"start": v(11.58, -185.77) * mm, "end": v(11.58, -188.95) * mm});
            skLineSegment(sketch, "E1931", {"start": v(3.4, -188.95) * mm, "end": v(11.58, -188.95) * mm});
            skLineSegment(sketch, "E1932", {"start": v(3.4, -185.77) * mm, "end": v(3.4, -188.95) * mm});
            skLineSegment(sketch, "E1933", {"start": v(-4.46, -185.77) * mm, "end": v(3.4, -185.77) * mm});
            skLineSegment(sketch, "E1934", {"start": v(-4.46, -185.77) * mm, "end": v(-4.46, -188.95) * mm});
            skLineSegment(sketch, "E1935", {"start": v(-12.64, -188.95) * mm, "end": v(-4.46, -188.95) * mm});
            skLineSegment(sketch, "E1936", {"start": v(-12.64, -185.77) * mm, "end": v(-12.64, -188.95) * mm});
            skLineSegment(sketch, "E1937", {"start": v(-20.5, -185.77) * mm, "end": v(-12.64, -185.77) * mm});
            skLineSegment(sketch, "E1938", {"start": v(-20.5, -185.77) * mm, "end": v(-20.5, -188.95) * mm});
            skLineSegment(sketch, "E1939", {"start": v(-28.68, -188.95) * mm, "end": v(-20.5, -188.95) * mm});
            skLineSegment(sketch, "E1940", {"start": v(-28.68, -185.77) * mm, "end": v(-28.68, -188.95) * mm});
            skLineSegment(sketch, "E1941", {"start": v(-36.55, -185.77) * mm, "end": v(-28.68, -185.77) * mm});
            skLineSegment(sketch, "E1942", {"start": v(-36.55, -185.77) * mm, "end": v(-36.55, -188.95) * mm});
            skLineSegment(sketch, "E1943", {"start": v(-44.73, -188.95) * mm, "end": v(-36.55, -188.95) * mm});
            skLineSegment(sketch, "E1944", {"start": v(-44.73, -185.77) * mm, "end": v(-44.73, -188.95) * mm});
            skLineSegment(sketch, "E1945", {"start": v(-52.6, -185.77) * mm, "end": v(-44.73, -185.77) * mm});
            skLineSegment(sketch, "E1946", {"start": v(-52.6, -185.77) * mm, "end": v(-52.6, -188.95) * mm});
            skLineSegment(sketch, "E1947", {"start": v(-60.77, -188.95) * mm, "end": v(-52.6, -188.95) * mm});
            skLineSegment(sketch, "E1948", {"start": v(-60.77, -185.77) * mm, "end": v(-60.77, -188.95) * mm});
            skLineSegment(sketch, "E1949", {"start": v(-68.64, -185.77) * mm, "end": v(-60.77, -185.77) * mm});
            skLineSegment(sketch, "E1950", {"start": v(-68.64, -185.77) * mm, "end": v(-68.64, -188.95) * mm});
            skLineSegment(sketch, "E1951", {"start": v(-76.82, -188.95) * mm, "end": v(-68.64, -188.95) * mm});
            skLineSegment(sketch, "E1952", {"start": v(-76.82, -185.77) * mm, "end": v(-76.82, -188.95) * mm});
            skLineSegment(sketch, "E1953", {"start": v(-84.69, -185.77) * mm, "end": v(-76.82, -185.77) * mm});
            skLineSegment(sketch, "E1954", {"start": v(-84.69, -185.77) * mm, "end": v(-84.69, -188.95) * mm});
            skLineSegment(sketch, "E1955", {"start": v(-92.86, -188.95) * mm, "end": v(-84.69, -188.95) * mm});
            skLineSegment(sketch, "E1956", {"start": v(-92.86, -185.77) * mm, "end": v(-92.86, -188.95) * mm});
            skLineSegment(sketch, "E1957", {"start": v(-100.73, -185.77) * mm, "end": v(-92.86, -185.77) * mm});
            skLineSegment(sketch, "E1958", {"start": v(-100.73, -185.77) * mm, "end": v(-100.73, -188.95) * mm});
            skLineSegment(sketch, "E1959", {"start": v(-108.9, -188.95) * mm, "end": v(-100.73, -188.95) * mm});
            skLineSegment(sketch, "E1960", {"start": v(-108.9, -185.77) * mm, "end": v(-108.9, -188.95) * mm});
            skLineSegment(sketch, "E1961", {"start": v(-116.78, -185.77) * mm, "end": v(-108.9, -185.77) * mm});
            skLineSegment(sketch, "E1962", {"start": v(-116.78, -185.77) * mm, "end": v(-116.78, -188.95) * mm});
            skLineSegment(sketch, "E1963", {"start": v(-124.95, -188.95) * mm, "end": v(-116.78, -188.95) * mm});
            skLineSegment(sketch, "E1964", {"start": v(-124.95, -185.77) * mm, "end": v(-124.95, -188.95) * mm});
            skLineSegment(sketch, "E1965", {"start": v(-132.82, -185.77) * mm, "end": v(-124.95, -185.77) * mm});
            skLineSegment(sketch, "E1966", {"start": v(-132.82, -185.77) * mm, "end": v(-132.82, -188.95) * mm});
            skLineSegment(sketch, "E1967", {"start": v(-141, -188.95) * mm, "end": v(-132.82, -188.95) * mm});
            skLineSegment(sketch, "E1968", {"start": v(-141, -185.77) * mm, "end": v(-141, -188.95) * mm});
            skLineSegment(sketch, "E1969", {"start": v(-148.87, -185.77) * mm, "end": v(-141, -185.77) * mm});
            skLineSegment(sketch, "E1970", {"start": v(-148.87, -185.77) * mm, "end": v(-148.87, -188.95) * mm});
            skLineSegment(sketch, "E1971", {"start": v(-157.05, -188.95) * mm, "end": v(-148.87, -188.95) * mm});
            skLineSegment(sketch, "E1972", {"start": v(-157.05, -185.77) * mm, "end": v(-157.05, -188.95) * mm});
            skLineSegment(sketch, "E1973", {"start": v(-164.92, -185.77) * mm, "end": v(-157.05, -185.77) * mm});
            skLineSegment(sketch, "E1974", {"start": v(-164.92, -185.77) * mm, "end": v(-164.92, -188.95) * mm});
            skLineSegment(sketch, "E1975", {"start": v(-173.1, -188.95) * mm, "end": v(-164.92, -188.95) * mm});
            skLineSegment(sketch, "E1976", {"start": v(-173.1, -185.77) * mm, "end": v(-173.1, -188.95) * mm});
            skLineSegment(sketch, "E1977", {"start": v(-180.96, -185.77) * mm, "end": v(-173.1, -185.77) * mm});
            skLineSegment(sketch, "E1978", {"start": v(-180.96, -185.77) * mm, "end": v(-180.96, -188.95) * mm});
            skLineSegment(sketch, "E1979", {"start": v(-189.14, -188.95) * mm, "end": v(-180.96, -188.95) * mm});
            skLineSegment(sketch, "E1980", {"start": v(-189.14, -185.77) * mm, "end": v(-189.14, -188.95) * mm});
            skLineSegment(sketch, "E1981", {"start": v(-197, -185.77) * mm, "end": v(-189.14, -185.77) * mm});
            skLineSegment(sketch, "E1982", {"start": v(-197, -185.77) * mm, "end": v(-197, -188.95) * mm});
            skLineSegment(sketch, "E1983", {"start": v(-205.18, -188.95) * mm, "end": v(-197, -188.95) * mm});
            skLineSegment(sketch, "E1984", {"start": v(-205.18, -185.77) * mm, "end": v(-205.18, -188.95) * mm});
            skLineSegment(sketch, "E1985", {"start": v(-213.05, -185.77) * mm, "end": v(-205.18, -185.77) * mm});
            skLineSegment(sketch, "E1986", {"start": v(-213.05, -185.77) * mm, "end": v(-213.05, -188.95) * mm});
            skLineSegment(sketch, "E1987", {"start": v(-221.23, -188.95) * mm, "end": v(-213.05, -188.95) * mm});
            skLineSegment(sketch, "E1988", {"start": v(-221.23, -185.77) * mm, "end": v(-221.23, -188.95) * mm});
            skLineSegment(sketch, "E1989", {"start": v(-229.1, -185.77) * mm, "end": v(-221.23, -185.77) * mm});
            skLineSegment(sketch, "E1990", {"start": v(-229.1, -185.77) * mm, "end": v(-229.1, -188.95) * mm});
            skLineSegment(sketch, "E1991", {"start": v(-237.27, -188.95) * mm, "end": v(-229.1, -188.95) * mm});
            skLineSegment(sketch, "E1992", {"start": v(-237.27, -185.77) * mm, "end": v(-237.27, -188.95) * mm});
            skLineSegment(sketch, "E1993", {"start": v(-245.14, -185.77) * mm, "end": v(-237.27, -185.77) * mm});
            skLineSegment(sketch, "E1994", {"start": v(-245.14, -185.77) * mm, "end": v(-245.14, -188.95) * mm});
            skLineSegment(sketch, "E1995", {"start": v(-253.32, -188.95) * mm, "end": v(-245.14, -188.95) * mm});
            skLineSegment(sketch, "E1996", {"start": v(-253.32, -185.77) * mm, "end": v(-253.32, -188.95) * mm});
            skLineSegment(sketch, "E1997", {"start": v(-261.19, -185.77) * mm, "end": v(-253.32, -185.77) * mm});
            skLineSegment(sketch, "E1998", {"start": v(-261.19, -185.77) * mm, "end": v(-261.19, -188.95) * mm});
            skLineSegment(sketch, "E1999", {"start": v(-269.36, -188.95) * mm, "end": v(-261.19, -188.95) * mm});
            skLineSegment(sketch, "E2000", {"start": v(-269.36, -185.77) * mm, "end": v(-269.36, -188.95) * mm});
            skLineSegment(sketch, "E2001", {"start": v(-277.23, -185.77) * mm, "end": v(-269.36, -185.77) * mm});
            skLineSegment(sketch, "E2002", {"start": v(-277.23, -185.77) * mm, "end": v(-277.23, -188.95) * mm});
            skLineSegment(sketch, "E2003", {"start": v(-285.4, -188.95) * mm, "end": v(-277.23, -188.95) * mm});
            skLineSegment(sketch, "E2004", {"start": v(-285.4, -185.77) * mm, "end": v(-285.4, -188.95) * mm});
            skLineSegment(sketch, "E2005", {"start": v(-293.28, -185.77) * mm, "end": v(-285.4, -185.77) * mm});
            skLineSegment(sketch, "E2006", {"start": v(-293.28, -185.77) * mm, "end": v(-293.28, -188.95) * mm});
            skLineSegment(sketch, "E2007", {"start": v(-301.45, -188.95) * mm, "end": v(-293.28, -188.95) * mm});
            skLineSegment(sketch, "E2008", {"start": v(-301.45, -185.77) * mm, "end": v(-301.45, -188.95) * mm});
            skLineSegment(sketch, "E2009", {"start": v(-309.32, -185.77) * mm, "end": v(-301.45, -185.77) * mm});
            skLineSegment(sketch, "E2010", {"start": v(-309.32, -185.77) * mm, "end": v(-309.32, -188.95) * mm});
            skLineSegment(sketch, "E2011", {"start": v(-317.5, -188.95) * mm, "end": v(-309.32, -188.95) * mm});
            skLineSegment(sketch, "E2012", {"start": v(-317.5, -185.77) * mm, "end": v(-317.5, -188.95) * mm});
            skLineSegment(sketch, "E2013", {"start": v(-325.37, -185.77) * mm, "end": v(-317.5, -185.77) * mm});
            skLineSegment(sketch, "E2014", {"start": v(-325.37, -185.77) * mm, "end": v(-325.37, -188.95) * mm});
            skLineSegment(sketch, "E2015", {"start": v(-333.54, -188.95) * mm, "end": v(-325.37, -188.95) * mm});
            skLineSegment(sketch, "E2016", {"start": v(-333.54, -185.77) * mm, "end": v(-333.54, -188.95) * mm});
            skLineSegment(sketch, "E2017", {"start": v(-341.41, -185.77) * mm, "end": v(-333.54, -185.77) * mm});
            skLineSegment(sketch, "E2018", {"start": v(-341.41, -185.77) * mm, "end": v(-341.41, -188.95) * mm});
            skLineSegment(sketch, "E2019", {"start": v(-349.59, -188.95) * mm, "end": v(-341.41, -188.95) * mm});
            skLineSegment(sketch, "E2020", {"start": v(-349.59, -185.77) * mm, "end": v(-349.59, -188.95) * mm});
            skLineSegment(sketch, "E2021", {"start": v(-357.46, -185.77) * mm, "end": v(-349.59, -185.77) * mm});
            skLineSegment(sketch, "E2022", {"start": v(-357.46, -185.77) * mm, "end": v(-357.46, -188.95) * mm});
            skLineSegment(sketch, "E2023", {"start": v(-365.63, -188.95) * mm, "end": v(-357.46, -188.95) * mm});
            skLineSegment(sketch, "E2024", {"start": v(-365.63, -185.77) * mm, "end": v(-365.63, -188.95) * mm});
            skLineSegment(sketch, "E2025", {"start": v(-373.5, -185.77) * mm, "end": v(-365.63, -185.77) * mm});
            skLineSegment(sketch, "E2026", {"start": v(-373.5, -185.77) * mm, "end": v(-373.5, -188.95) * mm});
            skLineSegment(sketch, "E2027", {"start": v(-381.68, -188.95) * mm, "end": v(-373.5, -188.95) * mm});
            skLineSegment(sketch, "E2028", {"start": v(-381.68, -185.77) * mm, "end": v(-381.68, -188.95) * mm});
            skLineSegment(sketch, "E2029", {"start": v(-389.55, -185.77) * mm, "end": v(-381.68, -185.77) * mm});
            skLineSegment(sketch, "E2030", {"start": v(-389.55, -185.77) * mm, "end": v(-389.55, -188.95) * mm});
            skLineSegment(sketch, "E2031", {"start": v(-397.72, -188.95) * mm, "end": v(-389.55, -188.95) * mm});
            skLineSegment(sketch, "E2032", {"start": v(-397.72, -185.77) * mm, "end": v(-397.72, -188.95) * mm});
            skLineSegment(sketch, "E2033", {"start": v(-405.6, -185.77) * mm, "end": v(-397.72, -185.77) * mm});
            skLineSegment(sketch, "E2034", {"start": v(-405.6, -185.77) * mm, "end": v(-405.6, -188.95) * mm});
            skLineSegment(sketch, "E2035", {"start": v(-413.77, -188.95) * mm, "end": v(-405.6, -188.95) * mm});
            skLineSegment(sketch, "E2036", {"start": v(-413.77, -185.77) * mm, "end": v(-413.77, -188.95) * mm});
            skLineSegment(sketch, "E2037", {"start": v(-421.64, -185.77) * mm, "end": v(-413.77, -185.77) * mm});
            skLineSegment(sketch, "E2038", {"start": v(-421.64, -185.77) * mm, "end": v(-421.64, -188.95) * mm});
            skLineSegment(sketch, "E2039", {"start": v(-429.82, -188.95) * mm, "end": v(-421.64, -188.95) * mm});
            skLineSegment(sketch, "E2040", {"start": v(-429.82, -185.77) * mm, "end": v(-429.82, -188.95) * mm});
            skLineSegment(sketch, "E2041", {"start": v(-437.69, -185.77) * mm, "end": v(-429.82, -185.77) * mm});
            skLineSegment(sketch, "E2042", {"start": v(-437.69, -185.77) * mm, "end": v(-437.69, -188.95) * mm});
            skFitSpline(sketch, "E2043", {"points": [v(-386.16, -136.48) * mm, v(-386.16, -137.1) * mm, v(-386.5, -137.68) * mm, v(-387.03, -138) * mm]});
            skFitSpline(sketch, "E2044", {"points": [v(-387.03, -138) * mm, v(-387.57, -138.3) * mm, v(-388.24, -138.3) * mm, v(-388.78, -138) * mm]});
            skFitSpline(sketch, "E2045", {"points": [v(-388.78, -138) * mm, v(-389.32, -137.68) * mm, v(-389.65, -137.1) * mm, v(-389.65, -136.48) * mm]});
            skFitSpline(sketch, "E2046", {"points": [v(-389.65, -136.48) * mm, v(-389.65, -135.85) * mm, v(-389.32, -135.28) * mm, v(-388.78, -134.96) * mm]});
            skFitSpline(sketch, "E2047", {"points": [v(-388.78, -134.96) * mm, v(-388.24, -134.65) * mm, v(-387.57, -134.65) * mm, v(-387.03, -134.96) * mm]});
            skFitSpline(sketch, "E2048", {"points": [v(-387.03, -134.96) * mm, v(-386.5, -135.28) * mm, v(-386.16, -135.85) * mm, v(-386.16, -136.48) * mm]});
            skLineSegment(sketch, "E2049", {"start": v(-442.46, -188.95) * mm, "end": v(-437.69, -188.95) * mm});
            skFitSpline(sketch, "E2050", {"points": [v(-322.86, -136.48) * mm, v(-322.86, -137.1) * mm, v(-323.2, -137.68) * mm, v(-323.73, -138) * mm]});
            skFitSpline(sketch, "E2051", {"points": [v(-323.73, -138) * mm, v(-324.27, -138.3) * mm, v(-324.94, -138.3) * mm, v(-325.48, -138) * mm]});
            skFitSpline(sketch, "E2052", {"points": [v(-325.48, -138) * mm, v(-326.02, -137.68) * mm, v(-326.35, -137.1) * mm, v(-326.35, -136.48) * mm]});
            skFitSpline(sketch, "E2053", {"points": [v(-326.35, -136.48) * mm, v(-326.35, -135.85) * mm, v(-326.02, -135.28) * mm, v(-325.48, -134.96) * mm]});
            skFitSpline(sketch, "E2054", {"points": [v(-325.48, -134.96) * mm, v(-324.94, -134.65) * mm, v(-324.27, -134.65) * mm, v(-323.73, -134.96) * mm]});
            skFitSpline(sketch, "E2055", {"points": [v(-323.73, -134.96) * mm, v(-323.2, -135.28) * mm, v(-322.86, -135.85) * mm, v(-322.86, -136.48) * mm]});
            skFitSpline(sketch, "E2056", {"points": [v(-259.56, -136.48) * mm, v(-259.56, -137.1) * mm, v(-259.9, -137.68) * mm, v(-260.43, -138) * mm]});
            skFitSpline(sketch, "E2057", {"points": [v(-260.43, -138) * mm, v(-260.97, -138.3) * mm, v(-261.64, -138.3) * mm, v(-262.18, -138) * mm]});
            skFitSpline(sketch, "E2058", {"points": [v(-262.18, -138) * mm, v(-262.72, -137.68) * mm, v(-263.05, -137.1) * mm, v(-263.05, -136.48) * mm]});
            skFitSpline(sketch, "E2059", {"points": [v(-263.05, -136.48) * mm, v(-263.05, -135.85) * mm, v(-262.72, -135.28) * mm, v(-262.18, -134.96) * mm]});
            skFitSpline(sketch, "E2060", {"points": [v(-262.18, -134.96) * mm, v(-261.64, -134.65) * mm, v(-260.97, -134.65) * mm, v(-260.43, -134.96) * mm]});
            skFitSpline(sketch, "E2061", {"points": [v(-260.43, -134.96) * mm, v(-259.9, -135.28) * mm, v(-259.56, -135.85) * mm, v(-259.56, -136.48) * mm]});
            skFitSpline(sketch, "E2062", {"points": [v(-196.26, -136.48) * mm, v(-196.26, -137.1) * mm, v(-196.6, -137.68) * mm, v(-197.13, -138) * mm]});
            skFitSpline(sketch, "E2063", {"points": [v(-197.13, -138) * mm, v(-197.67, -138.3) * mm, v(-198.34, -138.3) * mm, v(-198.88, -138) * mm]});
            skFitSpline(sketch, "E2064", {"points": [v(-198.88, -138) * mm, v(-199.42, -137.68) * mm, v(-199.75, -137.1) * mm, v(-199.75, -136.48) * mm]});
            skFitSpline(sketch, "E2065", {"points": [v(-199.75, -136.48) * mm, v(-199.75, -135.85) * mm, v(-199.42, -135.28) * mm, v(-198.88, -134.96) * mm]});
            skFitSpline(sketch, "E2066", {"points": [v(-198.88, -134.96) * mm, v(-198.34, -134.65) * mm, v(-197.67, -134.65) * mm, v(-197.13, -134.96) * mm]});
            skFitSpline(sketch, "E2067", {"points": [v(-197.13, -134.96) * mm, v(-196.6, -135.28) * mm, v(-196.26, -135.85) * mm, v(-196.26, -136.48) * mm]});
            skFitSpline(sketch, "E2068", {"points": [v(-132.96, -136.48) * mm, v(-132.96, -137.1) * mm, v(-133.3, -137.68) * mm, v(-133.83, -138) * mm]});
            skFitSpline(sketch, "E2069", {"points": [v(-133.83, -138) * mm, v(-134.37, -138.3) * mm, v(-135.04, -138.3) * mm, v(-135.58, -138) * mm]});
            skFitSpline(sketch, "E2070", {"points": [v(-135.58, -138) * mm, v(-136.12, -137.68) * mm, v(-136.45, -137.1) * mm, v(-136.45, -136.48) * mm]});
            skFitSpline(sketch, "E2071", {"points": [v(-136.45, -136.48) * mm, v(-136.45, -135.85) * mm, v(-136.12, -135.28) * mm, v(-135.58, -134.96) * mm]});
            skFitSpline(sketch, "E2072", {"points": [v(-135.58, -134.96) * mm, v(-135.04, -134.65) * mm, v(-134.37, -134.65) * mm, v(-133.83, -134.96) * mm]});
            skFitSpline(sketch, "E2073", {"points": [v(-133.83, -134.96) * mm, v(-133.3, -135.28) * mm, v(-132.96, -135.85) * mm, v(-132.96, -136.48) * mm]});
            skFitSpline(sketch, "E2074", {"points": [v(-69.66, -136.48) * mm, v(-69.66, -137.1) * mm, v(-70, -137.68) * mm, v(-70.53, -138) * mm]});
            skFitSpline(sketch, "E2075", {"points": [v(-70.53, -138) * mm, v(-71.07, -138.3) * mm, v(-71.74, -138.3) * mm, v(-72.28, -138) * mm]});
            skFitSpline(sketch, "E2076", {"points": [v(-72.28, -138) * mm, v(-72.82, -137.68) * mm, v(-73.15, -137.1) * mm, v(-73.15, -136.48) * mm]});
            skFitSpline(sketch, "E2077", {"points": [v(-73.15, -136.48) * mm, v(-73.15, -135.85) * mm, v(-72.82, -135.28) * mm, v(-72.28, -134.96) * mm]});
            skFitSpline(sketch, "E2078", {"points": [v(-72.28, -134.96) * mm, v(-71.74, -134.65) * mm, v(-71.07, -134.65) * mm, v(-70.53, -134.96) * mm]});
            skFitSpline(sketch, "E2079", {"points": [v(-70.53, -134.96) * mm, v(-70, -135.28) * mm, v(-69.66, -135.85) * mm, v(-69.66, -136.48) * mm]});
            skFitSpline(sketch, "E2080", {"points": [v(-6.36, -136.48) * mm, v(-6.36, -137.1) * mm, v(-6.7, -137.68) * mm, v(-7.23, -138) * mm]});
            skFitSpline(sketch, "E2081", {"points": [v(-7.23, -138) * mm, v(-7.77, -138.3) * mm, v(-8.44, -138.3) * mm, v(-8.98, -138) * mm]});
            skFitSpline(sketch, "E2082", {"points": [v(-8.98, -138) * mm, v(-9.52, -137.68) * mm, v(-9.85, -137.1) * mm, v(-9.85, -136.48) * mm]});
            skFitSpline(sketch, "E2083", {"points": [v(-9.85, -136.48) * mm, v(-9.85, -135.85) * mm, v(-9.52, -135.28) * mm, v(-8.98, -134.96) * mm]});
            skFitSpline(sketch, "E2084", {"points": [v(-8.98, -134.96) * mm, v(-8.44, -134.65) * mm, v(-7.77, -134.65) * mm, v(-7.23, -134.96) * mm]});
            skFitSpline(sketch, "E2085", {"points": [v(-7.23, -134.96) * mm, v(-6.7, -135.28) * mm, v(-6.36, -135.85) * mm, v(-6.36, -136.48) * mm]});
            skFitSpline(sketch, "E2086", {"points": [v(56.94, -136.48) * mm, v(56.94, -137.1) * mm, v(56.6, -137.68) * mm, v(56.07, -138) * mm]});
            skFitSpline(sketch, "E2087", {"points": [v(56.07, -138) * mm, v(55.53, -138.3) * mm, v(54.86, -138.3) * mm, v(54.32, -138) * mm]});
            skFitSpline(sketch, "E2088", {"points": [v(54.32, -138) * mm, v(53.78, -137.68) * mm, v(53.45, -137.1) * mm, v(53.45, -136.48) * mm]});
            skFitSpline(sketch, "E2089", {"points": [v(53.45, -136.48) * mm, v(53.45, -135.85) * mm, v(53.78, -135.28) * mm, v(54.32, -134.96) * mm]});
            skFitSpline(sketch, "E2090", {"points": [v(54.32, -134.96) * mm, v(54.86, -134.65) * mm, v(55.53, -134.65) * mm, v(56.07, -134.96) * mm]});
            skFitSpline(sketch, "E2091", {"points": [v(56.07, -134.96) * mm, v(56.6, -135.28) * mm, v(56.94, -135.85) * mm, v(56.94, -136.48) * mm]});
            skFitSpline(sketch, "E2092", {"points": [v(120.24, -136.48) * mm, v(120.24, -137.1) * mm, v(119.9, -137.68) * mm, v(119.37, -138) * mm]});
            skFitSpline(sketch, "E2093", {"points": [v(119.37, -138) * mm, v(118.83, -138.3) * mm, v(118.16, -138.3) * mm, v(117.62, -138) * mm]});
            skFitSpline(sketch, "E2094", {"points": [v(117.62, -138) * mm, v(117.08, -137.68) * mm, v(116.75, -137.1) * mm, v(116.75, -136.48) * mm]});
            skFitSpline(sketch, "E2095", {"points": [v(116.75, -136.48) * mm, v(116.75, -135.85) * mm, v(117.08, -135.28) * mm, v(117.62, -134.96) * mm]});
            skFitSpline(sketch, "E2096", {"points": [v(117.62, -134.96) * mm, v(118.16, -134.65) * mm, v(118.83, -134.65) * mm, v(119.37, -134.96) * mm]});
            skFitSpline(sketch, "E2097", {"points": [v(119.37, -134.96) * mm, v(119.9, -135.28) * mm, v(120.24, -135.85) * mm, v(120.24, -136.48) * mm]});
            skFitSpline(sketch, "E2098", {"points": [v(183.54, -136.48) * mm, v(183.54, -137.1) * mm, v(183.2, -137.68) * mm, v(182.67, -138) * mm]});
            skFitSpline(sketch, "E2099", {"points": [v(182.67, -138) * mm, v(182.13, -138.3) * mm, v(181.46, -138.3) * mm, v(180.92, -138) * mm]});
            skFitSpline(sketch, "E2100", {"points": [v(180.92, -138) * mm, v(180.38, -137.68) * mm, v(180.05, -137.1) * mm, v(180.05, -136.48) * mm]});
            skFitSpline(sketch, "E2101", {"points": [v(180.05, -136.48) * mm, v(180.05, -135.85) * mm, v(180.38, -135.28) * mm, v(180.92, -134.96) * mm]});
            skFitSpline(sketch, "E2102", {"points": [v(180.92, -134.96) * mm, v(181.46, -134.65) * mm, v(182.13, -134.65) * mm, v(182.67, -134.96) * mm]});
            skFitSpline(sketch, "E2103", {"points": [v(182.67, -134.96) * mm, v(183.2, -135.28) * mm, v(183.54, -135.85) * mm, v(183.54, -136.48) * mm]});
            skFitSpline(sketch, "E2104", {"points": [v(246.84, -136.48) * mm, v(246.84, -137.1) * mm, v(246.5, -137.68) * mm, v(245.97, -138) * mm]});
            skFitSpline(sketch, "E2105", {"points": [v(245.97, -138) * mm, v(245.43, -138.3) * mm, v(244.76, -138.3) * mm, v(244.22, -138) * mm]});
            skFitSpline(sketch, "E2106", {"points": [v(244.22, -138) * mm, v(243.68, -137.68) * mm, v(243.35, -137.1) * mm, v(243.35, -136.48) * mm]});
            skFitSpline(sketch, "E2107", {"points": [v(243.35, -136.48) * mm, v(243.35, -135.85) * mm, v(243.68, -135.28) * mm, v(244.22, -134.96) * mm]});
            skFitSpline(sketch, "E2108", {"points": [v(244.22, -134.96) * mm, v(244.76, -134.65) * mm, v(245.43, -134.65) * mm, v(245.97, -134.96) * mm]});
            skFitSpline(sketch, "E2109", {"points": [v(245.97, -134.96) * mm, v(246.5, -135.28) * mm, v(246.84, -135.85) * mm, v(246.84, -136.48) * mm]});
            skLineSegment(sketch, "E2110", {"start": v(316.68, 134.39) * mm, "end": v(313.5, 134.39) * mm});
            skLineSegment(sketch, "E2111", {"start": v(316.68, 134.39) * mm, "end": v(316.68, 143.63) * mm});
            skLineSegment(sketch, "E2112", {"start": v(316.68, 143.63) * mm, "end": v(313.5, 143.63) * mm});
            skLineSegment(sketch, "E2113", {"start": v(316.68, 152.57) * mm, "end": v(313.5, 152.57) * mm});
            skLineSegment(sketch, "E2114", {"start": v(316.68, 152.57) * mm, "end": v(316.68, 161.82) * mm});
            skLineSegment(sketch, "E2115", {"start": v(316.68, 161.82) * mm, "end": v(313.5, 161.82) * mm});
            skLineSegment(sketch, "E2116", {"start": v(316.68, 170.76) * mm, "end": v(313.5, 170.76) * mm});
            skLineSegment(sketch, "E2117", {"start": v(316.68, 170.76) * mm, "end": v(316.68, 180) * mm});
            skLineSegment(sketch, "E2118", {"start": v(316.68, 180) * mm, "end": v(313.5, 180) * mm});
            skLineSegment(sketch, "E2119", {"start": v(313.5, 180) * mm, "end": v(313.5, 189.02) * mm});
            skLineSegment(sketch, "E2120", {"start": v(313.5, 161.82) * mm, "end": v(313.5, 170.76) * mm});
            skLineSegment(sketch, "E2121", {"start": v(313.5, 143.63) * mm, "end": v(313.5, 152.57) * mm});
            skLineSegment(sketch, "E2122", {"start": v(313.5, 125.37) * mm, "end": v(313.5, 134.39) * mm});
            skLineSegment(sketch, "E2123", {"start": v(-445.47, 180) * mm, "end": v(-445.47, 189.02) * mm});
            skLineSegment(sketch, "E2124", {"start": v(-442.3, 180) * mm, "end": v(-445.47, 180) * mm});
            skLineSegment(sketch, "E2125", {"start": v(-442.3, 170.76) * mm, "end": v(-442.3, 180) * mm});
            skLineSegment(sketch, "E2126", {"start": v(-442.3, 170.76) * mm, "end": v(-445.47, 170.76) * mm});
            skLineSegment(sketch, "E2127", {"start": v(-445.47, 161.82) * mm, "end": v(-445.47, 170.76) * mm});
            skLineSegment(sketch, "E2128", {"start": v(-442.3, 161.82) * mm, "end": v(-445.47, 161.82) * mm});
            skLineSegment(sketch, "E2129", {"start": v(-442.3, 152.57) * mm, "end": v(-442.3, 161.82) * mm});
            skLineSegment(sketch, "E2130", {"start": v(-442.3, 152.57) * mm, "end": v(-445.47, 152.57) * mm});
            skLineSegment(sketch, "E2131", {"start": v(-445.47, 143.63) * mm, "end": v(-445.47, 152.57) * mm});
            skLineSegment(sketch, "E2132", {"start": v(-442.3, 143.63) * mm, "end": v(-445.47, 143.63) * mm});
            skLineSegment(sketch, "E2133", {"start": v(-442.3, 134.39) * mm, "end": v(-442.3, 143.63) * mm});
            skLineSegment(sketch, "E2134", {"start": v(-442.3, 134.39) * mm, "end": v(-445.47, 134.39) * mm});
            skLineSegment(sketch, "E2135", {"start": v(-445.47, 125.37) * mm, "end": v(-445.47, 134.39) * mm});
            skLineSegment(sketch, "E2136", {"start": v(-445.47, 189.02) * mm, "end": v(-437.37, 189.02) * mm});
            skLineSegment(sketch, "E2137", {"start": v(-437.37, 189.02) * mm, "end": v(308.58, 189.02) * mm});
            skLineSegment(sketch, "E2138", {"start": v(308.58, 189.02) * mm, "end": v(313.5, 189.02) * mm});
            skLineSegment(sketch, "E2139", {"start": v(308.58, 125.37) * mm, "end": v(313.5, 125.37) * mm});
            skLineSegment(sketch, "E2140", {"start": v(308.58, 128.54) * mm, "end": v(308.58, 125.37) * mm});
            skLineSegment(sketch, "E2141", {"start": v(300.71, 128.54) * mm, "end": v(308.58, 128.54) * mm});
            skLineSegment(sketch, "E2142", {"start": v(300.71, 128.54) * mm, "end": v(300.71, 125.37) * mm});
            skLineSegment(sketch, "E2143", {"start": v(292.54, 125.37) * mm, "end": v(300.71, 125.37) * mm});
            skLineSegment(sketch, "E2144", {"start": v(292.54, 128.54) * mm, "end": v(292.54, 125.37) * mm});
            skLineSegment(sketch, "E2145", {"start": v(284.67, 128.54) * mm, "end": v(292.54, 128.54) * mm});
            skLineSegment(sketch, "E2146", {"start": v(284.67, 128.54) * mm, "end": v(284.67, 125.37) * mm});
            skLineSegment(sketch, "E2147", {"start": v(276.5, 125.37) * mm, "end": v(284.67, 125.37) * mm});
            skLineSegment(sketch, "E2148", {"start": v(276.5, 128.54) * mm, "end": v(276.5, 125.37) * mm});
            skLineSegment(sketch, "E2149", {"start": v(268.62, 128.54) * mm, "end": v(276.5, 128.54) * mm});
            skLineSegment(sketch, "E2150", {"start": v(268.62, 128.54) * mm, "end": v(268.62, 125.37) * mm});
            skLineSegment(sketch, "E2151", {"start": v(260.45, 125.37) * mm, "end": v(268.62, 125.37) * mm});
            skLineSegment(sketch, "E2152", {"start": v(260.45, 128.54) * mm, "end": v(260.45, 125.37) * mm});
            skLineSegment(sketch, "E2153", {"start": v(252.58, 128.54) * mm, "end": v(260.45, 128.54) * mm});
            skLineSegment(sketch, "E2154", {"start": v(252.58, 128.54) * mm, "end": v(252.58, 125.37) * mm});
            skLineSegment(sketch, "E2155", {"start": v(244.4, 125.37) * mm, "end": v(252.58, 125.37) * mm});
            skLineSegment(sketch, "E2156", {"start": v(244.4, 128.54) * mm, "end": v(244.4, 125.37) * mm});
            skLineSegment(sketch, "E2157", {"start": v(236.53, 128.54) * mm, "end": v(244.4, 128.54) * mm});
            skLineSegment(sketch, "E2158", {"start": v(236.53, 128.54) * mm, "end": v(236.53, 125.37) * mm});
            skLineSegment(sketch, "E2159", {"start": v(228.35, 125.37) * mm, "end": v(236.53, 125.37) * mm});
            skLineSegment(sketch, "E2160", {"start": v(228.35, 128.54) * mm, "end": v(228.35, 125.37) * mm});
            skLineSegment(sketch, "E2161", {"start": v(220.48, 128.54) * mm, "end": v(228.35, 128.54) * mm});
            skLineSegment(sketch, "E2162", {"start": v(220.48, 128.54) * mm, "end": v(220.48, 125.37) * mm});
            skLineSegment(sketch, "E2163", {"start": v(212.3, 125.37) * mm, "end": v(220.48, 125.37) * mm});
            skLineSegment(sketch, "E2164", {"start": v(212.3, 128.54) * mm, "end": v(212.3, 125.37) * mm});
            skLineSegment(sketch, "E2165", {"start": v(204.44, 128.54) * mm, "end": v(212.3, 128.54) * mm});
            skLineSegment(sketch, "E2166", {"start": v(204.44, 128.54) * mm, "end": v(204.44, 125.37) * mm});
            skLineSegment(sketch, "E2167", {"start": v(196.26, 125.37) * mm, "end": v(204.44, 125.37) * mm});
            skLineSegment(sketch, "E2168", {"start": v(196.26, 128.54) * mm, "end": v(196.26, 125.37) * mm});
            skLineSegment(sketch, "E2169", {"start": v(188.4, 128.54) * mm, "end": v(196.26, 128.54) * mm});
            skLineSegment(sketch, "E2170", {"start": v(188.4, 128.54) * mm, "end": v(188.4, 125.37) * mm});
            skLineSegment(sketch, "E2171", {"start": v(180.22, 125.37) * mm, "end": v(188.4, 125.37) * mm});
            skLineSegment(sketch, "E2172", {"start": v(180.22, 128.54) * mm, "end": v(180.22, 125.37) * mm});
            skLineSegment(sketch, "E2173", {"start": v(172.35, 128.54) * mm, "end": v(180.22, 128.54) * mm});
            skLineSegment(sketch, "E2174", {"start": v(172.35, 128.54) * mm, "end": v(172.35, 125.37) * mm});
            skLineSegment(sketch, "E2175", {"start": v(164.17, 125.37) * mm, "end": v(172.35, 125.37) * mm});
            skLineSegment(sketch, "E2176", {"start": v(164.17, 128.54) * mm, "end": v(164.17, 125.37) * mm});
            skLineSegment(sketch, "E2177", {"start": v(156.3, 128.54) * mm, "end": v(164.17, 128.54) * mm});
            skLineSegment(sketch, "E2178", {"start": v(156.3, 128.54) * mm, "end": v(156.3, 125.37) * mm});
            skLineSegment(sketch, "E2179", {"start": v(148.13, 125.37) * mm, "end": v(156.3, 125.37) * mm});
            skLineSegment(sketch, "E2180", {"start": v(148.13, 128.54) * mm, "end": v(148.13, 125.37) * mm});
            skLineSegment(sketch, "E2181", {"start": v(140.26, 128.54) * mm, "end": v(148.13, 128.54) * mm});
            skLineSegment(sketch, "E2182", {"start": v(140.26, 128.54) * mm, "end": v(140.26, 125.37) * mm});
            skLineSegment(sketch, "E2183", {"start": v(132.08, 125.37) * mm, "end": v(140.26, 125.37) * mm});
            skLineSegment(sketch, "E2184", {"start": v(132.08, 128.54) * mm, "end": v(132.08, 125.37) * mm});
            skLineSegment(sketch, "E2185", {"start": v(124.21, 128.54) * mm, "end": v(132.08, 128.54) * mm});
            skLineSegment(sketch, "E2186", {"start": v(124.21, 128.54) * mm, "end": v(124.21, 125.37) * mm});
            skLineSegment(sketch, "E2187", {"start": v(116.04, 125.37) * mm, "end": v(124.21, 125.37) * mm});
            skLineSegment(sketch, "E2188", {"start": v(116.04, 128.54) * mm, "end": v(116.04, 125.37) * mm});
            skLineSegment(sketch, "E2189", {"start": v(108.17, 128.54) * mm, "end": v(116.04, 128.54) * mm});
            skLineSegment(sketch, "E2190", {"start": v(108.17, 128.54) * mm, "end": v(108.17, 125.37) * mm});
            skLineSegment(sketch, "E2191", {"start": v(100, 125.37) * mm, "end": v(108.17, 125.37) * mm});
            skLineSegment(sketch, "E2192", {"start": v(100, 128.54) * mm, "end": v(100, 125.37) * mm});
            skLineSegment(sketch, "E2193", {"start": v(92.12, 128.54) * mm, "end": v(100, 128.54) * mm});
            skLineSegment(sketch, "E2194", {"start": v(92.12, 128.54) * mm, "end": v(92.12, 125.37) * mm});
            skLineSegment(sketch, "E2195", {"start": v(83.95, 125.37) * mm, "end": v(92.12, 125.37) * mm});
            skLineSegment(sketch, "E2196", {"start": v(83.95, 128.54) * mm, "end": v(83.95, 125.37) * mm});
            skLineSegment(sketch, "E2197", {"start": v(76.08, 128.54) * mm, "end": v(83.95, 128.54) * mm});
            skLineSegment(sketch, "E2198", {"start": v(76.08, 128.54) * mm, "end": v(76.08, 125.37) * mm});
            skLineSegment(sketch, "E2199", {"start": v(67.9, 125.37) * mm, "end": v(76.08, 125.37) * mm});
            skLineSegment(sketch, "E2200", {"start": v(67.9, 128.54) * mm, "end": v(67.9, 125.37) * mm});
            skLineSegment(sketch, "E2201", {"start": v(60.03, 128.54) * mm, "end": v(67.9, 128.54) * mm});
            skLineSegment(sketch, "E2202", {"start": v(60.03, 128.54) * mm, "end": v(60.03, 125.37) * mm});
            skLineSegment(sketch, "E2203", {"start": v(51.86, 125.37) * mm, "end": v(60.03, 125.37) * mm});
            skLineSegment(sketch, "E2204", {"start": v(51.86, 128.54) * mm, "end": v(51.86, 125.37) * mm});
            skLineSegment(sketch, "E2205", {"start": v(43.99, 128.54) * mm, "end": v(51.86, 128.54) * mm});
            skLineSegment(sketch, "E2206", {"start": v(43.99, 128.54) * mm, "end": v(43.99, 125.37) * mm});
            skLineSegment(sketch, "E2207", {"start": v(35.81, 125.37) * mm, "end": v(43.99, 125.37) * mm});
            skLineSegment(sketch, "E2208", {"start": v(35.81, 128.54) * mm, "end": v(35.81, 125.37) * mm});
            skLineSegment(sketch, "E2209", {"start": v(27.94, 128.54) * mm, "end": v(35.81, 128.54) * mm});
            skLineSegment(sketch, "E2210", {"start": v(27.94, 128.54) * mm, "end": v(27.94, 125.37) * mm});
            skLineSegment(sketch, "E2211", {"start": v(19.77, 125.37) * mm, "end": v(27.94, 125.37) * mm});
            skLineSegment(sketch, "E2212", {"start": v(19.77, 128.54) * mm, "end": v(19.77, 125.37) * mm});
            skLineSegment(sketch, "E2213", {"start": v(11.9, 128.54) * mm, "end": v(19.77, 128.54) * mm});
            skLineSegment(sketch, "E2214", {"start": v(11.9, 128.54) * mm, "end": v(11.9, 125.37) * mm});
            skLineSegment(sketch, "E2215", {"start": v(3.72, 125.37) * mm, "end": v(11.9, 125.37) * mm});
            skLineSegment(sketch, "E2216", {"start": v(3.72, 128.54) * mm, "end": v(3.72, 125.37) * mm});
            skLineSegment(sketch, "E2217", {"start": v(-4.15, 128.54) * mm, "end": v(3.72, 128.54) * mm});
            skLineSegment(sketch, "E2218", {"start": v(-4.15, 128.54) * mm, "end": v(-4.15, 125.37) * mm});
            skLineSegment(sketch, "E2219", {"start": v(-12.32, 125.37) * mm, "end": v(-4.15, 125.37) * mm});
            skLineSegment(sketch, "E2220", {"start": v(-12.32, 128.54) * mm, "end": v(-12.32, 125.37) * mm});
            skLineSegment(sketch, "E2221", {"start": v(-20.2, 128.54) * mm, "end": v(-12.32, 128.54) * mm});
            skLineSegment(sketch, "E2222", {"start": v(-20.2, 128.54) * mm, "end": v(-20.2, 125.37) * mm});
            skLineSegment(sketch, "E2223", {"start": v(-28.37, 125.37) * mm, "end": v(-20.2, 125.37) * mm});
            skLineSegment(sketch, "E2224", {"start": v(-28.37, 128.54) * mm, "end": v(-28.37, 125.37) * mm});
            skLineSegment(sketch, "E2225", {"start": v(-36.24, 128.54) * mm, "end": v(-28.37, 128.54) * mm});
            skLineSegment(sketch, "E2226", {"start": v(-36.24, 128.54) * mm, "end": v(-36.24, 125.37) * mm});
            skLineSegment(sketch, "E2227", {"start": v(-44.42, 125.37) * mm, "end": v(-36.24, 125.37) * mm});
            skLineSegment(sketch, "E2228", {"start": v(-44.42, 128.54) * mm, "end": v(-44.42, 125.37) * mm});
            skLineSegment(sketch, "E2229", {"start": v(-52.29, 128.54) * mm, "end": v(-44.42, 128.54) * mm});
            skLineSegment(sketch, "E2230", {"start": v(-52.29, 128.54) * mm, "end": v(-52.29, 125.37) * mm});
            skLineSegment(sketch, "E2231", {"start": v(-60.46, 125.37) * mm, "end": v(-52.29, 125.37) * mm});
            skLineSegment(sketch, "E2232", {"start": v(-60.46, 128.54) * mm, "end": v(-60.46, 125.37) * mm});
            skLineSegment(sketch, "E2233", {"start": v(-68.33, 128.54) * mm, "end": v(-60.46, 128.54) * mm});
            skLineSegment(sketch, "E2234", {"start": v(-68.33, 128.54) * mm, "end": v(-68.33, 125.37) * mm});
            skLineSegment(sketch, "E2235", {"start": v(-76.5, 125.37) * mm, "end": v(-68.33, 125.37) * mm});
            skLineSegment(sketch, "E2236", {"start": v(-76.5, 128.54) * mm, "end": v(-76.5, 125.37) * mm});
            skLineSegment(sketch, "E2237", {"start": v(-84.38, 128.54) * mm, "end": v(-76.5, 128.54) * mm});
            skLineSegment(sketch, "E2238", {"start": v(-84.38, 128.54) * mm, "end": v(-84.38, 125.37) * mm});
            skLineSegment(sketch, "E2239", {"start": v(-92.55, 125.37) * mm, "end": v(-84.38, 125.37) * mm});
            skLineSegment(sketch, "E2240", {"start": v(-92.55, 128.54) * mm, "end": v(-92.55, 125.37) * mm});
            skLineSegment(sketch, "E2241", {"start": v(-100.42, 128.54) * mm, "end": v(-92.55, 128.54) * mm});
            skLineSegment(sketch, "E2242", {"start": v(-100.42, 128.54) * mm, "end": v(-100.42, 125.37) * mm});
            skLineSegment(sketch, "E2243", {"start": v(-108.6, 125.37) * mm, "end": v(-100.42, 125.37) * mm});
            skLineSegment(sketch, "E2244", {"start": v(-108.6, 128.54) * mm, "end": v(-108.6, 125.37) * mm});
            skLineSegment(sketch, "E2245", {"start": v(-116.47, 128.54) * mm, "end": v(-108.6, 128.54) * mm});
            skLineSegment(sketch, "E2246", {"start": v(-116.47, 128.54) * mm, "end": v(-116.47, 125.37) * mm});
            skLineSegment(sketch, "E2247", {"start": v(-124.64, 125.37) * mm, "end": v(-116.47, 125.37) * mm});
            skLineSegment(sketch, "E2248", {"start": v(-124.64, 128.54) * mm, "end": v(-124.64, 125.37) * mm});
            skLineSegment(sketch, "E2249", {"start": v(-132.51, 128.54) * mm, "end": v(-124.64, 128.54) * mm});
            skLineSegment(sketch, "E2250", {"start": v(-132.51, 128.54) * mm, "end": v(-132.51, 125.37) * mm});
            skLineSegment(sketch, "E2251", {"start": v(-140.69, 125.37) * mm, "end": v(-132.51, 125.37) * mm});
            skLineSegment(sketch, "E2252", {"start": v(-140.69, 128.54) * mm, "end": v(-140.69, 125.37) * mm});
            skLineSegment(sketch, "E2253", {"start": v(-148.56, 128.54) * mm, "end": v(-140.69, 128.54) * mm});
            skLineSegment(sketch, "E2254", {"start": v(-148.56, 128.54) * mm, "end": v(-148.56, 125.37) * mm});
            skLineSegment(sketch, "E2255", {"start": v(-156.73, 125.37) * mm, "end": v(-148.56, 125.37) * mm});
            skLineSegment(sketch, "E2256", {"start": v(-156.73, 128.54) * mm, "end": v(-156.73, 125.37) * mm});
            skLineSegment(sketch, "E2257", {"start": v(-164.6, 128.54) * mm, "end": v(-156.73, 128.54) * mm});
            skLineSegment(sketch, "E2258", {"start": v(-164.6, 128.54) * mm, "end": v(-164.6, 125.37) * mm});
            skLineSegment(sketch, "E2259", {"start": v(-172.78, 125.37) * mm, "end": v(-164.6, 125.37) * mm});
            skLineSegment(sketch, "E2260", {"start": v(-172.78, 128.54) * mm, "end": v(-172.78, 125.37) * mm});
            skLineSegment(sketch, "E2261", {"start": v(-180.65, 128.54) * mm, "end": v(-172.78, 128.54) * mm});
            skLineSegment(sketch, "E2262", {"start": v(-180.65, 128.54) * mm, "end": v(-180.65, 125.37) * mm});
            skLineSegment(sketch, "E2263", {"start": v(-188.82, 125.37) * mm, "end": v(-180.65, 125.37) * mm});
            skLineSegment(sketch, "E2264", {"start": v(-188.82, 128.54) * mm, "end": v(-188.82, 125.37) * mm});
            skLineSegment(sketch, "E2265", {"start": v(-196.7, 128.54) * mm, "end": v(-188.82, 128.54) * mm});
            skLineSegment(sketch, "E2266", {"start": v(-196.7, 128.54) * mm, "end": v(-196.7, 125.37) * mm});
            skLineSegment(sketch, "E2267", {"start": v(-204.87, 125.37) * mm, "end": v(-196.7, 125.37) * mm});
            skLineSegment(sketch, "E2268", {"start": v(-204.87, 128.54) * mm, "end": v(-204.87, 125.37) * mm});
            skLineSegment(sketch, "E2269", {"start": v(-212.74, 128.54) * mm, "end": v(-204.87, 128.54) * mm});
            skLineSegment(sketch, "E2270", {"start": v(-212.74, 128.54) * mm, "end": v(-212.74, 125.37) * mm});
            skLineSegment(sketch, "E2271", {"start": v(-220.91, 125.37) * mm, "end": v(-212.74, 125.37) * mm});
            skLineSegment(sketch, "E2272", {"start": v(-220.91, 128.54) * mm, "end": v(-220.91, 125.37) * mm});
            skLineSegment(sketch, "E2273", {"start": v(-228.78, 128.54) * mm, "end": v(-220.91, 128.54) * mm});
            skLineSegment(sketch, "E2274", {"start": v(-228.78, 128.54) * mm, "end": v(-228.78, 125.37) * mm});
            skLineSegment(sketch, "E2275", {"start": v(-236.96, 125.37) * mm, "end": v(-228.78, 125.37) * mm});
            skLineSegment(sketch, "E2276", {"start": v(-236.96, 128.54) * mm, "end": v(-236.96, 125.37) * mm});
            skLineSegment(sketch, "E2277", {"start": v(-244.83, 128.54) * mm, "end": v(-236.96, 128.54) * mm});
            skLineSegment(sketch, "E2278", {"start": v(-244.83, 128.54) * mm, "end": v(-244.83, 125.37) * mm});
            skLineSegment(sketch, "E2279", {"start": v(-253, 125.37) * mm, "end": v(-244.83, 125.37) * mm});
            skLineSegment(sketch, "E2280", {"start": v(-253, 128.54) * mm, "end": v(-253, 125.37) * mm});
            skLineSegment(sketch, "E2281", {"start": v(-260.87, 128.54) * mm, "end": v(-253, 128.54) * mm});
            skLineSegment(sketch, "E2282", {"start": v(-260.87, 128.54) * mm, "end": v(-260.87, 125.37) * mm});
            skLineSegment(sketch, "E2283", {"start": v(-269.05, 125.37) * mm, "end": v(-260.87, 125.37) * mm});
            skLineSegment(sketch, "E2284", {"start": v(-269.05, 128.54) * mm, "end": v(-269.05, 125.37) * mm});
            skLineSegment(sketch, "E2285", {"start": v(-276.92, 128.54) * mm, "end": v(-269.05, 128.54) * mm});
            skLineSegment(sketch, "E2286", {"start": v(-276.92, 128.54) * mm, "end": v(-276.92, 125.37) * mm});
            skLineSegment(sketch, "E2287", {"start": v(-285.1, 125.37) * mm, "end": v(-276.92, 125.37) * mm});
            skLineSegment(sketch, "E2288", {"start": v(-285.1, 128.54) * mm, "end": v(-285.1, 125.37) * mm});
            skLineSegment(sketch, "E2289", {"start": v(-292.97, 128.54) * mm, "end": v(-285.1, 128.54) * mm});
            skLineSegment(sketch, "E2290", {"start": v(-292.97, 128.54) * mm, "end": v(-292.97, 125.37) * mm});
            skLineSegment(sketch, "E2291", {"start": v(-301.14, 125.37) * mm, "end": v(-292.97, 125.37) * mm});
            skLineSegment(sketch, "E2292", {"start": v(-301.14, 128.54) * mm, "end": v(-301.14, 125.37) * mm});
            skLineSegment(sketch, "E2293", {"start": v(-309.01, 128.54) * mm, "end": v(-301.14, 128.54) * mm});
            skLineSegment(sketch, "E2294", {"start": v(-309.01, 128.54) * mm, "end": v(-309.01, 125.37) * mm});
            skLineSegment(sketch, "E2295", {"start": v(-317.19, 125.37) * mm, "end": v(-309.01, 125.37) * mm});
            skLineSegment(sketch, "E2296", {"start": v(-317.19, 128.54) * mm, "end": v(-317.19, 125.37) * mm});
            skLineSegment(sketch, "E2297", {"start": v(-325.06, 128.54) * mm, "end": v(-317.19, 128.54) * mm});
            skLineSegment(sketch, "E2298", {"start": v(-325.06, 128.54) * mm, "end": v(-325.06, 125.37) * mm});
            skLineSegment(sketch, "E2299", {"start": v(-333.23, 125.37) * mm, "end": v(-325.06, 125.37) * mm});
            skLineSegment(sketch, "E2300", {"start": v(-333.23, 128.54) * mm, "end": v(-333.23, 125.37) * mm});
            skLineSegment(sketch, "E2301", {"start": v(-341.1, 128.54) * mm, "end": v(-333.23, 128.54) * mm});
            skLineSegment(sketch, "E2302", {"start": v(-341.1, 128.54) * mm, "end": v(-341.1, 125.37) * mm});
            skLineSegment(sketch, "E2303", {"start": v(-349.28, 125.37) * mm, "end": v(-341.1, 125.37) * mm});
            skLineSegment(sketch, "E2304", {"start": v(-349.28, 128.54) * mm, "end": v(-349.28, 125.37) * mm});
            skLineSegment(sketch, "E2305", {"start": v(-357.15, 128.54) * mm, "end": v(-349.28, 128.54) * mm});
            skLineSegment(sketch, "E2306", {"start": v(-357.15, 128.54) * mm, "end": v(-357.15, 125.37) * mm});
            skLineSegment(sketch, "E2307", {"start": v(-365.32, 125.37) * mm, "end": v(-357.15, 125.37) * mm});
            skLineSegment(sketch, "E2308", {"start": v(-365.32, 128.54) * mm, "end": v(-365.32, 125.37) * mm});
            skLineSegment(sketch, "E2309", {"start": v(-373.2, 128.54) * mm, "end": v(-365.32, 128.54) * mm});
            skLineSegment(sketch, "E2310", {"start": v(-373.2, 128.54) * mm, "end": v(-373.2, 125.37) * mm});
            skLineSegment(sketch, "E2311", {"start": v(-381.37, 125.37) * mm, "end": v(-373.2, 125.37) * mm});
            skLineSegment(sketch, "E2312", {"start": v(-381.37, 128.54) * mm, "end": v(-381.37, 125.37) * mm});
            skLineSegment(sketch, "E2313", {"start": v(-389.24, 128.54) * mm, "end": v(-381.37, 128.54) * mm});
            skLineSegment(sketch, "E2314", {"start": v(-389.24, 128.54) * mm, "end": v(-389.24, 125.37) * mm});
            skLineSegment(sketch, "E2315", {"start": v(-397.41, 125.37) * mm, "end": v(-389.24, 125.37) * mm});
            skLineSegment(sketch, "E2316", {"start": v(-397.41, 128.54) * mm, "end": v(-397.41, 125.37) * mm});
            skLineSegment(sketch, "E2317", {"start": v(-405.28, 128.54) * mm, "end": v(-397.41, 128.54) * mm});
            skLineSegment(sketch, "E2318", {"start": v(-405.28, 128.54) * mm, "end": v(-405.28, 125.37) * mm});
            skLineSegment(sketch, "E2319", {"start": v(-413.46, 125.37) * mm, "end": v(-405.28, 125.37) * mm});
            skLineSegment(sketch, "E2320", {"start": v(-413.46, 128.54) * mm, "end": v(-413.46, 125.37) * mm});
            skLineSegment(sketch, "E2321", {"start": v(-421.33, 128.54) * mm, "end": v(-413.46, 128.54) * mm});
            skLineSegment(sketch, "E2322", {"start": v(-421.33, 128.54) * mm, "end": v(-421.33, 125.37) * mm});
            skLineSegment(sketch, "E2323", {"start": v(-429.5, 125.37) * mm, "end": v(-421.33, 125.37) * mm});
            skLineSegment(sketch, "E2324", {"start": v(-429.5, 128.54) * mm, "end": v(-429.5, 125.37) * mm});
            skLineSegment(sketch, "E2325", {"start": v(-437.37, 128.54) * mm, "end": v(-429.5, 128.54) * mm});
            skLineSegment(sketch, "E2326", {"start": v(-437.37, 128.54) * mm, "end": v(-437.37, 125.37) * mm});
            skFitSpline(sketch, "E2327", {"points": [v(257, 177.91) * mm, v(256.99, 177.29) * mm, v(257.32, 176.71) * mm, v(257.86, 176.4) * mm]});
            skFitSpline(sketch, "E2328", {"points": [v(257.86, 176.4) * mm, v(258.4, 176.09) * mm, v(259.07, 176.09) * mm, v(259.6, 176.4) * mm]});
            skFitSpline(sketch, "E2329", {"points": [v(259.6, 176.4) * mm, v(260.15, 176.71) * mm, v(260.48, 177.29) * mm, v(260.48, 177.91) * mm]});
            skFitSpline(sketch, "E2330", {"points": [v(260.48, 177.91) * mm, v(260.48, 178.54) * mm, v(260.15, 179.11) * mm, v(259.6, 179.43) * mm]});
            skFitSpline(sketch, "E2331", {"points": [v(259.6, 179.43) * mm, v(259.07, 179.74) * mm, v(258.4, 179.74) * mm, v(257.86, 179.43) * mm]});
            skFitSpline(sketch, "E2332", {"points": [v(257.86, 179.43) * mm, v(257.32, 179.11) * mm, v(256.99, 178.54) * mm, v(257, 177.91) * mm]});
            skLineSegment(sketch, "E2333", {"start": v(-445.47, 125.37) * mm, "end": v(-437.37, 125.37) * mm});
            skFitSpline(sketch, "E2334", {"points": [v(193.7, 177.91) * mm, v(193.69, 177.29) * mm, v(194.02, 176.71) * mm, v(194.56, 176.4) * mm]});
            skFitSpline(sketch, "E2335", {"points": [v(194.56, 176.4) * mm, v(195.1, 176.09) * mm, v(195.77, 176.09) * mm, v(196.3, 176.4) * mm]});
            skFitSpline(sketch, "E2336", {"points": [v(196.3, 176.4) * mm, v(196.85, 176.71) * mm, v(197.18, 177.29) * mm, v(197.18, 177.91) * mm]});
            skFitSpline(sketch, "E2337", {"points": [v(197.18, 177.91) * mm, v(197.18, 178.54) * mm, v(196.85, 179.11) * mm, v(196.3, 179.43) * mm]});
            skFitSpline(sketch, "E2338", {"points": [v(196.3, 179.43) * mm, v(195.77, 179.74) * mm, v(195.1, 179.74) * mm, v(194.56, 179.43) * mm]});
            skFitSpline(sketch, "E2339", {"points": [v(194.56, 179.43) * mm, v(194.02, 179.11) * mm, v(193.69, 178.54) * mm, v(193.7, 177.91) * mm]});
            skFitSpline(sketch, "E2340", {"points": [v(130.4, 177.91) * mm, v(130.39, 177.29) * mm, v(130.72, 176.71) * mm, v(131.26, 176.4) * mm]});
            skFitSpline(sketch, "E2341", {"points": [v(131.26, 176.4) * mm, v(131.8, 176.09) * mm, v(132.47, 176.09) * mm, v(133, 176.4) * mm]});
            skFitSpline(sketch, "E2342", {"points": [v(133, 176.4) * mm, v(133.55, 176.71) * mm, v(133.88, 177.29) * mm, v(133.88, 177.91) * mm]});
            skFitSpline(sketch, "E2343", {"points": [v(133.88, 177.91) * mm, v(133.88, 178.54) * mm, v(133.55, 179.11) * mm, v(133, 179.43) * mm]});
            skFitSpline(sketch, "E2344", {"points": [v(133, 179.43) * mm, v(132.47, 179.74) * mm, v(131.8, 179.74) * mm, v(131.26, 179.43) * mm]});
            skFitSpline(sketch, "E2345", {"points": [v(131.26, 179.43) * mm, v(130.72, 179.11) * mm, v(130.39, 178.54) * mm, v(130.4, 177.91) * mm]});
            skFitSpline(sketch, "E2346", {"points": [v(67.1, 177.91) * mm, v(67.09, 177.29) * mm, v(67.42, 176.71) * mm, v(67.96, 176.4) * mm]});
            skFitSpline(sketch, "E2347", {"points": [v(67.96, 176.4) * mm, v(68.5, 176.09) * mm, v(69.17, 176.09) * mm, v(69.7, 176.4) * mm]});
            skFitSpline(sketch, "E2348", {"points": [v(69.7, 176.4) * mm, v(70.25, 176.71) * mm, v(70.58, 177.29) * mm, v(70.58, 177.91) * mm]});
            skFitSpline(sketch, "E2349", {"points": [v(70.58, 177.91) * mm, v(70.58, 178.54) * mm, v(70.25, 179.11) * mm, v(69.7, 179.43) * mm]});
            skFitSpline(sketch, "E2350", {"points": [v(69.7, 179.43) * mm, v(69.17, 179.74) * mm, v(68.5, 179.74) * mm, v(67.96, 179.43) * mm]});
            skFitSpline(sketch, "E2351", {"points": [v(67.96, 179.43) * mm, v(67.42, 179.11) * mm, v(67.09, 178.54) * mm, v(67.1, 177.91) * mm]});
            skFitSpline(sketch, "E2352", {"points": [v(3.8, 177.91) * mm, v(3.79, 177.29) * mm, v(4.12, 176.71) * mm, v(4.66, 176.4) * mm]});
            skFitSpline(sketch, "E2353", {"points": [v(4.66, 176.4) * mm, v(5.2, 176.09) * mm, v(5.87, 176.09) * mm, v(6.4, 176.4) * mm]});
            skFitSpline(sketch, "E2354", {"points": [v(6.4, 176.4) * mm, v(6.95, 176.71) * mm, v(7.28, 177.29) * mm, v(7.28, 177.91) * mm]});
            skFitSpline(sketch, "E2355", {"points": [v(7.28, 177.91) * mm, v(7.28, 178.54) * mm, v(6.95, 179.11) * mm, v(6.4, 179.43) * mm]});
            skFitSpline(sketch, "E2356", {"points": [v(6.4, 179.43) * mm, v(5.87, 179.74) * mm, v(5.2, 179.74) * mm, v(4.66, 179.43) * mm]});
            skFitSpline(sketch, "E2357", {"points": [v(4.66, 179.43) * mm, v(4.12, 179.11) * mm, v(3.79, 178.54) * mm, v(3.8, 177.91) * mm]});
            skFitSpline(sketch, "E2358", {"points": [v(-59.5, 177.91) * mm, v(-59.51, 177.29) * mm, v(-59.18, 176.71) * mm, v(-58.64, 176.4) * mm]});
            skFitSpline(sketch, "E2359", {"points": [v(-58.64, 176.4) * mm, v(-58.1, 176.09) * mm, v(-57.43, 176.09) * mm, v(-56.9, 176.4) * mm]});
            skFitSpline(sketch, "E2360", {"points": [v(-56.9, 176.4) * mm, v(-56.35, 176.71) * mm, v(-56.02, 177.29) * mm, v(-56.02, 177.91) * mm]});
            skFitSpline(sketch, "E2361", {"points": [v(-56.02, 177.91) * mm, v(-56.02, 178.54) * mm, v(-56.35, 179.11) * mm, v(-56.9, 179.43) * mm]});
            skFitSpline(sketch, "E2362", {"points": [v(-56.9, 179.43) * mm, v(-57.43, 179.74) * mm, v(-58.1, 179.74) * mm, v(-58.64, 179.43) * mm]});
            skFitSpline(sketch, "E2363", {"points": [v(-58.64, 179.43) * mm, v(-59.18, 179.11) * mm, v(-59.51, 178.54) * mm, v(-59.5, 177.91) * mm]});
            skFitSpline(sketch, "E2364", {"points": [v(-122.8, 177.91) * mm, v(-122.81, 177.29) * mm, v(-122.48, 176.71) * mm, v(-121.94, 176.4) * mm]});
            skFitSpline(sketch, "E2365", {"points": [v(-121.94, 176.4) * mm, v(-121.4, 176.09) * mm, v(-120.73, 176.09) * mm, v(-120.2, 176.4) * mm]});
            skFitSpline(sketch, "E2366", {"points": [v(-120.2, 176.4) * mm, v(-119.65, 176.71) * mm, v(-119.32, 177.29) * mm, v(-119.32, 177.91) * mm]});
            skFitSpline(sketch, "E2367", {"points": [v(-119.32, 177.91) * mm, v(-119.32, 178.54) * mm, v(-119.65, 179.11) * mm, v(-120.2, 179.43) * mm]});
            skFitSpline(sketch, "E2368", {"points": [v(-120.2, 179.43) * mm, v(-120.73, 179.74) * mm, v(-121.4, 179.74) * mm, v(-121.94, 179.43) * mm]});
            skFitSpline(sketch, "E2369", {"points": [v(-121.94, 179.43) * mm, v(-122.48, 179.11) * mm, v(-122.81, 178.54) * mm, v(-122.8, 177.91) * mm]});
            skFitSpline(sketch, "E2370", {"points": [v(-186.1, 177.91) * mm, v(-186.11, 177.29) * mm, v(-185.78, 176.71) * mm, v(-185.24, 176.4) * mm]});
            skFitSpline(sketch, "E2371", {"points": [v(-185.24, 176.4) * mm, v(-184.7, 176.09) * mm, v(-184.03, 176.09) * mm, v(-183.5, 176.4) * mm]});
            skFitSpline(sketch, "E2372", {"points": [v(-183.5, 176.4) * mm, v(-182.95, 176.71) * mm, v(-182.62, 177.29) * mm, v(-182.62, 177.91) * mm]});
            skFitSpline(sketch, "E2373", {"points": [v(-182.62, 177.91) * mm, v(-182.62, 178.54) * mm, v(-182.95, 179.11) * mm, v(-183.5, 179.43) * mm]});
            skFitSpline(sketch, "E2374", {"points": [v(-183.5, 179.43) * mm, v(-184.03, 179.74) * mm, v(-184.7, 179.74) * mm, v(-185.24, 179.43) * mm]});
            skFitSpline(sketch, "E2375", {"points": [v(-185.24, 179.43) * mm, v(-185.78, 179.11) * mm, v(-186.11, 178.54) * mm, v(-186.1, 177.91) * mm]});
            skFitSpline(sketch, "E2376", {"points": [v(-249.4, 177.91) * mm, v(-249.41, 177.29) * mm, v(-249.08, 176.71) * mm, v(-248.54, 176.4) * mm]});
            skFitSpline(sketch, "E2377", {"points": [v(-248.54, 176.4) * mm, v(-248, 176.09) * mm, v(-247.33, 176.09) * mm, v(-246.8, 176.4) * mm]});
            skFitSpline(sketch, "E2378", {"points": [v(-246.8, 176.4) * mm, v(-246.25, 176.71) * mm, v(-245.92, 177.29) * mm, v(-245.92, 177.91) * mm]});
            skFitSpline(sketch, "E2379", {"points": [v(-245.92, 177.91) * mm, v(-245.92, 178.54) * mm, v(-246.25, 179.11) * mm, v(-246.8, 179.43) * mm]});
            skFitSpline(sketch, "E2380", {"points": [v(-246.8, 179.43) * mm, v(-247.33, 179.74) * mm, v(-248, 179.74) * mm, v(-248.54, 179.43) * mm]});
            skFitSpline(sketch, "E2381", {"points": [v(-248.54, 179.43) * mm, v(-249.08, 179.11) * mm, v(-249.41, 178.54) * mm, v(-249.4, 177.91) * mm]});
            skFitSpline(sketch, "E2382", {"points": [v(-312.7, 177.91) * mm, v(-312.71, 177.29) * mm, v(-312.38, 176.71) * mm, v(-311.84, 176.4) * mm]});
            skFitSpline(sketch, "E2383", {"points": [v(-311.84, 176.4) * mm, v(-311.3, 176.09) * mm, v(-310.63, 176.09) * mm, v(-310.1, 176.4) * mm]});
            skFitSpline(sketch, "E2384", {"points": [v(-310.1, 176.4) * mm, v(-309.55, 176.71) * mm, v(-309.22, 177.29) * mm, v(-309.22, 177.91) * mm]});
            skFitSpline(sketch, "E2385", {"points": [v(-309.22, 177.91) * mm, v(-309.22, 178.54) * mm, v(-309.55, 179.11) * mm, v(-310.1, 179.43) * mm]});
            skFitSpline(sketch, "E2386", {"points": [v(-310.1, 179.43) * mm, v(-310.63, 179.74) * mm, v(-311.3, 179.74) * mm, v(-311.84, 179.43) * mm]});
            skFitSpline(sketch, "E2387", {"points": [v(-311.84, 179.43) * mm, v(-312.38, 179.11) * mm, v(-312.71, 178.54) * mm, v(-312.7, 177.91) * mm]});
            skFitSpline(sketch, "E2388", {"points": [v(-376, 177.91) * mm, v(-376.01, 177.29) * mm, v(-375.68, 176.71) * mm, v(-375.14, 176.4) * mm]});
            skFitSpline(sketch, "E2389", {"points": [v(-375.14, 176.4) * mm, v(-374.6, 176.09) * mm, v(-373.93, 176.09) * mm, v(-373.4, 176.4) * mm]});
            skFitSpline(sketch, "E2390", {"points": [v(-373.4, 176.4) * mm, v(-372.85, 176.71) * mm, v(-372.52, 177.29) * mm, v(-372.52, 177.91) * mm]});
            skFitSpline(sketch, "E2391", {"points": [v(-372.52, 177.91) * mm, v(-372.52, 178.54) * mm, v(-372.85, 179.11) * mm, v(-373.4, 179.43) * mm]});
            skFitSpline(sketch, "E2392", {"points": [v(-373.4, 179.43) * mm, v(-373.93, 179.74) * mm, v(-374.6, 179.74) * mm, v(-375.14, 179.43) * mm]});
            skFitSpline(sketch, "E2393", {"points": [v(-375.14, 179.43) * mm, v(-375.68, 179.11) * mm, v(-376.01, 178.54) * mm, v(-376, 177.91) * mm]});
            skSolve(sketch);
        }
        {
            var Q0;
            Q0=makeQuery(id+"F0.imprint","IMPRINT",FACE,{"disambiguationData":[TD([[makeQuery(id+"F0.imprint","IMPRINT",EDGE,{"derivedFrom":sQuery(id+"F0.wireOp",EDGE,"E1637")}),1.0]])]});
            var Q1;
            Q1=makeQuery(id+"F0.imprint","IMPRINT",FACE,{"disambiguationData":[TD([[makeQuery(id+"F0.imprint","IMPRINT",EDGE,{"derivedFrom":sQuery(id+"F0.wireOp",EDGE,"E388")}),1.0]])]});
            var Q2;
            Q2=makeQuery(id+"F0.imprint","IMPRINT",FACE,{"disambiguationData":[TD([[makeQuery(id+"F0.imprint","IMPRINT",EDGE,{"derivedFrom":sQuery(id+"F0.wireOp",EDGE,"E1165")}),1.0]])]});
            var Q3;
            {var subQ3=sQuery(id+"F0.wireOp",EDGE,"E1");Q3=makeQuery(id+"F0.imprint","IMPRINT",FACE,{"disambiguationData":[TD([[makeQuery(id+"F0.imprint","IMPRINT",EDGE,{"derivedFrom":subQ3}),1.0]])]});}
            var Q4;
            Q4=makeQuery(id+"F0.imprint","IMPRINT",FACE,{"disambiguationData":[TD([[makeQuery(id+"F0.imprint","IMPRINT",EDGE,{"derivedFrom":sQuery(id+"F0.wireOp",EDGE,"E2110")}),-1.0]])]});
            var Q5;
            Q5=makeQuery(id+"F0.imprint","IMPRINT",FACE,{"disambiguationData":[TD([[makeQuery(id+"F0.imprint","IMPRINT",EDGE,{"derivedFrom":sQuery(id+"F0.wireOp",EDGE,"E1014")}),1.0]])]});
            var Q6;
            Q6=makeQuery(id+"F0.imprint","IMPRINT",FACE,{"disambiguationData":[TD([[makeQuery(id+"F0.imprint","IMPRINT",EDGE,{"derivedFrom":sQuery(id+"F0.wireOp",EDGE,"E1088")}),1.0]])]});
            extrude(context, id + "F1", {"entities" : qUnion([Q0, Q1, Q2, Q3, Q4, Q5, Q6]), "depth" : 3.17 * mm});
        }
    });
